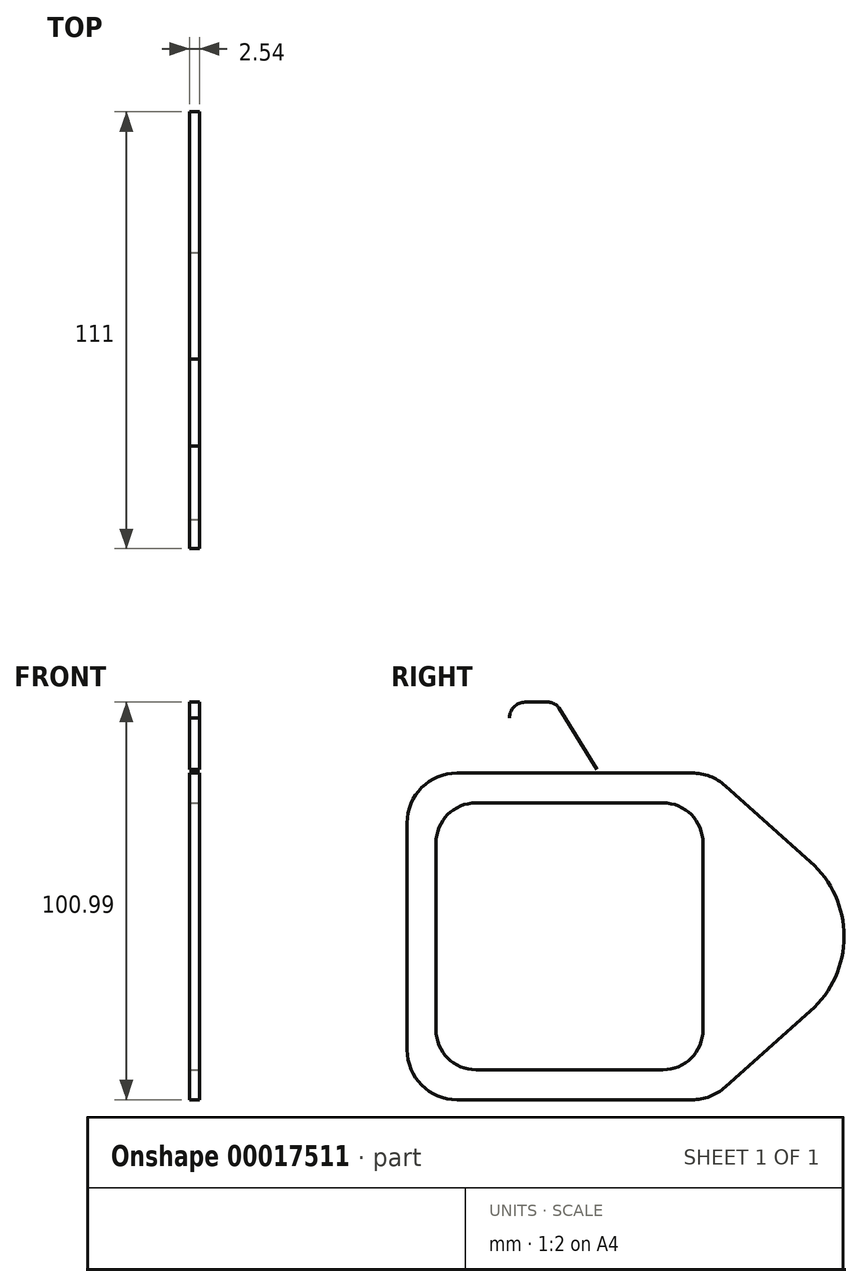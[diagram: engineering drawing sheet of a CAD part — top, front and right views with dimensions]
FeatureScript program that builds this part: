
annotation { "Feature Type Name" : "Feature", "Feature Type Description" : "" }
export const myFeature = defineFeature(function(context is Context, id is Id, definition is map)
    precondition{}
    {
        {
            var Q0;
            Q0=qCreatedBy(makeId("Right.planeOp"),FACE);
            var sketch = newSketch(context, id + "F0", { "sketchPlane" : qUnion([Q0])});
            skLineSegment(sketch, "E0", {"start": v(-102.55, -77) * mm, "end": v(-101.6, -77) * mm});
            skLineSegment(sketch, "E1", {"start": v(-45.83, -77) * mm, "end": v(-44.89, -77) * mm});
            skLineSegment(sketch, "E2", {"start": v(-44.89, -72.94) * mm, "end": v(-45.83, -72.94) * mm});
            skLineSegment(sketch, "E3", {"start": v(-101.6, -72.94) * mm, "end": v(-102.55, -72.94) * mm});
            skCircle(sketch, "E4", {"center": v(-22.9, -92.72) * mm, "radius": 11.4 * mm});
            skLineSegment(sketch, "E5", {"start": v(-51.07, -67.37) * mm, "end": v(-51.07, -64.63) * mm});
            skLineSegment(sketch, "E6", {"start": v(-52.08, -64.63) * mm, "end": v(-52.08, -67.37) * mm});
            skLineSegment(sketch, "E7", {"start": v(-24.14, -96.22) * mm, "end": v(-21.64, -96.22) * mm});
            skLineSegment(sketch, "E8", {"start": v(-21.64, -89.12) * mm, "end": v(-24.14, -89.12) * mm});
            skLineSegment(sketch, "E9", {"start": v(-24.14, -89.12) * mm, "end": v(-24.14, -99.37) * mm});
            skLineSegment(sketch, "E10", {"start": v(-24.14, -99.37) * mm, "end": v(-21.64, -99.37) * mm});
            skArc(sketch, "E11", {"start": v(-21.64, -95.44) * mm, "mid": v(-19.9, -92.72) * mm, "end": v(-21.64, -90) * mm});
            skLineSegment(sketch, "E12", {"start": v(-21.64, -99.37) * mm, "end": v(-21.64, -95.44) * mm});
            skLineSegment(sketch, "E13", {"start": v(-21.64, -90) * mm, "end": v(-21.64, -89.12) * mm});
            skLineSegment(sketch, "E14", {"start": v(-21.64, -90) * mm, "end": v(-21.64, -91.11) * mm});
            skLineSegment(sketch, "E15", {"start": v(-21.64, -94.32) * mm, "end": v(-21.64, -95.44) * mm});
            skCircle(sketch, "E16", {"center": v(-22.9, -92.72) * mm, "radius": 7.77 * mm});
            skArc(sketch, "E17", {"start": v(-102.55, -116.47) * mm, "mid": v(-101.06, -120.06) * mm, "end": v(-97.47, -121.55) * mm});
            skArc(sketch, "E18", {"start": v(-97.47, -63.89) * mm, "mid": v(-101.06, -65.38) * mm, "end": v(-102.55, -68.97) * mm});
            skLineSegment(sketch, "E19", {"start": v(-97.47, -63.89) * mm, "end": v(-49.97, -63.89) * mm});
            skLineSegment(sketch, "E20", {"start": v(-44.89, -68.97) * mm, "end": v(-44.89, -116.47) * mm});
            skLineSegment(sketch, "E21", {"start": v(-102.55, -116.47) * mm, "end": v(-102.55, -68.97) * mm});
            skLineSegment(sketch, "E22", {"start": v(-49.97, -121.55) * mm, "end": v(-97.47, -121.55) * mm});
            skCircle(sketch, "E23", {"center": v(-24.43, -68.08) * mm, "radius": 2.62 * mm});
            skCircle(sketch, "E24", {"center": v(-101.9, -129.17) * mm, "radius": 2.62 * mm});
            skLineSegment(sketch, "E25", {"start": v(-34.14, -131) * mm, "end": v(-12.47, -111.67) * mm});
            skArc(sketch, "E26", {"start": v(-42.59, -134.21) * mm, "mid": v(-38.07, -133.38) * mm, "end": v(-34.14, -131) * mm});
            skLineSegment(sketch, "E27", {"start": v(-102.28, -134.21) * mm, "end": v(-42.59, -134.21) * mm});
            skArc(sketch, "E28", {"start": v(-114.98, -121.51) * mm, "mid": v(-111.26, -130.5) * mm, "end": v(-102.28, -134.21) * mm});
            skLineSegment(sketch, "E29", {"start": v(-114.98, -63.92) * mm, "end": v(-114.98, -121.51) * mm});
            skArc(sketch, "E30", {"start": v(-102.28, -51.22) * mm, "mid": v(-111.26, -54.94) * mm, "end": v(-114.98, -63.92) * mm});
            skLineSegment(sketch, "E31", {"start": v(-42.59, -51.22) * mm, "end": v(-102.28, -51.22) * mm});
            skArc(sketch, "E32", {"start": v(-34.14, -54.44) * mm, "mid": v(-38.07, -52.05) * mm, "end": v(-42.59, -51.22) * mm});
            skLineSegment(sketch, "E33", {"start": v(-12.47, -73.76) * mm, "end": v(-34.14, -54.44) * mm});
            skArc(sketch, "E34", {"start": v(-12.47, -111.67) * mm, "mid": v(-3.98, -92.72) * mm, "end": v(-12.47, -73.76) * mm});
            skCircle(sketch, "E35", {"center": v(-101.9, -56.27) * mm, "radius": 2.62 * mm});
            skCircle(sketch, "E36", {"center": v(-24.43, -117.36) * mm, "radius": 2.62 * mm});
            skArc(sketch, "E37", {"start": v(-49.97, -121.55) * mm, "mid": v(-46.38, -120.06) * mm, "end": v(-44.89, -116.47) * mm});
            skArc(sketch, "E38", {"start": v(-44.89, -68.97) * mm, "mid": v(-46.38, -65.38) * mm, "end": v(-49.97, -63.89) * mm});
            skLineSegment(sketch, "E39", {"start": v(-88.96, -37.19) * mm, "end": v(-88.96, -51.22) * mm});
            skArc(sketch, "E40", {"start": v(-84.99, -33.22) * mm, "mid": v(-87.8, -34.38) * mm, "end": v(-88.96, -37.19) * mm});
            skLineSegment(sketch, "E41", {"start": v(-79.1, -33.22) * mm, "end": v(-84.99, -33.22) * mm});
            skArc(sketch, "E42", {"start": v(-76.4, -34.72) * mm, "mid": v(-77.56, -33.62) * mm, "end": v(-79.1, -33.22) * mm});
            skLineSegment(sketch, "E43", {"start": v(-66.78, -50.29) * mm, "end": v(-76.4, -34.72) * mm});
            skArc(sketch, "E44", {"start": v(-66.65, -51.22) * mm, "mid": v(-66.62, -50.74) * mm, "end": v(-66.78, -50.29) * mm});
            skLineSegment(sketch, "E45", {"start": v(-30.34, -95.47) * mm, "end": v(-30.16, -95.47) * mm});
            skLineSegment(sketch, "E46", {"start": v(-25.64, -99.99) * mm, "end": v(-25.64, -100.16) * mm});
            skLineSegment(sketch, "E47", {"start": v(-20.14, -85.27) * mm, "end": v(-20.66, -85.27) * mm});
            skLineSegment(sketch, "E48", {"start": v(-25.12, -85.27) * mm, "end": v(-25.64, -85.27) * mm});
            skLineSegment(sketch, "E49", {"start": v(-25.64, -85.27) * mm, "end": v(-25.64, -85.45) * mm});
            skLineSegment(sketch, "E50", {"start": v(-30.16, -89.97) * mm, "end": v(-30.34, -89.97) * mm});
            skLineSegment(sketch, "E51", {"start": v(-20.14, -85.45) * mm, "end": v(-20.14, -85.27) * mm});
            skLineSegment(sketch, "E52", {"start": v(-15.44, -89.97) * mm, "end": v(-15.62, -89.97) * mm});
            skLineSegment(sketch, "E53", {"start": v(-30.34, -89.97) * mm, "end": v(-30.34, -90.49) * mm});
            skLineSegment(sketch, "E54", {"start": v(-30.34, -94.95) * mm, "end": v(-30.34, -95.47) * mm});
            skLineSegment(sketch, "E55", {"start": v(-15.44, -95.47) * mm, "end": v(-15.44, -94.95) * mm});
            skLineSegment(sketch, "E56", {"start": v(-15.44, -90.49) * mm, "end": v(-15.44, -89.97) * mm});
            skLineSegment(sketch, "E57", {"start": v(-20.14, -100.16) * mm, "end": v(-20.14, -99.99) * mm});
            skLineSegment(sketch, "E58", {"start": v(-15.62, -95.47) * mm, "end": v(-15.44, -95.47) * mm});
            skLineSegment(sketch, "E59", {"start": v(-25.64, -100.16) * mm, "end": v(-25.12, -100.16) * mm});
            skLineSegment(sketch, "E60", {"start": v(-20.66, -100.16) * mm, "end": v(-20.14, -100.16) * mm});
            skArc(sketch, "E61", {"start": v(-21.64, -90.22) * mm, "mid": v(-22.52, -92.72) * mm, "end": v(-21.64, -95.22) * mm});
            skLineSegment(sketch, "E62", {"start": v(-21.64, -94.32) * mm, "end": v(-21.64, -91.11) * mm});
            skArc(sketch, "E63", {"start": v(-85, -102.03) * mm, "mid": v(-81.85, -103.85) * mm, "end": v(-78.26, -104.45) * mm});
            skArc(sketch, "E64", {"start": v(-85, -102.97) * mm, "mid": v(-81.85, -104.79) * mm, "end": v(-78.26, -105.4) * mm});
            skLineSegment(sketch, "E65", {"start": v(-62.43, -102.03) * mm, "end": v(-61.44, -101.18) * mm});
            skArc(sketch, "E66", {"start": v(-69.17, -104.45) * mm, "mid": v(-65.59, -103.85) * mm, "end": v(-62.43, -102.03) * mm});
            skLineSegment(sketch, "E67", {"start": v(-78.26, -104.45) * mm, "end": v(-69.17, -104.45) * mm});
            skLineSegment(sketch, "E68", {"start": v(-85.99, -101.18) * mm, "end": v(-85, -102.03) * mm});
            skArc(sketch, "E69", {"start": v(-69.17, -105.4) * mm, "mid": v(-65.59, -104.79) * mm, "end": v(-62.43, -102.97) * mm});
            skLineSegment(sketch, "E70", {"start": v(-78.26, -105.4) * mm, "end": v(-69.17, -105.4) * mm});
            skLineSegment(sketch, "E71", {"start": v(-85.99, -102.12) * mm, "end": v(-85, -102.97) * mm});
            skLineSegment(sketch, "E72", {"start": v(-85.99, -102.12) * mm, "end": v(-85.99, -101.18) * mm});
            skLineSegment(sketch, "E73", {"start": v(-62.43, -102.97) * mm, "end": v(-61.44, -102.12) * mm});
            skLineSegment(sketch, "E74", {"start": v(-61.44, -101.18) * mm, "end": v(-61.44, -102.12) * mm});
            skLineSegment(sketch, "E75", {"start": v(-86.97, -100.45) * mm, "end": v(-85.99, -101.18) * mm});
            skLineSegment(sketch, "E76", {"start": v(-86.97, -101.05) * mm, "end": v(-85.99, -102.12) * mm});
            skLineSegment(sketch, "E77", {"start": v(-86.97, -101.05) * mm, "end": v(-86.97, -100.45) * mm});
            skLineSegment(sketch, "E78", {"start": v(-60.46, -100.45) * mm, "end": v(-59.35, -99.73) * mm});
            skLineSegment(sketch, "E79", {"start": v(-59.35, -99.73) * mm, "end": v(-58.36, -99.2) * mm});
            skLineSegment(sketch, "E80", {"start": v(-61.44, -101.18) * mm, "end": v(-60.46, -100.45) * mm});
            skLineSegment(sketch, "E81", {"start": v(-89.07, -99.2) * mm, "end": v(-87.9, -99.84) * mm});
            skLineSegment(sketch, "E82", {"start": v(-87.9, -99.84) * mm, "end": v(-86.97, -100.45) * mm});
            skLineSegment(sketch, "E83", {"start": v(-60.46, -101.05) * mm, "end": v(-60.46, -100.45) * mm});
            skLineSegment(sketch, "E84", {"start": v(-61.44, -102.12) * mm, "end": v(-60.46, -101.05) * mm});
            skLineSegment(sketch, "E85", {"start": v(-89.07, -99.2) * mm, "end": v(-87.9, -100.15) * mm});
            skLineSegment(sketch, "E86", {"start": v(-87.9, -100.15) * mm, "end": v(-86.97, -101.05) * mm});
            skLineSegment(sketch, "E87", {"start": v(-60.46, -101.05) * mm, "end": v(-59.35, -99.99) * mm});
            skLineSegment(sketch, "E88", {"start": v(-59.35, -99.99) * mm, "end": v(-58.36, -99.2) * mm});
            skLineSegment(sketch, "E89", {"start": v(-99.34, -97.99) * mm, "end": v(-93.71, -97.99) * mm});
            skLineSegment(sketch, "E90", {"start": v(-53.72, -97.99) * mm, "end": v(-48.1, -97.99) * mm});
            skArc(sketch, "E91", {"start": v(-53.72, -97.99) * mm, "mid": v(-56.12, -98.3) * mm, "end": v(-58.36, -99.2) * mm});
            skArc(sketch, "E92", {"start": v(-89.07, -99.2) * mm, "mid": v(-91.31, -98.3) * mm, "end": v(-93.71, -97.99) * mm});
            skArc(sketch, "E93", {"start": v(-99.01, -67.37) * mm, "mid": v(-99.25, -68.49) * mm, "end": v(-99.34, -69.63) * mm});
            skLineSegment(sketch, "E94", {"start": v(-48.42, -67.37) * mm, "end": v(-99.01, -67.37) * mm});
            skArc(sketch, "E95", {"start": v(-48.1, -69.63) * mm, "mid": v(-48.18, -68.49) * mm, "end": v(-48.42, -67.37) * mm});
            skLineSegment(sketch, "E96", {"start": v(-45.83, -69.95) * mm, "end": v(-45.83, -97.99) * mm});
            skLineSegment(sketch, "E97", {"start": v(-45.83, -97.99) * mm, "end": v(-48.1, -97.99) * mm});
            skArc(sketch, "E98", {"start": v(-45.83, -69.95) * mm, "mid": v(-46.95, -69.72) * mm, "end": v(-48.1, -69.63) * mm});
            skLineSegment(sketch, "E99", {"start": v(-99.34, -97.99) * mm, "end": v(-101.6, -97.99) * mm});
            skLineSegment(sketch, "E100", {"start": v(-101.6, -69.95) * mm, "end": v(-101.6, -97.99) * mm});
            skArc(sketch, "E101", {"start": v(-99.34, -69.63) * mm, "mid": v(-100.48, -69.72) * mm, "end": v(-101.6, -69.95) * mm});
            skCircle(sketch, "E102", {"center": v(-22.9, -92.72) * mm, "radius": 7.94 * mm});
            skLineSegment(sketch, "E103", {"start": v(-52.08, -64.63) * mm, "end": v(-52.04, -64.56) * mm});
            skLineSegment(sketch, "E104", {"start": v(-52.04, -64.56) * mm, "end": v(-51.93, -64.5) * mm});
            skLineSegment(sketch, "E105", {"start": v(-51.93, -64.5) * mm, "end": v(-51.77, -64.47) * mm});
            skLineSegment(sketch, "E106", {"start": v(-51.77, -64.47) * mm, "end": v(-51.58, -64.45) * mm});
            skLineSegment(sketch, "E107", {"start": v(-51.58, -64.45) * mm, "end": v(-51.38, -64.47) * mm});
            skLineSegment(sketch, "E108", {"start": v(-51.38, -64.47) * mm, "end": v(-51.22, -64.5) * mm});
            skLineSegment(sketch, "E109", {"start": v(-51.22, -64.5) * mm, "end": v(-51.11, -64.56) * mm});
            skLineSegment(sketch, "E110", {"start": v(-51.11, -64.56) * mm, "end": v(-51.07, -64.63) * mm});
            skCircle(sketch, "E111", {"center": v(-22.9, -92.72) * mm, "radius": 7.52 * mm});
            skArc(sketch, "E112", {"start": v(-107.63, -116.47) * mm, "mid": v(-104.65, -123.65) * mm, "end": v(-97.47, -126.63) * mm});
            skLineSegment(sketch, "E113", {"start": v(-102.55, -116.47) * mm, "end": v(-107.63, -116.47) * mm});
            skLineSegment(sketch, "E114", {"start": v(-97.47, -121.55) * mm, "end": v(-97.47, -126.63) * mm});
            skArc(sketch, "E115", {"start": v(-97.47, -58.8) * mm, "mid": v(-104.65, -61.78) * mm, "end": v(-107.63, -68.97) * mm});
            skLineSegment(sketch, "E116", {"start": v(-97.47, -58.8) * mm, "end": v(-97.47, -63.89) * mm});
            skLineSegment(sketch, "E117", {"start": v(-102.55, -68.97) * mm, "end": v(-107.63, -68.97) * mm});
            skLineSegment(sketch, "E118", {"start": v(-49.97, -58.8) * mm, "end": v(-97.47, -58.8) * mm});
            skLineSegment(sketch, "E119", {"start": v(-49.97, -58.8) * mm, "end": v(-49.97, -63.89) * mm});
            skLineSegment(sketch, "E120", {"start": v(-39.8, -68.97) * mm, "end": v(-44.89, -68.97) * mm});
            skLineSegment(sketch, "E121", {"start": v(-39.8, -116.47) * mm, "end": v(-39.8, -68.97) * mm});
            skLineSegment(sketch, "E122", {"start": v(-39.8, -116.47) * mm, "end": v(-44.89, -116.47) * mm});
            skLineSegment(sketch, "E123", {"start": v(-107.63, -68.97) * mm, "end": v(-107.63, -116.47) * mm});
            skLineSegment(sketch, "E124", {"start": v(-97.47, -126.63) * mm, "end": v(-49.97, -126.63) * mm});
            skLineSegment(sketch, "E125", {"start": v(-49.97, -121.55) * mm, "end": v(-49.97, -126.63) * mm});
            skArc(sketch, "E126", {"start": v(-49.97, -126.63) * mm, "mid": v(-42.78, -123.65) * mm, "end": v(-39.8, -116.47) * mm});
            skArc(sketch, "E127", {"start": v(-39.8, -68.97) * mm, "mid": v(-42.78, -61.78) * mm, "end": v(-49.97, -58.8) * mm});
            skLineSegment(sketch, "E128", {"start": v(-97.47, -63.89) * mm, "end": v(-97.47, -67.38) * mm});
            skLineSegment(sketch, "E129", {"start": v(-49.97, -63.89) * mm, "end": v(-49.97, -67.38) * mm});
            skLineSegment(sketch, "E130", {"start": v(-44.89, -68.97) * mm, "end": v(-48.16, -68.97) * mm});
            skLineSegment(sketch, "E131", {"start": v(-97.47, -118.05) * mm, "end": v(-97.47, -121.55) * mm});
            skLineSegment(sketch, "E132", {"start": v(-49.97, -118.05) * mm, "end": v(-97.47, -118.05) * mm});
            skLineSegment(sketch, "E133", {"start": v(-49.97, -118.05) * mm, "end": v(-49.97, -121.55) * mm});
            skLineSegment(sketch, "E134", {"start": v(-48.38, -116.47) * mm, "end": v(-44.89, -116.47) * mm});
            skLineSegment(sketch, "E135", {"start": v(-48.38, -97.99) * mm, "end": v(-48.38, -116.47) * mm});
            skLineSegment(sketch, "E136", {"start": v(-44.97, -93.4) * mm, "end": v(-45, -94.07) * mm});
            skLineSegment(sketch, "E137", {"start": v(-45, -94.07) * mm, "end": v(-45.11, -94.68) * mm});
            skLineSegment(sketch, "E138", {"start": v(-45.11, -94.68) * mm, "end": v(-45.34, -95.13) * mm});
            skLineSegment(sketch, "E139", {"start": v(-45.34, -95.13) * mm, "end": v(-45.72, -95.42) * mm});
            skLineSegment(sketch, "E140", {"start": v(-45.72, -95.42) * mm, "end": v(-45.83, -95.45) * mm});
            skLineSegment(sketch, "E141", {"start": v(-44.97, -92.04) * mm, "end": v(-44.97, -93.4) * mm});
            skLineSegment(sketch, "E142", {"start": v(-45.83, -89.99) * mm, "end": v(-45.72, -90.02) * mm});
            skLineSegment(sketch, "E143", {"start": v(-45.72, -90.02) * mm, "end": v(-45.34, -90.3) * mm});
            skLineSegment(sketch, "E144", {"start": v(-45.34, -90.3) * mm, "end": v(-45.11, -90.76) * mm});
            skLineSegment(sketch, "E145", {"start": v(-45.11, -90.76) * mm, "end": v(-45, -91.36) * mm});
            skLineSegment(sketch, "E146", {"start": v(-45, -91.36) * mm, "end": v(-44.97, -92.04) * mm});
            skLineSegment(sketch, "E147", {"start": v(-102.55, -68.97) * mm, "end": v(-99.28, -68.97) * mm});
            skArc(sketch, "E148", {"start": v(-49.97, -118.05) * mm, "mid": v(-48.84, -117.59) * mm, "end": v(-48.38, -116.47) * mm});
            skLineSegment(sketch, "E149", {"start": v(-101.6, -95.45) * mm, "end": v(-101.71, -95.42) * mm});
            skLineSegment(sketch, "E150", {"start": v(-101.71, -95.42) * mm, "end": v(-102.09, -95.13) * mm});
            skLineSegment(sketch, "E151", {"start": v(-102.09, -95.13) * mm, "end": v(-102.32, -94.68) * mm});
            skLineSegment(sketch, "E152", {"start": v(-102.32, -94.68) * mm, "end": v(-102.43, -94.07) * mm});
            skLineSegment(sketch, "E153", {"start": v(-102.43, -94.07) * mm, "end": v(-102.46, -93.4) * mm});
            skLineSegment(sketch, "E154", {"start": v(-99.05, -116.47) * mm, "end": v(-99.05, -97.99) * mm});
            skLineSegment(sketch, "E155", {"start": v(-99.05, -116.47) * mm, "end": v(-102.55, -116.47) * mm});
            skLineSegment(sketch, "E156", {"start": v(-102.46, -92.04) * mm, "end": v(-102.43, -91.36) * mm});
            skLineSegment(sketch, "E157", {"start": v(-102.43, -91.36) * mm, "end": v(-102.32, -90.76) * mm});
            skLineSegment(sketch, "E158", {"start": v(-102.32, -90.76) * mm, "end": v(-102.09, -90.3) * mm});
            skLineSegment(sketch, "E159", {"start": v(-102.09, -90.3) * mm, "end": v(-101.71, -90.02) * mm});
            skLineSegment(sketch, "E160", {"start": v(-101.71, -90.02) * mm, "end": v(-101.6, -89.99) * mm});
            skLineSegment(sketch, "E161", {"start": v(-102.46, -93.4) * mm, "end": v(-102.46, -92.04) * mm});
            skArc(sketch, "E162", {"start": v(-99.05, -116.47) * mm, "mid": v(-98.59, -117.59) * mm, "end": v(-97.47, -118.05) * mm});
            skLineSegment(sketch, "E163", {"start": v(-102.46, -93.4) * mm, "end": v(-102.27, -93.4) * mm});
            skArc(sketch, "E164", {"start": v(-102.27, -93.4) * mm, "mid": v(-102.2, -94.37) * mm, "end": v(-101.6, -95.16) * mm});
            skArc(sketch, "E165", {"start": v(-101.6, -90.28) * mm, "mid": v(-102.2, -91.06) * mm, "end": v(-102.27, -92.04) * mm});
            skLineSegment(sketch, "E166", {"start": v(-102.27, -92.04) * mm, "end": v(-102.46, -92.04) * mm});
            skArc(sketch, "E167", {"start": v(-45.83, -95.16) * mm, "mid": v(-45.24, -94.37) * mm, "end": v(-45.17, -93.4) * mm});
            skLineSegment(sketch, "E168", {"start": v(-45.17, -93.4) * mm, "end": v(-44.97, -93.4) * mm});
            skLineSegment(sketch, "E169", {"start": v(-44.97, -92.04) * mm, "end": v(-45.17, -92.04) * mm});
            skArc(sketch, "E170", {"start": v(-45.17, -92.04) * mm, "mid": v(-45.24, -91.06) * mm, "end": v(-45.83, -90.28) * mm});
            skLineSegment(sketch, "E171", {"start": v(-102.27, -92.04) * mm, "end": v(-102.27, -93.4) * mm});
            skLineSegment(sketch, "E172", {"start": v(-45.17, -93.4) * mm, "end": v(-45.17, -92.04) * mm});
            skLineSegment(sketch, "E173", {"start": v(-101.6, -93.4) * mm, "end": v(-102.27, -93.4) * mm});
            skLineSegment(sketch, "E174", {"start": v(-102.27, -92.04) * mm, "end": v(-101.6, -92.04) * mm});
            skLineSegment(sketch, "E175", {"start": v(-45.83, -92.04) * mm, "end": v(-45.17, -92.04) * mm});
            skLineSegment(sketch, "E176", {"start": v(-45.17, -93.4) * mm, "end": v(-45.83, -93.4) * mm});
            skLineSegment(sketch, "E177", {"start": v(-85, -102.03) * mm, "end": v(-85, -102.97) * mm});
            skLineSegment(sketch, "E178", {"start": v(-78.26, -104.45) * mm, "end": v(-78.26, -105.4) * mm});
            skLineSegment(sketch, "E179", {"start": v(-85.99, -101.18) * mm, "end": v(-61.44, -101.18) * mm});
            skLineSegment(sketch, "E180", {"start": v(-69.17, -104.45) * mm, "end": v(-69.17, -105.4) * mm});
            skLineSegment(sketch, "E181", {"start": v(-62.43, -102.03) * mm, "end": v(-62.43, -102.97) * mm});
            skLineSegment(sketch, "E182", {"start": v(-89.07, -99.2) * mm, "end": v(-58.36, -99.2) * mm});
            skLineSegment(sketch, "E183", {"start": v(-99.34, -69.63) * mm, "end": v(-99.34, -97.99) * mm});
            skLineSegment(sketch, "E184", {"start": v(-48.1, -69.63) * mm, "end": v(-99.34, -69.63) * mm});
            skLineSegment(sketch, "E185", {"start": v(-48.1, -97.99) * mm, "end": v(-48.1, -69.63) * mm});
            skCircle(sketch, "E186", {"center": v(-22.9, -92.72) * mm, "radius": 11.39 * mm});
            skLineSegment(sketch, "E187", {"start": v(0, 0) * mm, "end": v(0, 2.5) * mm});
            skLineSegment(sketch, "E188", {"start": v(0, 0) * mm, "end": v(-2.5, 0) * mm});
            skLineSegment(sketch, "E189", {"start": v(0, 0) * mm, "end": v(0, -2.5) * mm});
            skLineSegment(sketch, "E190", {"start": v(0, 0) * mm, "end": v(2.5, 0) * mm});
            skLineSegment(sketch, "E191", {"start": v(0, 5) * mm, "end": v(0, 10.44) * mm});
            skLineSegment(sketch, "E192", {"start": v(-5, 0) * mm, "end": v(-10.44, 0) * mm});
            skLineSegment(sketch, "E193", {"start": v(0, -5) * mm, "end": v(0, -10.44) * mm});
            skLineSegment(sketch, "E194", {"start": v(5, 0) * mm, "end": v(10.44, 0) * mm});
            skLineSegment(sketch, "E195", {"start": v(0, 5) * mm, "end": v(0, 5.12) * mm});
            skLineSegment(sketch, "E196", {"start": v(-5, 0) * mm, "end": v(-5.12, 0) * mm});
            skLineSegment(sketch, "E197", {"start": v(0, -5) * mm, "end": v(0, -5.12) * mm});
            skLineSegment(sketch, "E198", {"start": v(5, 0) * mm, "end": v(5.12, 0) * mm});
            skLineSegment(sketch, "E199", {"start": v(28.15, -84.95) * mm, "end": v(28.07, -84.95) * mm});
            skLineSegment(sketch, "E200", {"start": v(28.07, -100.5) * mm, "end": v(28.15, -100.5) * mm});
            skArc(sketch, "E201", {"start": v(27.82, -100.24) * mm, "mid": v(27.9, -100.42) * mm, "end": v(28.07, -100.5) * mm});
            skArc(sketch, "E202", {"start": v(28.07, -84.95) * mm, "mid": v(27.9, -85.02) * mm, "end": v(27.82, -85.2) * mm});
            skArc(sketch, "E203", {"start": v(51.7, -88.45) * mm, "mid": v(51.53, -87.43) * mm, "end": v(51.06, -86.52) * mm});
            skArc(sketch, "E204", {"start": v(51.06, -98.92) * mm, "mid": v(51.53, -98) * mm, "end": v(51.7, -96.99) * mm});
            skLineSegment(sketch, "E205", {"start": v(51.7, -96.99) * mm, "end": v(51.7, -88.45) * mm});
            skLineSegment(sketch, "E206", {"start": v(53.78, -72.41) * mm, "end": v(53.11, -71.26) * mm});
            skLineSegment(sketch, "E207", {"start": v(57.88, -72.38) * mm, "end": v(57.07, -72.38) * mm});
            skLineSegment(sketch, "E208", {"start": v(55.67, -72.38) * mm, "end": v(55.37, -72.38) * mm});
            skLineSegment(sketch, "E209", {"start": v(38.55, -103.77) * mm, "end": v(38.68, -103.56) * mm});
            skLineSegment(sketch, "E210", {"start": v(38.68, -81.87) * mm, "end": v(38.55, -81.67) * mm});
            skLineSegment(sketch, "E211", {"start": v(34.5, -81.67) * mm, "end": v(34.45, -81.77) * mm});
            skLineSegment(sketch, "E212", {"start": v(34.45, -103.66) * mm, "end": v(34.5, -103.77) * mm});
            skArc(sketch, "E213", {"start": v(55.77, -70.67) * mm, "mid": v(55.48, -78.99) * mm, "end": v(55.24, -87.3) * mm});
            skLineSegment(sketch, "E214", {"start": v(55.68, -72.27) * mm, "end": v(55.68, -72.23) * mm});
            skLineSegment(sketch, "E215", {"start": v(55.68, -72.23) * mm, "end": v(55.64, -71.5) * mm});
            skLineSegment(sketch, "E216", {"start": v(55.64, -71.5) * mm, "end": v(55.6, -70.91) * mm});
            skLineSegment(sketch, "E217", {"start": v(55.6, -70.91) * mm, "end": v(55.58, -70.5) * mm});
            skLineSegment(sketch, "E218", {"start": v(55.58, -70.5) * mm, "end": v(55.54, -70.14) * mm});
            skLineSegment(sketch, "E219", {"start": v(55.54, -70.14) * mm, "end": v(55.5, -69.93) * mm});
            skLineSegment(sketch, "E220", {"start": v(55.5, -69.93) * mm, "end": v(55.46, -69.82) * mm});
            skLineSegment(sketch, "E221", {"start": v(55.46, -69.82) * mm, "end": v(55.35, -69.64) * mm});
            skLineSegment(sketch, "E222", {"start": v(55.35, -69.64) * mm, "end": v(55.24, -69.52) * mm});
            skLineSegment(sketch, "E223", {"start": v(55.24, -69.52) * mm, "end": v(55.05, -69.4) * mm});
            skLineSegment(sketch, "E224", {"start": v(55.05, -69.4) * mm, "end": v(54.9, -69.37) * mm});
            skLineSegment(sketch, "E225", {"start": v(54.9, -69.37) * mm, "end": v(54.72, -69.37) * mm});
            skLineSegment(sketch, "E226", {"start": v(54.72, -69.37) * mm, "end": v(54.47, -69.44) * mm});
            skLineSegment(sketch, "E227", {"start": v(54.47, -69.44) * mm, "end": v(54.32, -69.55) * mm});
            skLineSegment(sketch, "E228", {"start": v(54.32, -69.55) * mm, "end": v(54.23, -69.65) * mm});
            skLineSegment(sketch, "E229", {"start": v(54.23, -69.65) * mm, "end": v(54.14, -69.8) * mm});
            skLineSegment(sketch, "E230", {"start": v(54.14, -69.8) * mm, "end": v(54.07, -70.04) * mm});
            skLineSegment(sketch, "E231", {"start": v(54.07, -70.04) * mm, "end": v(54.03, -70.31) * mm});
            skLineSegment(sketch, "E232", {"start": v(54.03, -70.31) * mm, "end": v(54, -70.77) * mm});
            skLineSegment(sketch, "E233", {"start": v(54, -70.77) * mm, "end": v(53.96, -71.23) * mm});
            skLineSegment(sketch, "E234", {"start": v(53.96, -71.23) * mm, "end": v(53.93, -71.85) * mm});
            skLineSegment(sketch, "E235", {"start": v(53.93, -71.85) * mm, "end": v(53.9, -72.36) * mm});
            skArc(sketch, "E236", {"start": v(53.87, -73.47) * mm, "mid": v(53.65, -80.39) * mm, "end": v(53.47, -87.3) * mm});
            skLineSegment(sketch, "E237", {"start": v(54.87, -87.3) * mm, "end": v(54.9, -86.44) * mm});
            skLineSegment(sketch, "E238", {"start": v(54.9, -86.44) * mm, "end": v(54.94, -85.03) * mm});
            skLineSegment(sketch, "E239", {"start": v(54.94, -85.03) * mm, "end": v(54.98, -83.73) * mm});
            skLineSegment(sketch, "E240", {"start": v(54.98, -83.73) * mm, "end": v(55, -82.61) * mm});
            skLineSegment(sketch, "E241", {"start": v(55, -82.61) * mm, "end": v(55.03, -81.7) * mm});
            skLineSegment(sketch, "E242", {"start": v(55.03, -81.7) * mm, "end": v(55.05, -80.94) * mm});
            skLineSegment(sketch, "E243", {"start": v(55.05, -80.94) * mm, "end": v(55.06, -80.45) * mm});
            skLineSegment(sketch, "E244", {"start": v(55.06, -80.45) * mm, "end": v(55.07, -80.11) * mm});
            skLineSegment(sketch, "E245", {"start": v(55.07, -80.11) * mm, "end": v(55.08, -79.65) * mm});
            skLineSegment(sketch, "E246", {"start": v(55.08, -79.65) * mm, "end": v(55.1, -79.05) * mm});
            skLineSegment(sketch, "E247", {"start": v(55.1, -79.05) * mm, "end": v(55.12, -78.33) * mm});
            skLineSegment(sketch, "E248", {"start": v(55.12, -78.33) * mm, "end": v(55.14, -77.5) * mm});
            skLineSegment(sketch, "E249", {"start": v(55.14, -77.5) * mm, "end": v(55.19, -76.02) * mm});
            skLineSegment(sketch, "E250", {"start": v(55.19, -76.02) * mm, "end": v(55.23, -74.65) * mm});
            skLineSegment(sketch, "E251", {"start": v(55.23, -74.65) * mm, "end": v(55.27, -73.38) * mm});
            skLineSegment(sketch, "E252", {"start": v(55.27, -73.38) * mm, "end": v(55.3, -72.84) * mm});
            skArc(sketch, "E253", {"start": v(55.43, -70.35) * mm, "mid": v(55.36, -71.3) * mm, "end": v(55.31, -72.26) * mm});
            skArc(sketch, "E254", {"start": v(57.16, -70.76) * mm, "mid": v(56.87, -79.03) * mm, "end": v(56.64, -87.3) * mm});
            skLineSegment(sketch, "E255", {"start": v(57.16, -70.71) * mm, "end": v(57.16, -70.07) * mm});
            skArc(sketch, "E256", {"start": v(57.16, -70.07) * mm, "mid": v(56.46, -69.37) * mm, "end": v(55.76, -70.07) * mm});
            skLineSegment(sketch, "E257", {"start": v(55.76, -70.07) * mm, "end": v(55.76, -70.71) * mm});
            skLineSegment(sketch, "E258", {"start": v(57.16, -72.38) * mm, "end": v(57.16, -70.77) * mm});
            skLineSegment(sketch, "E259", {"start": v(49.06, -108.6) * mm, "end": v(51.06, -108.6) * mm});
            skLineSegment(sketch, "E260", {"start": v(51.06, -83.6) * mm, "end": v(49.06, -83.6) * mm});
            skArc(sketch, "E261", {"start": v(32.37, -104.1) * mm, "mid": v(32.9, -103.98) * mm, "end": v(33.18, -103.51) * mm});
            skArc(sketch, "E262", {"start": v(33.18, -81.92) * mm, "mid": v(32.9, -81.45) * mm, "end": v(32.37, -81.33) * mm});
            skArc(sketch, "E263", {"start": v(28.15, -100.66) * mm, "mid": v(29.8, -102.93) * mm, "end": v(32.37, -104.1) * mm});
            skArc(sketch, "E264", {"start": v(32.37, -81.33) * mm, "mid": v(29.8, -82.5) * mm, "end": v(28.15, -84.78) * mm});
            skArc(sketch, "E265", {"start": v(62.78, -88.24) * mm, "mid": v(63.23, -88.05) * mm, "end": v(63.42, -87.6) * mm});
            skArc(sketch, "E266", {"start": v(63.42, -72.98) * mm, "mid": v(63.23, -72.53) * mm, "end": v(62.78, -72.34) * mm});
            skLineSegment(sketch, "E267", {"start": v(61.51, -88.24) * mm, "end": v(62.78, -88.24) * mm});
            skLineSegment(sketch, "E268", {"start": v(62.78, -72.34) * mm, "end": v(61.51, -72.34) * mm});
            skArc(sketch, "E269", {"start": v(60.88, -87.6) * mm, "mid": v(61.06, -88.05) * mm, "end": v(61.51, -88.24) * mm});
            skArc(sketch, "E270", {"start": v(61.51, -72.34) * mm, "mid": v(61.06, -72.53) * mm, "end": v(60.88, -72.98) * mm});
            skLineSegment(sketch, "E271", {"start": v(53.11, -73.8) * mm, "end": v(55.52, -72.73) * mm});
            skLineSegment(sketch, "E272", {"start": v(55.11, -71.82) * mm, "end": v(53.11, -72.71) * mm});
            skLineSegment(sketch, "E273", {"start": v(27.82, -92.72) * mm, "end": v(27.82, -85.2) * mm});
            skLineSegment(sketch, "E274", {"start": v(27.82, -100.24) * mm, "end": v(27.82, -92.72) * mm});
            skLineSegment(sketch, "E275", {"start": v(33.18, -111.67) * mm, "end": v(33.18, -73.76) * mm});
            skLineSegment(sketch, "E276", {"start": v(34.45, -111.67) * mm, "end": v(34.45, -73.76) * mm});
            skLineSegment(sketch, "E277", {"start": v(33.18, -131) * mm, "end": v(33.18, -111.67) * mm});
            skLineSegment(sketch, "E278", {"start": v(34.45, -131) * mm, "end": v(34.45, -111.67) * mm});
            skLineSegment(sketch, "E279", {"start": v(33.18, -73.76) * mm, "end": v(33.18, -54.44) * mm});
            skLineSegment(sketch, "E280", {"start": v(34.45, -73.76) * mm, "end": v(34.45, -54.44) * mm});
            skLineSegment(sketch, "E281", {"start": v(33.18, -51.22) * mm, "end": v(34.45, -51.22) * mm});
            skLineSegment(sketch, "E282", {"start": v(33.18, -54.44) * mm, "end": v(33.18, -51.22) * mm});
            skLineSegment(sketch, "E283", {"start": v(34.45, -54.44) * mm, "end": v(34.45, -51.22) * mm});
            skLineSegment(sketch, "E284", {"start": v(33.18, -134.21) * mm, "end": v(34.45, -134.21) * mm});
            skLineSegment(sketch, "E285", {"start": v(33.18, -134.21) * mm, "end": v(33.18, -131) * mm});
            skLineSegment(sketch, "E286", {"start": v(34.45, -134.21) * mm, "end": v(34.45, -131) * mm});
            skArc(sketch, "E287", {"start": v(38.26, -122.82) * mm, "mid": v(35.56, -123.93) * mm, "end": v(34.45, -126.63) * mm});
            skArc(sketch, "E288", {"start": v(34.45, -58.8) * mm, "mid": v(35.56, -61.5) * mm, "end": v(38.26, -62.62) * mm});
            skLineSegment(sketch, "E289", {"start": v(53.11, -116.47) * mm, "end": v(53.11, -118.05) * mm});
            skArc(sketch, "E290", {"start": v(48.35, -122.82) * mm, "mid": v(51.72, -121.42) * mm, "end": v(53.11, -118.05) * mm});
            skArc(sketch, "E291", {"start": v(53.11, -67.38) * mm, "mid": v(51.72, -64.01) * mm, "end": v(48.35, -62.62) * mm});
            skLineSegment(sketch, "E292", {"start": v(53.11, -67.38) * mm, "end": v(53.11, -68.97) * mm});
            skLineSegment(sketch, "E293", {"start": v(53.11, -105.87) * mm, "end": v(53.11, -116.47) * mm});
            skLineSegment(sketch, "E294", {"start": v(53.11, -68.97) * mm, "end": v(53.11, -87.3) * mm});
            skLineSegment(sketch, "E295", {"start": v(48.35, -62.62) * mm, "end": v(38.26, -62.62) * mm});
            skLineSegment(sketch, "E296", {"start": v(48.35, -122.82) * mm, "end": v(38.26, -122.82) * mm});
            skCircle(sketch, "E297", {"center": v(41.19, -74.97) * mm, "radius": 3.05 * mm});
            skLineSegment(sketch, "E298", {"start": v(35.57, -92.72) * mm, "end": v(37.49, -92.72) * mm});
            skArc(sketch, "E299", {"start": v(35.57, -81.67) * mm, "mid": v(34.53, -87.2) * mm, "end": v(35.57, -92.72) * mm});
            skLineSegment(sketch, "E300", {"start": v(35.57, -81.67) * mm, "end": v(37.49, -81.67) * mm});
            skArc(sketch, "E301", {"start": v(37.49, -92.72) * mm, "mid": v(38.53, -87.2) * mm, "end": v(37.49, -81.67) * mm});
            skArc(sketch, "E302", {"start": v(37.49, -103.77) * mm, "mid": v(38.53, -98.24) * mm, "end": v(37.49, -92.72) * mm});
            skLineSegment(sketch, "E303", {"start": v(38.54, -81.67) * mm, "end": v(37.49, -81.67) * mm});
            skLineSegment(sketch, "E304", {"start": v(37.49, -103.77) * mm, "end": v(38.55, -103.77) * mm});
            skLineSegment(sketch, "E305", {"start": v(38.68, -103.56) * mm, "end": v(38.68, -81.87) * mm});
            skLineSegment(sketch, "E306", {"start": v(35.57, -103.77) * mm, "end": v(37.49, -103.77) * mm});
            skArc(sketch, "E307", {"start": v(35.57, -92.72) * mm, "mid": v(34.53, -98.24) * mm, "end": v(35.57, -103.77) * mm});
            skLineSegment(sketch, "E308", {"start": v(35.57, -81.67) * mm, "end": v(34.52, -81.67) * mm});
            skLineSegment(sketch, "E309", {"start": v(34.52, -103.77) * mm, "end": v(35.57, -103.77) * mm});
            skLineSegment(sketch, "E310", {"start": v(60.88, -105.87) * mm, "end": v(56.29, -105.87) * mm});
            skLineSegment(sketch, "E311", {"start": v(60.88, -87.3) * mm, "end": v(60.88, -105.87) * mm});
            skLineSegment(sketch, "E312", {"start": v(56.29, -87.3) * mm, "end": v(60.88, -87.3) * mm});
            skArc(sketch, "E313", {"start": v(46.15, -104.28) * mm, "mid": v(46.62, -105.4) * mm, "end": v(47.74, -105.87) * mm});
            skLineSegment(sketch, "E314", {"start": v(46.15, -104.28) * mm, "end": v(46.15, -100.7) * mm});
            skLineSegment(sketch, "E315", {"start": v(56.29, -105.87) * mm, "end": v(51.06, -105.87) * mm});
            skLineSegment(sketch, "E316", {"start": v(49.06, -105.87) * mm, "end": v(47.74, -105.87) * mm});
            skLineSegment(sketch, "E317", {"start": v(51.48, -87.3) * mm, "end": v(56.29, -87.3) * mm});
            skLineSegment(sketch, "E318", {"start": v(57.88, -87.3) * mm, "end": v(57.88, -73.08) * mm});
            skLineSegment(sketch, "E319", {"start": v(60.88, -87.3) * mm, "end": v(60.88, -73.08) * mm});
            skArc(sketch, "E320", {"start": v(67.4, -106.52) * mm, "mid": v(66.94, -105.4) * mm, "end": v(65.81, -104.93) * mm});
            skArc(sketch, "E321", {"start": v(70.4, -106.52) * mm, "mid": v(69.06, -103.27) * mm, "end": v(65.81, -101.93) * mm});
            skLineSegment(sketch, "E322", {"start": v(67.4, -114.62) * mm, "end": v(67.4, -106.52) * mm});
            skLineSegment(sketch, "E323", {"start": v(70.4, -114.62) * mm, "end": v(70.4, -106.52) * mm});
            skLineSegment(sketch, "E324", {"start": v(67.4, -123.36) * mm, "end": v(70.4, -123.36) * mm});
            skLineSegment(sketch, "E325", {"start": v(67.4, -123.36) * mm, "end": v(67.4, -114.62) * mm});
            skLineSegment(sketch, "E326", {"start": v(70.4, -123.36) * mm, "end": v(70.4, -114.62) * mm});
            skLineSegment(sketch, "E327", {"start": v(65.81, -101.93) * mm, "end": v(62.46, -101.93) * mm});
            skLineSegment(sketch, "E328", {"start": v(65.81, -104.93) * mm, "end": v(62.46, -104.93) * mm});
            skArc(sketch, "E329", {"start": v(60.88, -100.34) * mm, "mid": v(61.34, -101.47) * mm, "end": v(62.46, -101.93) * mm});
            skArc(sketch, "E330", {"start": v(60.88, -104.65) * mm, "mid": v(61.66, -104.86) * mm, "end": v(62.46, -104.93) * mm});
            skLineSegment(sketch, "E331", {"start": v(71.71, -67.51) * mm, "end": v(71.71, -64.51) * mm});
            skLineSegment(sketch, "E332", {"start": v(66.75, -64.51) * mm, "end": v(71.71, -64.51) * mm});
            skLineSegment(sketch, "E333", {"start": v(66.75, -67.51) * mm, "end": v(71.71, -67.51) * mm});
            skLineSegment(sketch, "E334", {"start": v(62.46, -64.51) * mm, "end": v(66.75, -64.51) * mm});
            skLineSegment(sketch, "E335", {"start": v(62.46, -67.51) * mm, "end": v(66.75, -67.51) * mm});
            skArc(sketch, "E336", {"start": v(62.46, -64.51) * mm, "mid": v(59.22, -65.86) * mm, "end": v(57.88, -69.1) * mm});
            skArc(sketch, "E337", {"start": v(62.46, -67.51) * mm, "mid": v(61.34, -67.98) * mm, "end": v(60.88, -69.1) * mm});
            skLineSegment(sketch, "E338", {"start": v(57.88, -73.08) * mm, "end": v(57.88, -69.1) * mm});
            skLineSegment(sketch, "E339", {"start": v(60.88, -73.08) * mm, "end": v(60.88, -69.1) * mm});
            skArc(sketch, "E340", {"start": v(71.71, -64.51) * mm, "mid": v(72.45, -64.33) * mm, "end": v(73.02, -63.83) * mm});
            skLineSegment(sketch, "E341", {"start": v(75.48, -65.55) * mm, "end": v(73.02, -63.83) * mm});
            skArc(sketch, "E342", {"start": v(71.71, -67.51) * mm, "mid": v(73.84, -67) * mm, "end": v(75.48, -65.55) * mm});
            skLineSegment(sketch, "E343", {"start": v(73.3, -52.1) * mm, "end": v(76.3, -52.1) * mm});
            skLineSegment(sketch, "E344", {"start": v(73.3, -52.1) * mm, "end": v(73.3, -50.29) * mm});
            skLineSegment(sketch, "E345", {"start": v(76.3, -52.1) * mm, "end": v(76.3, -50.29) * mm});
            skLineSegment(sketch, "E346", {"start": v(73.3, -50.29) * mm, "end": v(73.3, -34.72) * mm});
            skLineSegment(sketch, "E347", {"start": v(76.3, -50.29) * mm, "end": v(76.3, -34.72) * mm});
            skLineSegment(sketch, "E348", {"start": v(76.3, -62.93) * mm, "end": v(73.3, -62.93) * mm});
            skArc(sketch, "E349", {"start": v(73.02, -63.83) * mm, "mid": v(73.23, -63.4) * mm, "end": v(73.3, -62.93) * mm});
            skArc(sketch, "E350", {"start": v(75.48, -65.55) * mm, "mid": v(76.09, -64.3) * mm, "end": v(76.3, -62.93) * mm});
            skLineSegment(sketch, "E351", {"start": v(73.3, -54.88) * mm, "end": v(73.3, -52.1) * mm});
            skLineSegment(sketch, "E352", {"start": v(76.3, -54.88) * mm, "end": v(76.3, -52.1) * mm});
            skLineSegment(sketch, "E353", {"start": v(73.3, -33.22) * mm, "end": v(76.3, -33.22) * mm});
            skLineSegment(sketch, "E354", {"start": v(73.3, -34.72) * mm, "end": v(73.3, -33.22) * mm});
            skLineSegment(sketch, "E355", {"start": v(76.3, -34.72) * mm, "end": v(76.3, -33.22) * mm});
            skLineSegment(sketch, "E356", {"start": v(73.3, -62.93) * mm, "end": v(73.3, -62.03) * mm});
            skLineSegment(sketch, "E357", {"start": v(76.3, -62.93) * mm, "end": v(76.3, -62.03) * mm});
            skLineSegment(sketch, "E358", {"start": v(73.3, -62.03) * mm, "end": v(73.3, -54.88) * mm});
            skLineSegment(sketch, "E359", {"start": v(76.3, -62.03) * mm, "end": v(76.3, -54.88) * mm});
            skLineSegment(sketch, "E360", {"start": v(57.88, -69.81) * mm, "end": v(57.13, -69.81) * mm});
            skLineSegment(sketch, "E361", {"start": v(55.82, -69.81) * mm, "end": v(55.46, -69.81) * mm});
            skLineSegment(sketch, "E362", {"start": v(54.14, -69.81) * mm, "end": v(53.11, -69.81) * mm});
            skLineSegment(sketch, "E363", {"start": v(43.34, -84.74) * mm, "end": v(42.78, -84.74) * mm});
            skLineSegment(sketch, "E364", {"start": v(42.94, -100.7) * mm, "end": v(42.97, -99.88) * mm});
            skLineSegment(sketch, "E365", {"start": v(42.97, -99.88) * mm, "end": v(43, -98.78) * mm});
            skLineSegment(sketch, "E366", {"start": v(43, -98.78) * mm, "end": v(43.04, -97.48) * mm});
            skLineSegment(sketch, "E367", {"start": v(43.04, -97.48) * mm, "end": v(43.07, -96.04) * mm});
            skLineSegment(sketch, "E368", {"start": v(43.07, -96.04) * mm, "end": v(43.1, -94.43) * mm});
            skLineSegment(sketch, "E369", {"start": v(43.1, -94.43) * mm, "end": v(43.14, -92.72) * mm});
            skLineSegment(sketch, "E370", {"start": v(43.14, -92.72) * mm, "end": v(43.17, -91) * mm});
            skLineSegment(sketch, "E371", {"start": v(43.17, -91) * mm, "end": v(43.2, -89.4) * mm});
            skLineSegment(sketch, "E372", {"start": v(43.2, -89.4) * mm, "end": v(43.24, -87.95) * mm});
            skLineSegment(sketch, "E373", {"start": v(43.24, -87.95) * mm, "end": v(43.27, -86.66) * mm});
            skLineSegment(sketch, "E374", {"start": v(43.27, -86.66) * mm, "end": v(43.3, -85.56) * mm});
            skLineSegment(sketch, "E375", {"start": v(43.3, -85.56) * mm, "end": v(43.34, -84.74) * mm});
            skLineSegment(sketch, "E376", {"start": v(42.44, -100.7) * mm, "end": v(42.94, -100.7) * mm});
            skLineSegment(sketch, "E377", {"start": v(42.44, -100.7) * mm, "end": v(42.46, -100.1) * mm});
            skLineSegment(sketch, "E378", {"start": v(42.46, -100.1) * mm, "end": v(42.48, -99.42) * mm});
            skLineSegment(sketch, "E379", {"start": v(42.48, -99.42) * mm, "end": v(42.51, -98) * mm});
            skLineSegment(sketch, "E380", {"start": v(42.51, -98) * mm, "end": v(42.54, -96.4) * mm});
            skLineSegment(sketch, "E381", {"start": v(42.54, -96.4) * mm, "end": v(42.57, -94.61) * mm});
            skLineSegment(sketch, "E382", {"start": v(42.57, -94.61) * mm, "end": v(42.6, -92.72) * mm});
            skLineSegment(sketch, "E383", {"start": v(42.6, -92.72) * mm, "end": v(42.64, -90.82) * mm});
            skLineSegment(sketch, "E384", {"start": v(42.64, -90.82) * mm, "end": v(42.68, -89.04) * mm});
            skLineSegment(sketch, "E385", {"start": v(42.68, -89.04) * mm, "end": v(42.7, -87.45) * mm});
            skLineSegment(sketch, "E386", {"start": v(42.7, -87.45) * mm, "end": v(42.74, -86.01) * mm});
            skLineSegment(sketch, "E387", {"start": v(42.74, -86.01) * mm, "end": v(42.76, -85.34) * mm});
            skLineSegment(sketch, "E388", {"start": v(42.76, -85.34) * mm, "end": v(42.78, -84.74) * mm});
            skLineSegment(sketch, "E389", {"start": v(43.83, -84.74) * mm, "end": v(43.34, -84.74) * mm});
            skLineSegment(sketch, "E390", {"start": v(43.5, -100.7) * mm, "end": v(43.52, -100.1) * mm});
            skLineSegment(sketch, "E391", {"start": v(43.52, -100.1) * mm, "end": v(43.54, -99.42) * mm});
            skLineSegment(sketch, "E392", {"start": v(43.54, -99.42) * mm, "end": v(43.57, -98) * mm});
            skLineSegment(sketch, "E393", {"start": v(43.57, -98) * mm, "end": v(43.6, -96.4) * mm});
            skLineSegment(sketch, "E394", {"start": v(43.6, -96.4) * mm, "end": v(43.63, -94.61) * mm});
            skLineSegment(sketch, "E395", {"start": v(43.63, -94.61) * mm, "end": v(43.67, -92.72) * mm});
            skLineSegment(sketch, "E396", {"start": v(43.67, -92.72) * mm, "end": v(43.7, -90.82) * mm});
            skLineSegment(sketch, "E397", {"start": v(43.7, -90.82) * mm, "end": v(43.74, -89.04) * mm});
            skLineSegment(sketch, "E398", {"start": v(43.74, -89.04) * mm, "end": v(43.77, -87.45) * mm});
            skLineSegment(sketch, "E399", {"start": v(43.77, -87.45) * mm, "end": v(43.8, -86.01) * mm});
            skLineSegment(sketch, "E400", {"start": v(43.8, -86.01) * mm, "end": v(43.82, -85.34) * mm});
            skLineSegment(sketch, "E401", {"start": v(43.82, -85.34) * mm, "end": v(43.83, -84.74) * mm});
            skLineSegment(sketch, "E402", {"start": v(42.94, -100.7) * mm, "end": v(43.5, -100.7) * mm});
            skLineSegment(sketch, "E403", {"start": v(44.4, -84.74) * mm, "end": v(43.83, -84.74) * mm});
            skLineSegment(sketch, "E404", {"start": v(43.5, -100.7) * mm, "end": v(44, -100.7) * mm});
            skLineSegment(sketch, "E405", {"start": v(42.28, -84.74) * mm, "end": v(41.72, -84.74) * mm});
            skLineSegment(sketch, "E406", {"start": v(41.88, -100.7) * mm, "end": v(41.91, -99.88) * mm});
            skLineSegment(sketch, "E407", {"start": v(41.91, -99.88) * mm, "end": v(41.95, -98.78) * mm});
            skLineSegment(sketch, "E408", {"start": v(41.95, -98.78) * mm, "end": v(41.98, -97.48) * mm});
            skLineSegment(sketch, "E409", {"start": v(41.98, -97.48) * mm, "end": v(42.01, -96.04) * mm});
            skLineSegment(sketch, "E410", {"start": v(42.01, -96.04) * mm, "end": v(42.04, -94.43) * mm});
            skLineSegment(sketch, "E411", {"start": v(42.04, -94.43) * mm, "end": v(42.08, -92.72) * mm});
            skLineSegment(sketch, "E412", {"start": v(42.08, -92.72) * mm, "end": v(42.11, -91) * mm});
            skLineSegment(sketch, "E413", {"start": v(42.11, -91) * mm, "end": v(42.15, -89.4) * mm});
            skLineSegment(sketch, "E414", {"start": v(42.15, -89.4) * mm, "end": v(42.18, -87.95) * mm});
            skLineSegment(sketch, "E415", {"start": v(42.18, -87.95) * mm, "end": v(42.2, -86.66) * mm});
            skLineSegment(sketch, "E416", {"start": v(42.2, -86.66) * mm, "end": v(42.24, -85.56) * mm});
            skLineSegment(sketch, "E417", {"start": v(42.24, -85.56) * mm, "end": v(42.28, -84.74) * mm});
            skLineSegment(sketch, "E418", {"start": v(41.38, -100.7) * mm, "end": v(41.88, -100.7) * mm});
            skLineSegment(sketch, "E419", {"start": v(41.38, -100.7) * mm, "end": v(41.4, -100.1) * mm});
            skLineSegment(sketch, "E420", {"start": v(41.4, -100.1) * mm, "end": v(41.42, -99.42) * mm});
            skLineSegment(sketch, "E421", {"start": v(41.42, -99.42) * mm, "end": v(41.45, -98) * mm});
            skLineSegment(sketch, "E422", {"start": v(41.45, -98) * mm, "end": v(41.48, -96.4) * mm});
            skLineSegment(sketch, "E423", {"start": v(41.48, -96.4) * mm, "end": v(41.52, -94.61) * mm});
            skLineSegment(sketch, "E424", {"start": v(41.52, -94.61) * mm, "end": v(41.55, -92.72) * mm});
            skLineSegment(sketch, "E425", {"start": v(41.55, -92.72) * mm, "end": v(41.59, -90.82) * mm});
            skLineSegment(sketch, "E426", {"start": v(41.59, -90.82) * mm, "end": v(41.62, -89.04) * mm});
            skLineSegment(sketch, "E427", {"start": v(41.62, -89.04) * mm, "end": v(41.65, -87.45) * mm});
            skLineSegment(sketch, "E428", {"start": v(41.65, -87.45) * mm, "end": v(41.68, -86.01) * mm});
            skLineSegment(sketch, "E429", {"start": v(41.68, -86.01) * mm, "end": v(41.7, -85.34) * mm});
            skLineSegment(sketch, "E430", {"start": v(41.7, -85.34) * mm, "end": v(41.72, -84.74) * mm});
            skLineSegment(sketch, "E431", {"start": v(41.22, -84.74) * mm, "end": v(40.66, -84.74) * mm});
            skLineSegment(sketch, "E432", {"start": v(40.82, -100.7) * mm, "end": v(40.86, -99.88) * mm});
            skLineSegment(sketch, "E433", {"start": v(40.86, -99.88) * mm, "end": v(40.9, -98.78) * mm});
            skLineSegment(sketch, "E434", {"start": v(40.9, -98.78) * mm, "end": v(40.92, -97.48) * mm});
            skLineSegment(sketch, "E435", {"start": v(40.92, -97.48) * mm, "end": v(40.95, -96.04) * mm});
            skLineSegment(sketch, "E436", {"start": v(40.95, -96.04) * mm, "end": v(40.99, -94.43) * mm});
            skLineSegment(sketch, "E437", {"start": v(40.99, -94.43) * mm, "end": v(41.02, -92.72) * mm});
            skLineSegment(sketch, "E438", {"start": v(41.02, -92.72) * mm, "end": v(41.06, -91) * mm});
            skLineSegment(sketch, "E439", {"start": v(41.06, -91) * mm, "end": v(41.09, -89.4) * mm});
            skLineSegment(sketch, "E440", {"start": v(41.09, -89.4) * mm, "end": v(41.12, -87.95) * mm});
            skLineSegment(sketch, "E441", {"start": v(41.12, -87.95) * mm, "end": v(41.15, -86.66) * mm});
            skLineSegment(sketch, "E442", {"start": v(41.15, -86.66) * mm, "end": v(41.19, -85.56) * mm});
            skLineSegment(sketch, "E443", {"start": v(41.19, -85.56) * mm, "end": v(41.22, -84.74) * mm});
            skLineSegment(sketch, "E444", {"start": v(40.33, -100.7) * mm, "end": v(40.82, -100.7) * mm});
            skLineSegment(sketch, "E445", {"start": v(40.33, -100.7) * mm, "end": v(40.34, -100.1) * mm});
            skLineSegment(sketch, "E446", {"start": v(40.34, -100.1) * mm, "end": v(40.36, -99.42) * mm});
            skLineSegment(sketch, "E447", {"start": v(40.36, -99.42) * mm, "end": v(40.4, -98) * mm});
            skLineSegment(sketch, "E448", {"start": v(40.4, -98) * mm, "end": v(40.42, -96.4) * mm});
            skLineSegment(sketch, "E449", {"start": v(40.42, -96.4) * mm, "end": v(40.46, -94.61) * mm});
            skLineSegment(sketch, "E450", {"start": v(40.46, -94.61) * mm, "end": v(40.5, -92.72) * mm});
            skLineSegment(sketch, "E451", {"start": v(40.5, -92.72) * mm, "end": v(40.53, -90.82) * mm});
            skLineSegment(sketch, "E452", {"start": v(40.53, -90.82) * mm, "end": v(40.56, -89.04) * mm});
            skLineSegment(sketch, "E453", {"start": v(40.56, -89.04) * mm, "end": v(40.6, -87.45) * mm});
            skLineSegment(sketch, "E454", {"start": v(40.6, -87.45) * mm, "end": v(40.62, -86.01) * mm});
            skLineSegment(sketch, "E455", {"start": v(40.62, -86.01) * mm, "end": v(40.64, -85.34) * mm});
            skLineSegment(sketch, "E456", {"start": v(40.64, -85.34) * mm, "end": v(40.66, -84.74) * mm});
            skLineSegment(sketch, "E457", {"start": v(42.78, -84.74) * mm, "end": v(42.28, -84.74) * mm});
            skLineSegment(sketch, "E458", {"start": v(41.88, -100.7) * mm, "end": v(42.44, -100.7) * mm});
            skLineSegment(sketch, "E459", {"start": v(41.72, -84.74) * mm, "end": v(41.22, -84.74) * mm});
            skLineSegment(sketch, "E460", {"start": v(40.82, -100.7) * mm, "end": v(41.38, -100.7) * mm});
            skLineSegment(sketch, "E461", {"start": v(40.16, -84.74) * mm, "end": v(39.6, -84.74) * mm});
            skLineSegment(sketch, "E462", {"start": v(39.76, -100.7) * mm, "end": v(39.8, -99.88) * mm});
            skLineSegment(sketch, "E463", {"start": v(39.8, -99.88) * mm, "end": v(39.83, -98.78) * mm});
            skLineSegment(sketch, "E464", {"start": v(39.83, -98.78) * mm, "end": v(39.87, -97.48) * mm});
            skLineSegment(sketch, "E465", {"start": v(39.87, -97.48) * mm, "end": v(39.9, -96.04) * mm});
            skLineSegment(sketch, "E466", {"start": v(39.9, -96.04) * mm, "end": v(39.93, -94.43) * mm});
            skLineSegment(sketch, "E467", {"start": v(39.93, -94.43) * mm, "end": v(39.96, -92.72) * mm});
            skLineSegment(sketch, "E468", {"start": v(39.96, -92.72) * mm, "end": v(40, -91) * mm});
            skLineSegment(sketch, "E469", {"start": v(40, -91) * mm, "end": v(40.03, -89.4) * mm});
            skLineSegment(sketch, "E470", {"start": v(40.03, -89.4) * mm, "end": v(40.06, -87.95) * mm});
            skLineSegment(sketch, "E471", {"start": v(40.06, -87.95) * mm, "end": v(40.1, -86.66) * mm});
            skLineSegment(sketch, "E472", {"start": v(40.1, -86.66) * mm, "end": v(40.13, -85.56) * mm});
            skLineSegment(sketch, "E473", {"start": v(40.13, -85.56) * mm, "end": v(40.16, -84.74) * mm});
            skLineSegment(sketch, "E474", {"start": v(39.27, -100.7) * mm, "end": v(39.76, -100.7) * mm});
            skLineSegment(sketch, "E475", {"start": v(39.27, -100.7) * mm, "end": v(39.29, -100.1) * mm});
            skLineSegment(sketch, "E476", {"start": v(39.29, -100.1) * mm, "end": v(39.3, -99.42) * mm});
            skLineSegment(sketch, "E477", {"start": v(39.3, -99.42) * mm, "end": v(39.34, -98) * mm});
            skLineSegment(sketch, "E478", {"start": v(39.34, -98) * mm, "end": v(39.37, -96.4) * mm});
            skLineSegment(sketch, "E479", {"start": v(39.37, -96.4) * mm, "end": v(39.4, -94.61) * mm});
            skLineSegment(sketch, "E480", {"start": v(39.4, -94.61) * mm, "end": v(39.43, -92.72) * mm});
            skLineSegment(sketch, "E481", {"start": v(39.43, -92.72) * mm, "end": v(39.47, -90.82) * mm});
            skLineSegment(sketch, "E482", {"start": v(39.47, -90.82) * mm, "end": v(39.5, -89.04) * mm});
            skLineSegment(sketch, "E483", {"start": v(39.5, -89.04) * mm, "end": v(39.53, -87.45) * mm});
            skLineSegment(sketch, "E484", {"start": v(39.53, -87.45) * mm, "end": v(39.56, -86.01) * mm});
            skLineSegment(sketch, "E485", {"start": v(39.56, -86.01) * mm, "end": v(39.58, -85.34) * mm});
            skLineSegment(sketch, "E486", {"start": v(39.58, -85.34) * mm, "end": v(39.6, -84.74) * mm});
            skLineSegment(sketch, "E487", {"start": v(39.6, -84.74) * mm, "end": v(39.1, -84.74) * mm});
            skLineSegment(sketch, "E488", {"start": v(38.7, -100.7) * mm, "end": v(39.27, -100.7) * mm});
            skLineSegment(sketch, "E489", {"start": v(38.7, -100.7) * mm, "end": v(38.74, -99.88) * mm});
            skLineSegment(sketch, "E490", {"start": v(38.74, -99.88) * mm, "end": v(38.77, -98.78) * mm});
            skLineSegment(sketch, "E491", {"start": v(38.77, -98.78) * mm, "end": v(38.8, -97.48) * mm});
            skLineSegment(sketch, "E492", {"start": v(38.8, -97.48) * mm, "end": v(38.84, -96.04) * mm});
            skLineSegment(sketch, "E493", {"start": v(38.84, -96.04) * mm, "end": v(38.87, -94.43) * mm});
            skLineSegment(sketch, "E494", {"start": v(38.87, -94.43) * mm, "end": v(38.9, -92.72) * mm});
            skLineSegment(sketch, "E495", {"start": v(38.9, -92.72) * mm, "end": v(38.94, -91) * mm});
            skLineSegment(sketch, "E496", {"start": v(38.94, -91) * mm, "end": v(38.97, -89.4) * mm});
            skLineSegment(sketch, "E497", {"start": v(38.97, -89.4) * mm, "end": v(39, -87.95) * mm});
            skLineSegment(sketch, "E498", {"start": v(39, -87.95) * mm, "end": v(39.03, -86.66) * mm});
            skLineSegment(sketch, "E499", {"start": v(39.03, -86.66) * mm, "end": v(39.07, -85.56) * mm});
            skLineSegment(sketch, "E500", {"start": v(39.07, -85.56) * mm, "end": v(39.1, -84.74) * mm});
            skLineSegment(sketch, "E501", {"start": v(40.66, -84.74) * mm, "end": v(40.16, -84.74) * mm});
            skLineSegment(sketch, "E502", {"start": v(39.76, -100.7) * mm, "end": v(40.33, -100.7) * mm});
            skLineSegment(sketch, "E503", {"start": v(39.1, -84.74) * mm, "end": v(38.68, -84.74) * mm});
            skLineSegment(sketch, "E504", {"start": v(44.47, -84.74) * mm, "end": v(44.4, -84.74) * mm});
            skLineSegment(sketch, "E505", {"start": v(44.05, -100.7) * mm, "end": v(44.1, -99.86) * mm});
            skLineSegment(sketch, "E506", {"start": v(44.1, -99.86) * mm, "end": v(44.13, -98.7) * mm});
            skLineSegment(sketch, "E507", {"start": v(44.13, -98.7) * mm, "end": v(44.16, -97.42) * mm});
            skLineSegment(sketch, "E508", {"start": v(44.16, -97.42) * mm, "end": v(44.2, -96) * mm});
            skLineSegment(sketch, "E509", {"start": v(44.2, -96) * mm, "end": v(44.22, -94.4) * mm});
            skLineSegment(sketch, "E510", {"start": v(44.22, -94.4) * mm, "end": v(44.26, -92.72) * mm});
            skLineSegment(sketch, "E511", {"start": v(44.26, -92.72) * mm, "end": v(44.3, -91.03) * mm});
            skLineSegment(sketch, "E512", {"start": v(44.3, -91.03) * mm, "end": v(44.33, -89.43) * mm});
            skLineSegment(sketch, "E513", {"start": v(44.33, -89.43) * mm, "end": v(44.36, -88.01) * mm});
            skLineSegment(sketch, "E514", {"start": v(44.36, -88.01) * mm, "end": v(44.39, -86.73) * mm});
            skLineSegment(sketch, "E515", {"start": v(44.39, -86.73) * mm, "end": v(44.43, -85.57) * mm});
            skLineSegment(sketch, "E516", {"start": v(44.43, -85.57) * mm, "end": v(44.47, -84.74) * mm});
            skLineSegment(sketch, "E517", {"start": v(44, -100.7) * mm, "end": v(44.05, -100.7) * mm});
            skLineSegment(sketch, "E518", {"start": v(44.47, -84.74) * mm, "end": v(48.06, -84.74) * mm});
            skLineSegment(sketch, "E519", {"start": v(48.06, -100.7) * mm, "end": v(48.06, -100.36) * mm});
            skLineSegment(sketch, "E520", {"start": v(48.06, -96.44) * mm, "end": v(48.06, -88.9) * mm});
            skLineSegment(sketch, "E521", {"start": v(48.06, -85.26) * mm, "end": v(48.06, -84.74) * mm});
            skLineSegment(sketch, "E522", {"start": v(48.06, -100.7) * mm, "end": v(44.05, -100.7) * mm});
            skLineSegment(sketch, "E523", {"start": v(49.06, -90.56) * mm, "end": v(48.06, -90.56) * mm});
            skLineSegment(sketch, "E524", {"start": v(49.06, -94.88) * mm, "end": v(48.06, -94.88) * mm});
            skLineSegment(sketch, "E525", {"start": v(49.06, -100.65) * mm, "end": v(48.06, -100.65) * mm});
            skLineSegment(sketch, "E526", {"start": v(48.06, -100.36) * mm, "end": v(48.06, -96.44) * mm});
            skLineSegment(sketch, "E527", {"start": v(49.06, -84.84) * mm, "end": v(48.06, -84.84) * mm});
            skLineSegment(sketch, "E528", {"start": v(48.06, -88.9) * mm, "end": v(48.06, -85.26) * mm});
            skArc(sketch, "E529", {"start": v(57.16, -70.76) * mm, "mid": v(56.48, -70.04) * mm, "end": v(55.76, -70.71) * mm});
            skLineSegment(sketch, "E530", {"start": v(51.06, -103.97) * mm, "end": v(49.06, -103.97) * mm});
            skLineSegment(sketch, "E531", {"start": v(51.06, -108.6) * mm, "end": v(51.06, -103.97) * mm});
            skLineSegment(sketch, "E532", {"start": v(49.06, -108.6) * mm, "end": v(49.06, -103.97) * mm});
            skLineSegment(sketch, "E533", {"start": v(51.06, -88.22) * mm, "end": v(49.06, -88.22) * mm});
            skLineSegment(sketch, "E534", {"start": v(49.06, -103.97) * mm, "end": v(49.06, -88.22) * mm});
            skLineSegment(sketch, "E535", {"start": v(51.06, -103.97) * mm, "end": v(51.06, -88.22) * mm});
            skLineSegment(sketch, "E536", {"start": v(49.06, -88.22) * mm, "end": v(49.06, -83.6) * mm});
            skLineSegment(sketch, "E537", {"start": v(51.06, -88.22) * mm, "end": v(51.06, -83.6) * mm});
            skLineSegment(sketch, "E538", {"start": v(31.36, -104.45) * mm, "end": v(33, -105.4) * mm});
            skLineSegment(sketch, "E539", {"start": v(31.36, -104.45) * mm, "end": v(31.66, -103.94) * mm});
            skLineSegment(sketch, "E540", {"start": v(33, -105.4) * mm, "end": v(33.18, -105.07) * mm});
            skLineSegment(sketch, "E541", {"start": v(28.15, -100.66) * mm, "end": v(28.15, -84.78) * mm});
            skLineSegment(sketch, "E542", {"start": v(63.42, -80.59) * mm, "end": v(63.42, -72.98) * mm});
            skLineSegment(sketch, "E543", {"start": v(63.42, -87.6) * mm, "end": v(63.42, -80.59) * mm});
            skLineSegment(sketch, "E544", {"start": v(55.11, -71.82) * mm, "end": v(55.52, -72.73) * mm});
            skLineSegment(sketch, "E545", {"start": v(28.07, -92.72) * mm, "end": v(28.07, -100.5) * mm});
            skLineSegment(sketch, "E546", {"start": v(28.07, -84.95) * mm, "end": v(28.07, -92.72) * mm});
            skLineSegment(sketch, "E547", {"start": v(33.18, -111.67) * mm, "end": v(34.45, -111.67) * mm});
            skLineSegment(sketch, "E548", {"start": v(33.18, -73.76) * mm, "end": v(34.45, -73.76) * mm});
            skLineSegment(sketch, "E549", {"start": v(33.18, -131) * mm, "end": v(34.45, -131) * mm});
            skLineSegment(sketch, "E550", {"start": v(33.18, -54.44) * mm, "end": v(34.45, -54.44) * mm});
            skLineSegment(sketch, "E551", {"start": v(34.45, -68.97) * mm, "end": v(38.26, -68.97) * mm});
            skLineSegment(sketch, "E552", {"start": v(38.26, -68.97) * mm, "end": v(38.26, -74.14) * mm});
            skLineSegment(sketch, "E553", {"start": v(38.26, -75.8) * mm, "end": v(38.26, -81.67) * mm});
            skLineSegment(sketch, "E554", {"start": v(38.26, -103.77) * mm, "end": v(38.26, -116.47) * mm});
            skLineSegment(sketch, "E555", {"start": v(34.45, -116.47) * mm, "end": v(38.26, -116.47) * mm});
            skLineSegment(sketch, "E556", {"start": v(38.26, -116.47) * mm, "end": v(38.26, -122.82) * mm});
            skLineSegment(sketch, "E557", {"start": v(38.26, -62.62) * mm, "end": v(38.26, -68.97) * mm});
            skLineSegment(sketch, "E558", {"start": v(48.35, -122.82) * mm, "end": v(48.35, -116.47) * mm});
            skLineSegment(sketch, "E559", {"start": v(53.11, -116.47) * mm, "end": v(48.35, -116.47) * mm});
            skLineSegment(sketch, "E560", {"start": v(48.35, -68.97) * mm, "end": v(48.35, -62.62) * mm});
            skLineSegment(sketch, "E561", {"start": v(48.35, -68.97) * mm, "end": v(53.11, -68.97) * mm});
            skLineSegment(sketch, "E562", {"start": v(48.35, -116.47) * mm, "end": v(48.35, -105.87) * mm});
            skLineSegment(sketch, "E563", {"start": v(48.35, -84.84) * mm, "end": v(48.35, -68.97) * mm});
            skLineSegment(sketch, "E564", {"start": v(48.35, -68.97) * mm, "end": v(38.26, -68.97) * mm});
            skLineSegment(sketch, "E565", {"start": v(48.35, -116.47) * mm, "end": v(38.26, -116.47) * mm});
            skLineSegment(sketch, "E566", {"start": v(56.29, -87.3) * mm, "end": v(56.29, -105.87) * mm});
            skLineSegment(sketch, "E567", {"start": v(57.88, -73.08) * mm, "end": v(60.88, -73.08) * mm});
            skLineSegment(sketch, "E568", {"start": v(65.81, -101.93) * mm, "end": v(65.81, -104.93) * mm});
            skLineSegment(sketch, "E569", {"start": v(70.4, -106.52) * mm, "end": v(67.4, -106.52) * mm});
            skLineSegment(sketch, "E570", {"start": v(67.4, -114.62) * mm, "end": v(70.4, -114.62) * mm});
            skLineSegment(sketch, "E571", {"start": v(62.46, -104.93) * mm, "end": v(62.46, -101.93) * mm});
            skLineSegment(sketch, "E572", {"start": v(66.75, -64.51) * mm, "end": v(66.75, -67.51) * mm});
            skLineSegment(sketch, "E573", {"start": v(62.46, -64.51) * mm, "end": v(62.46, -67.51) * mm});
            skLineSegment(sketch, "E574", {"start": v(57.88, -69.1) * mm, "end": v(60.88, -69.1) * mm});
            skLineSegment(sketch, "E575", {"start": v(73.3, -50.29) * mm, "end": v(76.3, -50.29) * mm});
            skLineSegment(sketch, "E576", {"start": v(73.3, -34.72) * mm, "end": v(76.3, -34.72) * mm});
            skLineSegment(sketch, "E577", {"start": v(73.3, -54.88) * mm, "end": v(76.3, -54.88) * mm});
            skLineSegment(sketch, "E578", {"start": v(73.3, -62.03) * mm, "end": v(76.3, -62.03) * mm});
            skLineSegment(sketch, "E579", {"start": v(44, -100.7) * mm, "end": v(44.03, -99.88) * mm});
            skLineSegment(sketch, "E580", {"start": v(44.03, -99.88) * mm, "end": v(44.07, -98.78) * mm});
            skLineSegment(sketch, "E581", {"start": v(44.07, -98.78) * mm, "end": v(44.1, -97.48) * mm});
            skLineSegment(sketch, "E582", {"start": v(44.1, -97.48) * mm, "end": v(44.13, -96.04) * mm});
            skLineSegment(sketch, "E583", {"start": v(44.13, -96.04) * mm, "end": v(44.16, -94.43) * mm});
            skLineSegment(sketch, "E584", {"start": v(44.16, -94.43) * mm, "end": v(44.2, -92.72) * mm});
            skLineSegment(sketch, "E585", {"start": v(44.2, -92.72) * mm, "end": v(44.23, -91) * mm});
            skLineSegment(sketch, "E586", {"start": v(44.23, -91) * mm, "end": v(44.26, -89.4) * mm});
            skLineSegment(sketch, "E587", {"start": v(44.26, -89.4) * mm, "end": v(44.3, -87.95) * mm});
            skLineSegment(sketch, "E588", {"start": v(44.3, -87.95) * mm, "end": v(44.33, -86.66) * mm});
            skLineSegment(sketch, "E589", {"start": v(44.33, -86.66) * mm, "end": v(44.36, -85.56) * mm});
            skLineSegment(sketch, "E590", {"start": v(44.36, -85.56) * mm, "end": v(44.4, -84.74) * mm});
            skLineSegment(sketch, "E591", {"start": v(32.37, -104.1) * mm, "end": v(32.37, -81.33) * mm});
            skLineSegment(sketch, "E592", {"start": v(62.78, -80.62) * mm, "end": v(62.78, -72.34) * mm});
            skLineSegment(sketch, "E593", {"start": v(62.78, -88.24) * mm, "end": v(62.78, -80.62) * mm});
            skLineSegment(sketch, "E594", {"start": v(61.51, -80.62) * mm, "end": v(61.51, -72.34) * mm});
            skLineSegment(sketch, "E595", {"start": v(61.51, -88.24) * mm, "end": v(61.51, -80.62) * mm});
            skLineSegment(sketch, "E596", {"start": v(0, 5) * mm, "end": v(0, 5.55) * mm});
            skLineSegment(sketch, "E597", {"start": v(-5, 0) * mm, "end": v(-5.55, 0) * mm});
            skLineSegment(sketch, "E598", {"start": v(0, -5) * mm, "end": v(0, -5.55) * mm});
            skLineSegment(sketch, "E599", {"start": v(5, 0) * mm, "end": v(5.55, 0) * mm});
            skLineSegment(sketch, "E600", {"start": v(-30.66, -1.1) * mm, "end": v(-30.66, -1.16) * mm});
            skLineSegment(sketch, "E601", {"start": v(-15.12, -1.16) * mm, "end": v(-15.12, -1.1) * mm});
            skArc(sketch, "E602", {"start": v(-15.37, -1.42) * mm, "mid": v(-15.2, -1.34) * mm, "end": v(-15.12, -1.16) * mm});
            skArc(sketch, "E603", {"start": v(-30.66, -1.16) * mm, "mid": v(-30.59, -1.34) * mm, "end": v(-30.4, -1.42) * mm});
            skArc(sketch, "E604", {"start": v(-27.16, 22.45) * mm, "mid": v(-28.18, 22.3) * mm, "end": v(-29.1, 21.82) * mm});
            skArc(sketch, "E605", {"start": v(-16.7, 21.82) * mm, "mid": v(-17.6, 22.3) * mm, "end": v(-18.62, 22.45) * mm});
            skLineSegment(sketch, "E606", {"start": v(-18.62, 22.45) * mm, "end": v(-27.16, 22.45) * mm});
            skLineSegment(sketch, "E607", {"start": v(-64.69, 23.88) * mm, "end": v(-66.14, 24.72) * mm});
            skLineSegment(sketch, "E608", {"start": v(-81.1, 24.83) * mm, "end": v(-82.75, 23.88) * mm});
            skArc(sketch, "E609", {"start": v(-80.38, 25.15) * mm, "mid": v(-80.75, 25) * mm, "end": v(-81.1, 24.83) * mm});
            skLineSegment(sketch, "E610", {"start": v(-3.98, 3.94) * mm, "end": v(-3.98, 5.2) * mm});
            skLineSegment(sketch, "E611", {"start": v(-103.5, 20.83) * mm, "end": v(-103.53, 20.74) * mm});
            skLineSegment(sketch, "E612", {"start": v(-103.53, 20.74) * mm, "end": v(-103.54, 20.72) * mm});
            skArc(sketch, "E613", {"start": v(-43.9, 20.72) * mm, "mid": v(-43.9, 20.75) * mm, "end": v(-43.92, 20.78) * mm});
            skLineSegment(sketch, "E614", {"start": v(-43.62, 8.9) * mm, "end": v(-41.97, 8.9) * mm});
            skLineSegment(sketch, "E615", {"start": v(-41.97, 15) * mm, "end": v(-43.62, 15) * mm});
            skLineSegment(sketch, "E616", {"start": v(-106.06, 9.92) * mm, "end": v(-103.82, 9.92) * mm});
            skLineSegment(sketch, "E617", {"start": v(-103.82, 13.98) * mm, "end": v(-105.84, 13.98) * mm});
            skLineSegment(sketch, "E618", {"start": v(-81.62, 28.64) * mm, "end": v(-81.62, 27.93) * mm});
            skLineSegment(sketch, "E619", {"start": v(-65.81, 26.1) * mm, "end": v(-65.81, 26.47) * mm});
            skLineSegment(sketch, "E620", {"start": v(-65.81, 27.87) * mm, "end": v(-65.81, 28.64) * mm});
            skLineSegment(sketch, "E621", {"start": v(-10.13, 8.25) * mm, "end": v(-12.05, 9.44) * mm});
            skLineSegment(sketch, "E622", {"start": v(-33.73, 9.44) * mm, "end": v(-35.65, 8.25) * mm});
            skLineSegment(sketch, "E623", {"start": v(-35.65, 6.34) * mm, "end": v(-33.84, 5.2) * mm});
            skLineSegment(sketch, "E624", {"start": v(-11.94, 5.2) * mm, "end": v(-10.13, 6.34) * mm});
            skLineSegment(sketch, "E625", {"start": v(-66.6, 44.06) * mm, "end": v(-66.6, 47.06) * mm});
            skLineSegment(sketch, "E626", {"start": v(-31.5, 13.37) * mm, "end": v(-31.95, 13.11) * mm});
            skLineSegment(sketch, "E627", {"start": v(-31.95, 13.11) * mm, "end": v(-32.41, 12.85) * mm});
            skLineSegment(sketch, "E628", {"start": v(-13.37, 12.32) * mm, "end": v(-13.83, 12.59) * mm});
            skLineSegment(sketch, "E629", {"start": v(-13.83, 12.59) * mm, "end": v(-14.29, 12.85) * mm});
            skLineSegment(sketch, "E630", {"start": v(-31.5, 14.43) * mm, "end": v(-31.95, 14.17) * mm});
            skLineSegment(sketch, "E631", {"start": v(-31.95, 14.17) * mm, "end": v(-32.41, 13.9) * mm});
            skLineSegment(sketch, "E632", {"start": v(-32.41, 13.9) * mm, "end": v(-31.95, 13.63) * mm});
            skLineSegment(sketch, "E633", {"start": v(-31.95, 13.63) * mm, "end": v(-31.5, 13.37) * mm});
            skLineSegment(sketch, "E634", {"start": v(-13.37, 14.44) * mm, "end": v(-13.83, 14.7) * mm});
            skLineSegment(sketch, "E635", {"start": v(-13.83, 14.7) * mm, "end": v(-14.29, 14.97) * mm});
            skLineSegment(sketch, "E636", {"start": v(-13.37, 13.38) * mm, "end": v(-13.83, 13.64) * mm});
            skLineSegment(sketch, "E637", {"start": v(-13.83, 13.64) * mm, "end": v(-14.29, 13.9) * mm});
            skLineSegment(sketch, "E638", {"start": v(-32.41, 14.95) * mm, "end": v(-31.95, 14.69) * mm});
            skLineSegment(sketch, "E639", {"start": v(-31.95, 14.69) * mm, "end": v(-31.5, 14.42) * mm});
            skLineSegment(sketch, "E640", {"start": v(-31.5, 11.26) * mm, "end": v(-31.95, 11) * mm});
            skLineSegment(sketch, "E641", {"start": v(-31.95, 11) * mm, "end": v(-32.41, 10.73) * mm});
            skLineSegment(sketch, "E642", {"start": v(-32.41, 10.72) * mm, "end": v(-31.95, 10.46) * mm});
            skLineSegment(sketch, "E643", {"start": v(-31.95, 10.46) * mm, "end": v(-31.5, 10.2) * mm});
            skLineSegment(sketch, "E644", {"start": v(-13.37, 11.26) * mm, "end": v(-13.83, 11.53) * mm});
            skLineSegment(sketch, "E645", {"start": v(-13.83, 11.53) * mm, "end": v(-14.29, 11.8) * mm});
            skLineSegment(sketch, "E646", {"start": v(-32.41, 12.84) * mm, "end": v(-31.95, 12.57) * mm});
            skLineSegment(sketch, "E647", {"start": v(-31.95, 12.57) * mm, "end": v(-31.5, 12.3) * mm});
            skLineSegment(sketch, "E648", {"start": v(-13.37, 10.2) * mm, "end": v(-13.83, 10.47) * mm});
            skLineSegment(sketch, "E649", {"start": v(-13.83, 10.47) * mm, "end": v(-14.29, 10.73) * mm});
            skLineSegment(sketch, "E650", {"start": v(-31.5, 12.31) * mm, "end": v(-31.95, 12.06) * mm});
            skLineSegment(sketch, "E651", {"start": v(-31.95, 12.06) * mm, "end": v(-32.41, 11.8) * mm});
            skLineSegment(sketch, "E652", {"start": v(-32.41, 11.78) * mm, "end": v(-31.95, 11.51) * mm});
            skLineSegment(sketch, "E653", {"start": v(-31.95, 11.51) * mm, "end": v(-31.5, 11.25) * mm});
            skLineSegment(sketch, "E654", {"start": v(-31.5, 10.2) * mm, "end": v(-31.95, 9.94) * mm});
            skLineSegment(sketch, "E655", {"start": v(-31.95, 9.94) * mm, "end": v(-32.41, 9.67) * mm});
            skLineSegment(sketch, "E656", {"start": v(-13.89, 9.44) * mm, "end": v(-14.29, 9.68) * mm});
            skLineSegment(sketch, "E657", {"start": v(-32.41, 9.66) * mm, "end": v(-32.03, 9.44) * mm});
            skLineSegment(sketch, "E658", {"start": v(-14.28, 11.79) * mm, "end": v(-13.83, 12.04) * mm});
            skLineSegment(sketch, "E659", {"start": v(-13.83, 12.04) * mm, "end": v(-13.37, 12.3) * mm});
            skLineSegment(sketch, "E660", {"start": v(-14.28, 13.9) * mm, "end": v(-13.83, 14.16) * mm});
            skLineSegment(sketch, "E661", {"start": v(-13.83, 14.16) * mm, "end": v(-13.37, 14.43) * mm});
            skLineSegment(sketch, "E662", {"start": v(-31.5, 15.5) * mm, "end": v(-31.95, 15.23) * mm});
            skLineSegment(sketch, "E663", {"start": v(-31.95, 15.23) * mm, "end": v(-32.41, 14.97) * mm});
            skLineSegment(sketch, "E664", {"start": v(-14.28, 12.84) * mm, "end": v(-13.83, 13.1) * mm});
            skLineSegment(sketch, "E665", {"start": v(-13.83, 13.1) * mm, "end": v(-13.37, 13.37) * mm});
            skLineSegment(sketch, "E666", {"start": v(-14.28, 10.73) * mm, "end": v(-13.83, 10.99) * mm});
            skLineSegment(sketch, "E667", {"start": v(-13.83, 10.99) * mm, "end": v(-13.37, 11.25) * mm});
            skLineSegment(sketch, "E668", {"start": v(-14.28, 9.67) * mm, "end": v(-13.83, 9.93) * mm});
            skLineSegment(sketch, "E669", {"start": v(-13.83, 9.93) * mm, "end": v(-13.37, 10.2) * mm});
            skLineSegment(sketch, "E670", {"start": v(-14.29, 14.97) * mm, "end": v(-14.4, 15.03) * mm});
            skLineSegment(sketch, "E671", {"start": v(-31.4, 15.56) * mm, "end": v(-31.5, 15.5) * mm});
            skLineSegment(sketch, "E672", {"start": v(-31.4, 19.82) * mm, "end": v(-31.4, 15.55) * mm});
            skLineSegment(sketch, "E673", {"start": v(-14.4, 15.03) * mm, "end": v(-14.4, 18.82) * mm});
            skLineSegment(sketch, "E674", {"start": v(-67.65, 26.53) * mm, "end": v(-66.4, 26.5) * mm});
            skLineSegment(sketch, "E675", {"start": v(-66.4, 26.5) * mm, "end": v(-65.28, 26.46) * mm});
            skLineSegment(sketch, "E676", {"start": v(-65.28, 26.46) * mm, "end": v(-64.32, 26.43) * mm});
            skLineSegment(sketch, "E677", {"start": v(-64.32, 26.43) * mm, "end": v(-63.5, 26.4) * mm});
            skLineSegment(sketch, "E678", {"start": v(-63.5, 26.4) * mm, "end": v(-62.64, 26.36) * mm});
            skLineSegment(sketch, "E679", {"start": v(-62.64, 26.36) * mm, "end": v(-62, 26.33) * mm});
            skLineSegment(sketch, "E680", {"start": v(-62, 26.33) * mm, "end": v(-61.53, 26.3) * mm});
            skLineSegment(sketch, "E681", {"start": v(-61.53, 26.3) * mm, "end": v(-61.1, 26.28) * mm});
            skLineSegment(sketch, "E682", {"start": v(-61.1, 26.28) * mm, "end": v(-60.89, 26.25) * mm});
            skLineSegment(sketch, "E683", {"start": v(-60.89, 26.25) * mm, "end": v(-60.82, 26.24) * mm});
            skLineSegment(sketch, "E684", {"start": v(-60.82, 26.24) * mm, "end": v(-60.82, 26.25) * mm});
            skLineSegment(sketch, "E685", {"start": v(-82.6, 26.53) * mm, "end": v(-82.63, 26.5) * mm});
            skLineSegment(sketch, "E686", {"start": v(-82.63, 26.5) * mm, "end": v(-82.68, 26.45) * mm});
            skLineSegment(sketch, "E687", {"start": v(-82.68, 26.45) * mm, "end": v(-82.71, 26.4) * mm});
            skLineSegment(sketch, "E688", {"start": v(-82.71, 26.4) * mm, "end": v(-82.79, 26.26) * mm});
            skLineSegment(sketch, "E689", {"start": v(-82.79, 26.26) * mm, "end": v(-82.83, 26.06) * mm});
            skLineSegment(sketch, "E690", {"start": v(-82.83, 26.06) * mm, "end": v(-82.84, 26.03) * mm});
            skLineSegment(sketch, "E691", {"start": v(-82.84, 26.03) * mm, "end": v(-82.84, 26) * mm});
            skLineSegment(sketch, "E692", {"start": v(-82.84, 26) * mm, "end": v(-82.84, 25.96) * mm});
            skLineSegment(sketch, "E693", {"start": v(-82.84, 25.96) * mm, "end": v(-82.83, 25.93) * mm});
            skLineSegment(sketch, "E694", {"start": v(-82.83, 25.93) * mm, "end": v(-82.82, 25.86) * mm});
            skLineSegment(sketch, "E695", {"start": v(-82.82, 25.86) * mm, "end": v(-82.8, 25.8) * mm});
            skLineSegment(sketch, "E696", {"start": v(-82.8, 25.8) * mm, "end": v(-82.75, 25.68) * mm});
            skLineSegment(sketch, "E697", {"start": v(-82.75, 25.68) * mm, "end": v(-82.71, 25.64) * mm});
            skLineSegment(sketch, "E698", {"start": v(-82.71, 25.64) * mm, "end": v(-82.68, 25.6) * mm});
            skLineSegment(sketch, "E699", {"start": v(-82.68, 25.6) * mm, "end": v(-82.66, 25.58) * mm});
            skLineSegment(sketch, "E700", {"start": v(-82.66, 25.58) * mm, "end": v(-82.64, 25.56) * mm});
            skLineSegment(sketch, "E701", {"start": v(-82.64, 25.56) * mm, "end": v(-82.64, 25.55) * mm});
            skLineSegment(sketch, "E702", {"start": v(-82.64, 25.55) * mm, "end": v(-82.63, 25.54) * mm});
            skLineSegment(sketch, "E703", {"start": v(-82.63, 25.54) * mm, "end": v(-82.62, 25.53) * mm});
            skLineSegment(sketch, "E704", {"start": v(-82.62, 25.53) * mm, "end": v(-82.62, 25.53) * mm});
            skLineSegment(sketch, "E705", {"start": v(-82.62, 25.53) * mm, "end": v(-82.6, 25.51) * mm});
            skLineSegment(sketch, "E706", {"start": v(-82.6, 25.51) * mm, "end": v(-82.6, 25.5) * mm});
            skLineSegment(sketch, "E707", {"start": v(-82.6, 25.5) * mm, "end": v(-82.57, 25.47) * mm});
            skLineSegment(sketch, "E708", {"start": v(-82.57, 25.47) * mm, "end": v(-82.55, 25.45) * mm});
            skLineSegment(sketch, "E709", {"start": v(-82.55, 25.45) * mm, "end": v(-82.52, 25.42) * mm});
            skLineSegment(sketch, "E710", {"start": v(-82.52, 25.42) * mm, "end": v(-82.46, 25.38) * mm});
            skLineSegment(sketch, "E711", {"start": v(-82.46, 25.38) * mm, "end": v(-82.34, 25.32) * mm});
            skLineSegment(sketch, "E712", {"start": v(-82.34, 25.32) * mm, "end": v(-82.23, 25.3) * mm});
            skLineSegment(sketch, "E713", {"start": v(-82.23, 25.3) * mm, "end": v(-82.06, 25.26) * mm});
            skLineSegment(sketch, "E714", {"start": v(-82.06, 25.26) * mm, "end": v(-81.77, 25.23) * mm});
            skLineSegment(sketch, "E715", {"start": v(-81.77, 25.23) * mm, "end": v(-81.3, 25.19) * mm});
            skLineSegment(sketch, "E716", {"start": v(-81.3, 25.19) * mm, "end": v(-80.59, 25.15) * mm});
            skLineSegment(sketch, "E717", {"start": v(-80.59, 25.15) * mm, "end": v(-79.55, 25.1) * mm});
            skLineSegment(sketch, "E718", {"start": v(-79.55, 25.1) * mm, "end": v(-78.6, 25.07) * mm});
            skLineSegment(sketch, "E719", {"start": v(-78.6, 25.07) * mm, "end": v(-77.61, 25.03) * mm});
            skLineSegment(sketch, "E720", {"start": v(-77.61, 25.03) * mm, "end": v(-76.61, 25) * mm});
            skLineSegment(sketch, "E721", {"start": v(-76.61, 25) * mm, "end": v(-75.63, 24.97) * mm});
            skLineSegment(sketch, "E722", {"start": v(-75.63, 24.97) * mm, "end": v(-74.41, 24.94) * mm});
            skLineSegment(sketch, "E723", {"start": v(-74.41, 24.94) * mm, "end": v(-73.3, 24.91) * mm});
            skLineSegment(sketch, "E724", {"start": v(-73.3, 24.91) * mm, "end": v(-72.32, 24.89) * mm});
            skLineSegment(sketch, "E725", {"start": v(-72.32, 24.89) * mm, "end": v(-70.97, 24.85) * mm});
            skLineSegment(sketch, "E726", {"start": v(-70.97, 24.85) * mm, "end": v(-69.63, 24.81) * mm});
            skLineSegment(sketch, "E727", {"start": v(-69.63, 24.81) * mm, "end": v(-68.3, 24.78) * mm});
            skLineSegment(sketch, "E728", {"start": v(-68.3, 24.78) * mm, "end": v(-66.85, 24.74) * mm});
            skLineSegment(sketch, "E729", {"start": v(-66.85, 24.74) * mm, "end": v(-65.81, 24.7) * mm});
            skLineSegment(sketch, "E730", {"start": v(-65.81, 24.7) * mm, "end": v(-64.75, 24.67) * mm});
            skLineSegment(sketch, "E731", {"start": v(-64.75, 24.67) * mm, "end": v(-63.75, 24.64) * mm});
            skLineSegment(sketch, "E732", {"start": v(-63.75, 24.64) * mm, "end": v(-62.53, 24.6) * mm});
            skLineSegment(sketch, "E733", {"start": v(-62.53, 24.6) * mm, "end": v(-61.65, 24.55) * mm});
            skLineSegment(sketch, "E734", {"start": v(-61.65, 24.55) * mm, "end": v(-61.23, 24.52) * mm});
            skLineSegment(sketch, "E735", {"start": v(-61.23, 24.52) * mm, "end": v(-60.96, 24.5) * mm});
            skLineSegment(sketch, "E736", {"start": v(-60.96, 24.5) * mm, "end": v(-60.85, 24.48) * mm});
            skLineSegment(sketch, "E737", {"start": v(-60.85, 24.48) * mm, "end": v(-60.84, 24.48) * mm});
            skLineSegment(sketch, "E738", {"start": v(-65.15, 24.15) * mm, "end": v(-64.78, 24.16) * mm});
            skLineSegment(sketch, "E739", {"start": v(-64.78, 24.16) * mm, "end": v(-63.7, 24.2) * mm});
            skLineSegment(sketch, "E740", {"start": v(-63.7, 24.2) * mm, "end": v(-62.7, 24.24) * mm});
            skLineSegment(sketch, "E741", {"start": v(-62.7, 24.24) * mm, "end": v(-61.83, 24.28) * mm});
            skLineSegment(sketch, "E742", {"start": v(-61.83, 24.28) * mm, "end": v(-61.17, 24.32) * mm});
            skLineSegment(sketch, "E743", {"start": v(-61.17, 24.32) * mm, "end": v(-60.72, 24.37) * mm});
            skLineSegment(sketch, "E744", {"start": v(-60.72, 24.37) * mm, "end": v(-60.4, 24.42) * mm});
            skLineSegment(sketch, "E745", {"start": v(-60.4, 24.42) * mm, "end": v(-60.17, 24.53) * mm});
            skLineSegment(sketch, "E746", {"start": v(-60.17, 24.53) * mm, "end": v(-60.09, 24.59) * mm});
            skLineSegment(sketch, "E747", {"start": v(-60.09, 24.59) * mm, "end": v(-60.01, 24.66) * mm});
            skLineSegment(sketch, "E748", {"start": v(-60.01, 24.66) * mm, "end": v(-59.94, 24.76) * mm});
            skLineSegment(sketch, "E749", {"start": v(-59.94, 24.76) * mm, "end": v(-59.9, 24.87) * mm});
            skLineSegment(sketch, "E750", {"start": v(-59.9, 24.87) * mm, "end": v(-59.85, 25.05) * mm});
            skLineSegment(sketch, "E751", {"start": v(-59.85, 25.05) * mm, "end": v(-59.85, 25.2) * mm});
            skLineSegment(sketch, "E752", {"start": v(-59.85, 25.2) * mm, "end": v(-59.89, 25.35) * mm});
            skLineSegment(sketch, "E753", {"start": v(-59.89, 25.35) * mm, "end": v(-59.92, 25.43) * mm});
            skLineSegment(sketch, "E754", {"start": v(-59.92, 25.43) * mm, "end": v(-59.94, 25.46) * mm});
            skLineSegment(sketch, "E755", {"start": v(-59.94, 25.46) * mm, "end": v(-59.96, 25.5) * mm});
            skLineSegment(sketch, "E756", {"start": v(-59.96, 25.5) * mm, "end": v(-59.98, 25.53) * mm});
            skLineSegment(sketch, "E757", {"start": v(-59.98, 25.53) * mm, "end": v(-60, 25.56) * mm});
            skLineSegment(sketch, "E758", {"start": v(-60, 25.56) * mm, "end": v(-60.05, 25.6) * mm});
            skLineSegment(sketch, "E759", {"start": v(-60.05, 25.6) * mm, "end": v(-60.14, 25.69) * mm});
            skLineSegment(sketch, "E760", {"start": v(-60.14, 25.69) * mm, "end": v(-60.42, 25.82) * mm});
            skLineSegment(sketch, "E761", {"start": v(-60.42, 25.82) * mm, "end": v(-60.49, 25.84) * mm});
            skLineSegment(sketch, "E762", {"start": v(-60.49, 25.84) * mm, "end": v(-60.57, 25.85) * mm});
            skLineSegment(sketch, "E763", {"start": v(-60.57, 25.85) * mm, "end": v(-60.7, 25.87) * mm});
            skLineSegment(sketch, "E764", {"start": v(-60.7, 25.87) * mm, "end": v(-60.9, 25.9) * mm});
            skLineSegment(sketch, "E765", {"start": v(-60.9, 25.9) * mm, "end": v(-61.28, 25.92) * mm});
            skLineSegment(sketch, "E766", {"start": v(-61.28, 25.92) * mm, "end": v(-61.86, 25.96) * mm});
            skLineSegment(sketch, "E767", {"start": v(-61.86, 25.96) * mm, "end": v(-62.72, 26) * mm});
            skLineSegment(sketch, "E768", {"start": v(-62.72, 26) * mm, "end": v(-63.57, 26.03) * mm});
            skLineSegment(sketch, "E769", {"start": v(-63.57, 26.03) * mm, "end": v(-64.53, 26.07) * mm});
            skLineSegment(sketch, "E770", {"start": v(-64.53, 26.07) * mm, "end": v(-65.5, 26.1) * mm});
            skLineSegment(sketch, "E771", {"start": v(-65.5, 26.1) * mm, "end": v(-66.44, 26.13) * mm});
            skLineSegment(sketch, "E772", {"start": v(-66.44, 26.13) * mm, "end": v(-67.61, 26.16) * mm});
            skLineSegment(sketch, "E773", {"start": v(-67.61, 26.16) * mm, "end": v(-68.66, 26.19) * mm});
            skLineSegment(sketch, "E774", {"start": v(-68.66, 26.19) * mm, "end": v(-69.59, 26.21) * mm});
            skLineSegment(sketch, "E775", {"start": v(-69.59, 26.21) * mm, "end": v(-70.88, 26.25) * mm});
            skLineSegment(sketch, "E776", {"start": v(-70.88, 26.25) * mm, "end": v(-72.13, 26.28) * mm});
            skLineSegment(sketch, "E777", {"start": v(-72.13, 26.28) * mm, "end": v(-73.06, 26.3) * mm});
            skLineSegment(sketch, "E778", {"start": v(-73.06, 26.3) * mm, "end": v(-74.12, 26.33) * mm});
            skLineSegment(sketch, "E779", {"start": v(-74.12, 26.33) * mm, "end": v(-75.28, 26.36) * mm});
            skLineSegment(sketch, "E780", {"start": v(-75.28, 26.36) * mm, "end": v(-76.53, 26.4) * mm});
            skLineSegment(sketch, "E781", {"start": v(-76.53, 26.4) * mm, "end": v(-77.73, 26.44) * mm});
            skLineSegment(sketch, "E782", {"start": v(-77.73, 26.44) * mm, "end": v(-78.82, 26.48) * mm});
            skLineSegment(sketch, "E783", {"start": v(-78.82, 26.48) * mm, "end": v(-79.54, 26.5) * mm});
            skLineSegment(sketch, "E784", {"start": v(-79.54, 26.5) * mm, "end": v(-80.15, 26.53) * mm});
            skLineSegment(sketch, "E785", {"start": v(-62.77, 26) * mm, "end": v(-61.88, 26.04) * mm});
            skLineSegment(sketch, "E786", {"start": v(-61.88, 26.04) * mm, "end": v(-61.34, 26.07) * mm});
            skLineSegment(sketch, "E787", {"start": v(-61.34, 26.07) * mm, "end": v(-60.95, 26.1) * mm});
            skLineSegment(sketch, "E788", {"start": v(-60.95, 26.1) * mm, "end": v(-60.68, 26.13) * mm});
            skLineSegment(sketch, "E789", {"start": v(-60.68, 26.13) * mm, "end": v(-60.4, 26.18) * mm});
            skLineSegment(sketch, "E790", {"start": v(-60.4, 26.18) * mm, "end": v(-60.25, 26.24) * mm});
            skLineSegment(sketch, "E791", {"start": v(-60.25, 26.24) * mm, "end": v(-60.14, 26.3) * mm});
            skLineSegment(sketch, "E792", {"start": v(-60.14, 26.3) * mm, "end": v(-60.01, 26.43) * mm});
            skLineSegment(sketch, "E793", {"start": v(-60.01, 26.43) * mm, "end": v(-59.94, 26.53) * mm});
            skLineSegment(sketch, "E794", {"start": v(-59.94, 26.53) * mm, "end": v(-59.88, 26.67) * mm});
            skLineSegment(sketch, "E795", {"start": v(-59.88, 26.67) * mm, "end": v(-59.85, 26.86) * mm});
            skLineSegment(sketch, "E796", {"start": v(-59.85, 26.86) * mm, "end": v(-59.86, 27.04) * mm});
            skLineSegment(sketch, "E797", {"start": v(-59.86, 27.04) * mm, "end": v(-59.91, 27.18) * mm});
            skLineSegment(sketch, "E798", {"start": v(-59.91, 27.18) * mm, "end": v(-59.97, 27.29) * mm});
            skLineSegment(sketch, "E799", {"start": v(-59.97, 27.29) * mm, "end": v(-60.1, 27.43) * mm});
            skLineSegment(sketch, "E800", {"start": v(-60.1, 27.43) * mm, "end": v(-60.28, 27.54) * mm});
            skLineSegment(sketch, "E801", {"start": v(-60.28, 27.54) * mm, "end": v(-60.45, 27.6) * mm});
            skLineSegment(sketch, "E802", {"start": v(-60.45, 27.6) * mm, "end": v(-60.6, 27.62) * mm});
            skLineSegment(sketch, "E803", {"start": v(-60.6, 27.62) * mm, "end": v(-60.82, 27.65) * mm});
            skLineSegment(sketch, "E804", {"start": v(-60.82, 27.65) * mm, "end": v(-61.04, 27.67) * mm});
            skLineSegment(sketch, "E805", {"start": v(-61.04, 27.67) * mm, "end": v(-61.4, 27.7) * mm});
            skLineSegment(sketch, "E806", {"start": v(-61.4, 27.7) * mm, "end": v(-61.96, 27.73) * mm});
            skLineSegment(sketch, "E807", {"start": v(-61.96, 27.73) * mm, "end": v(-62.48, 27.76) * mm});
            skLineSegment(sketch, "E808", {"start": v(-62.48, 27.76) * mm, "end": v(-63.15, 27.78) * mm});
            skLineSegment(sketch, "E809", {"start": v(-63.15, 27.78) * mm, "end": v(-63.99, 27.82) * mm});
            skLineSegment(sketch, "E810", {"start": v(-63.99, 27.82) * mm, "end": v(-65.02, 27.85) * mm});
            skLineSegment(sketch, "E811", {"start": v(-65.02, 27.85) * mm, "end": v(-66.24, 27.89) * mm});
            skLineSegment(sketch, "E812", {"start": v(-66.24, 27.89) * mm, "end": v(-67.65, 27.93) * mm});
            skLineSegment(sketch, "E813", {"start": v(-73.23, 26.53) * mm, "end": v(-67.65, 26.53) * mm});
            skLineSegment(sketch, "E814", {"start": v(-67.65, 27.93) * mm, "end": v(-73.23, 27.93) * mm});
            skLineSegment(sketch, "E815", {"start": v(-99.93, 26.53) * mm, "end": v(-94.68, 26.53) * mm});
            skLineSegment(sketch, "E816", {"start": v(-91.68, 26.53) * mm, "end": v(-73.23, 26.53) * mm});
            skLineSegment(sketch, "E817", {"start": v(-73.23, 27.93) * mm, "end": v(-91.42, 27.93) * mm});
            skLineSegment(sketch, "E818", {"start": v(-94.6, 27.93) * mm, "end": v(-99.93, 27.93) * mm});
            skArc(sketch, "E819", {"start": v(-94.8, 25.28) * mm, "mid": v(-95.96, 24.88) * mm, "end": v(-96.61, 23.84) * mm});
            skLineSegment(sketch, "E820", {"start": v(-82.16, 25.28) * mm, "end": v(-91.68, 25.28) * mm});
            skLineSegment(sketch, "E821", {"start": v(-94.68, 25.28) * mm, "end": v(-94.8, 25.28) * mm});
            skArc(sketch, "E822", {"start": v(-11.5, 3.13) * mm, "mid": v(-11.63, 3.66) * mm, "end": v(-12.1, 3.94) * mm});
            skArc(sketch, "E823", {"start": v(-33.68, 3.94) * mm, "mid": v(-34.16, 3.66) * mm, "end": v(-34.28, 3.13) * mm});
            skArc(sketch, "E824", {"start": v(-14.95, -1.1) * mm, "mid": v(-12.67, 0.57) * mm, "end": v(-11.5, 3.13) * mm});
            skArc(sketch, "E825", {"start": v(-34.28, 3.13) * mm, "mid": v(-33.1, 0.57) * mm, "end": v(-30.83, -1.1) * mm});
            skLineSegment(sketch, "E826", {"start": v(-54.5, 23.88) * mm, "end": v(-54.5, 26.08) * mm});
            skLineSegment(sketch, "E827", {"start": v(-55.5, 26.08) * mm, "end": v(-55.5, 23.88) * mm});
            skLineSegment(sketch, "E828", {"start": v(-15.37, -1.42) * mm, "end": v(-30.4, -1.42) * mm});
            skLineSegment(sketch, "E829", {"start": v(-102.28, 3.94) * mm, "end": v(-114.98, 3.94) * mm});
            skLineSegment(sketch, "E830", {"start": v(-114.98, 3.94) * mm, "end": v(-114.98, 5.2) * mm});
            skLineSegment(sketch, "E831", {"start": v(-102.28, 5.2) * mm, "end": v(-114.98, 5.2) * mm});
            skLineSegment(sketch, "E832", {"start": v(-42.59, 3.94) * mm, "end": v(-102.28, 3.94) * mm});
            skLineSegment(sketch, "E833", {"start": v(-42.59, 5.2) * mm, "end": v(-102.28, 5.2) * mm});
            skLineSegment(sketch, "E834", {"start": v(-34.14, 3.94) * mm, "end": v(-42.59, 3.94) * mm});
            skLineSegment(sketch, "E835", {"start": v(-34.14, 5.2) * mm, "end": v(-42.59, 5.2) * mm});
            skLineSegment(sketch, "E836", {"start": v(-12.47, 3.94) * mm, "end": v(-34.14, 3.94) * mm});
            skLineSegment(sketch, "E837", {"start": v(-12.47, 5.2) * mm, "end": v(-34.14, 5.2) * mm});
            skArc(sketch, "E838", {"start": v(-43.62, 9.02) * mm, "mid": v(-42.5, 6.32) * mm, "end": v(-39.8, 5.2) * mm});
            skArc(sketch, "E839", {"start": v(-107.63, 5.2) * mm, "mid": v(-104.93, 6.32) * mm, "end": v(-103.82, 9.02) * mm});
            skLineSegment(sketch, "E840", {"start": v(-49.97, 23.88) * mm, "end": v(-48.38, 23.88) * mm});
            skArc(sketch, "E841", {"start": v(-43.62, 19.12) * mm, "mid": v(-45.01, 22.48) * mm, "end": v(-48.38, 23.88) * mm});
            skArc(sketch, "E842", {"start": v(-99.05, 23.88) * mm, "mid": v(-102.42, 22.48) * mm, "end": v(-103.82, 19.12) * mm});
            skLineSegment(sketch, "E843", {"start": v(-99.05, 23.88) * mm, "end": v(-97.47, 23.88) * mm});
            skLineSegment(sketch, "E844", {"start": v(-97.47, 23.88) * mm, "end": v(-49.97, 23.88) * mm});
            skLineSegment(sketch, "E845", {"start": v(-103.82, 19.12) * mm, "end": v(-103.82, 9.02) * mm});
            skLineSegment(sketch, "E846", {"start": v(-43.62, 19.12) * mm, "end": v(-43.62, 9.02) * mm});
            skLineSegment(sketch, "E847", {"start": v(-3.98, 3.94) * mm, "end": v(-12.47, 3.94) * mm});
            skLineSegment(sketch, "E848", {"start": v(-3.98, 5.2) * mm, "end": v(-12.47, 5.2) * mm});
            skLineSegment(sketch, "E849", {"start": v(-41.97, 13.04) * mm, "end": v(-41.97, 15) * mm});
            skLineSegment(sketch, "E850", {"start": v(-41.97, 8.9) * mm, "end": v(-41.97, 13.04) * mm});
            skEllipticalArc(sketch, "E851", {});
            skArc(sketch, "E852", {"start": v(-105.8, 10.58) * mm, "mid": v(-105.22, 10.85) * mm, "end": v(-105.05, 11.48) * mm});
            skLineSegment(sketch, "E853", {"start": v(-105.05, 13.62) * mm, "end": v(-105.05, 11.48) * mm});
            skLineSegment(sketch, "E854", {"start": v(-105.8, 13.97) * mm, "end": v(-105.58, 13.97) * mm});
            skLineSegment(sketch, "E855", {"start": v(-105.58, 13.97) * mm, "end": v(-105.38, 13.95) * mm});
            skLineSegment(sketch, "E856", {"start": v(-105.38, 13.95) * mm, "end": v(-105.22, 13.92) * mm});
            skLineSegment(sketch, "E857", {"start": v(-105.22, 13.92) * mm, "end": v(-105.11, 13.85) * mm});
            skLineSegment(sketch, "E858", {"start": v(-105.11, 13.85) * mm, "end": v(-105.05, 13.68) * mm});
            skLineSegment(sketch, "E859", {"start": v(-105.05, 13.68) * mm, "end": v(-105.05, 13.62) * mm});
            skArc(sketch, "E860", {"start": v(-109.13, 15) * mm, "mid": v(-109.36, 14.96) * mm, "end": v(-109.47, 14.77) * mm});
            skLineSegment(sketch, "E861", {"start": v(-105.8, 13.97) * mm, "end": v(-109.13, 15) * mm});
            skLineSegment(sketch, "E862", {"start": v(-109.13, 9.56) * mm, "end": v(-105.8, 10.58) * mm});
            skArc(sketch, "E863", {"start": v(-109.47, 9.79) * mm, "mid": v(-109.36, 9.6) * mm, "end": v(-109.13, 9.56) * mm});
            skLineSegment(sketch, "E864", {"start": v(-109.47, 9.79) * mm, "end": v(-109.47, 14.77) * mm});
            skArc(sketch, "E865", {"start": v(-109.47, 9.14) * mm, "mid": v(-109.36, 8.94) * mm, "end": v(-109.13, 8.91) * mm});
            skLineSegment(sketch, "E866", {"start": v(-109.47, 9.14) * mm, "end": v(-109.47, 9.79) * mm});
            skLineSegment(sketch, "E867", {"start": v(-105.84, 9.92) * mm, "end": v(-109.13, 8.91) * mm});
            skArc(sketch, "E868", {"start": v(-10.13, 8.25) * mm, "mid": v(-13.32, 9.28) * mm, "end": v(-16.51, 8.25) * mm});
            skArc(sketch, "E869", {"start": v(-16.51, 8.25) * mm, "mid": v(-22.9, 9.3) * mm, "end": v(-29.27, 8.25) * mm});
            skArc(sketch, "E870", {"start": v(-29.27, 8.25) * mm, "mid": v(-32.46, 9.28) * mm, "end": v(-35.65, 8.25) * mm});
            skLineSegment(sketch, "E871", {"start": v(-22.9, 9.44) * mm, "end": v(-33.73, 9.44) * mm});
            skLineSegment(sketch, "E872", {"start": v(-12.05, 9.44) * mm, "end": v(-22.9, 9.44) * mm});
            skLineSegment(sketch, "E873", {"start": v(-16.51, 6.34) * mm, "end": v(-16.51, 8.25) * mm});
            skArc(sketch, "E874", {"start": v(-29.27, 6.34) * mm, "mid": v(-22.9, 5.3) * mm, "end": v(-16.51, 6.34) * mm});
            skLineSegment(sketch, "E875", {"start": v(-29.27, 6.34) * mm, "end": v(-29.27, 8.25) * mm});
            skLineSegment(sketch, "E876", {"start": v(-10.13, 6.34) * mm, "end": v(-10.13, 8.25) * mm});
            skArc(sketch, "E877", {"start": v(-16.51, 6.34) * mm, "mid": v(-13.32, 5.3) * mm, "end": v(-10.13, 6.34) * mm});
            skArc(sketch, "E878", {"start": v(-35.65, 6.34) * mm, "mid": v(-32.46, 5.3) * mm, "end": v(-29.27, 6.34) * mm});
            skLineSegment(sketch, "E879", {"start": v(-35.65, 6.34) * mm, "end": v(-35.65, 8.25) * mm});
            skLineSegment(sketch, "E880", {"start": v(-84.99, 44.06) * mm, "end": v(-88.96, 44.06) * mm});
            skLineSegment(sketch, "E881", {"start": v(-88.96, 44.06) * mm, "end": v(-88.96, 47.06) * mm});
            skLineSegment(sketch, "E882", {"start": v(-84.99, 47.06) * mm, "end": v(-88.96, 47.06) * mm});
            skLineSegment(sketch, "E883", {"start": v(-76.4, 44.06) * mm, "end": v(-79.1, 44.06) * mm});
            skLineSegment(sketch, "E884", {"start": v(-76.4, 47.06) * mm, "end": v(-79.1, 47.06) * mm});
            skLineSegment(sketch, "E885", {"start": v(-79.1, 47.06) * mm, "end": v(-84.99, 47.06) * mm});
            skLineSegment(sketch, "E886", {"start": v(-79.1, 44.06) * mm, "end": v(-84.99, 44.06) * mm});
            skLineSegment(sketch, "E887", {"start": v(-66.78, 47.06) * mm, "end": v(-76.4, 47.06) * mm});
            skLineSegment(sketch, "E888", {"start": v(-66.78, 44.06) * mm, "end": v(-76.4, 44.06) * mm});
            skLineSegment(sketch, "E889", {"start": v(-66.6, 47.06) * mm, "end": v(-66.78, 47.06) * mm});
            skLineSegment(sketch, "E890", {"start": v(-66.6, 44.06) * mm, "end": v(-66.78, 44.06) * mm});
            skArc(sketch, "E891", {"start": v(-61.7, 42.48) * mm, "mid": v(-63.68, 44.93) * mm, "end": v(-66.6, 46.11) * mm});
            skArc(sketch, "E892", {"start": v(-77.5, 44.06) * mm, "mid": v(-76.2, 43.91) * mm, "end": v(-74.88, 43.78) * mm});
            skLineSegment(sketch, "E893", {"start": v(-74.88, 44.06) * mm, "end": v(-74.88, 43.78) * mm});
            skLineSegment(sketch, "E894", {"start": v(-88.96, 44.06) * mm, "end": v(-88.96, 42.48) * mm});
            skLineSegment(sketch, "E895", {"start": v(-67.9, 43.78) * mm, "end": v(-74.88, 43.78) * mm});
            skArc(sketch, "E896", {"start": v(-61.7, 42.48) * mm, "mid": v(-64.7, 43.55) * mm, "end": v(-67.9, 43.78) * mm});
            skLineSegment(sketch, "E897", {"start": v(-67.9, 44.06) * mm, "end": v(-67.9, 43.78) * mm});
            skLineSegment(sketch, "E898", {"start": v(-59.96, 33.23) * mm, "end": v(-59.96, 37.51) * mm});
            skLineSegment(sketch, "E899", {"start": v(-88.96, 42.48) * mm, "end": v(-88.96, 33.23) * mm});
            skArc(sketch, "E900", {"start": v(-59.96, 37.51) * mm, "mid": v(-60.4, 40.14) * mm, "end": v(-61.7, 42.48) * mm});
            skLineSegment(sketch, "E901", {"start": v(-59.96, 28.64) * mm, "end": v(-59.96, 33.23) * mm});
            skLineSegment(sketch, "E902", {"start": v(-89.06, 28.64) * mm, "end": v(-59.96, 28.64) * mm});
            skLineSegment(sketch, "E903", {"start": v(-88.96, 28.7) * mm, "end": v(-89.06, 28.64) * mm});
            skLineSegment(sketch, "E904", {"start": v(-88.96, 33.23) * mm, "end": v(-88.96, 28.7) * mm});
            skLineSegment(sketch, "E905", {"start": v(-89.06, 31.64) * mm, "end": v(-89.06, 28.64) * mm});
            skLineSegment(sketch, "E906", {"start": v(-89.06, 28.64) * mm, "end": v(-90.1, 28.64) * mm});
            skLineSegment(sketch, "E907", {"start": v(-90.1, 28.64) * mm, "end": v(-90.1, 31.64) * mm});
            skLineSegment(sketch, "E908", {"start": v(-89.06, 31.64) * mm, "end": v(-90.1, 31.64) * mm});
            skLineSegment(sketch, "E909", {"start": v(-90.1, 28.64) * mm, "end": v(-90.12, 28.64) * mm});
            skLineSegment(sketch, "E910", {"start": v(-90.1, 31.64) * mm, "end": v(-90.17, 31.64) * mm});
            skArc(sketch, "E911", {"start": v(-90.12, 28.64) * mm, "mid": v(-91.23, 28.17) * mm, "end": v(-91.68, 27.05) * mm});
            skArc(sketch, "E912", {"start": v(-90.17, 31.64) * mm, "mid": v(-93.37, 30.27) * mm, "end": v(-94.68, 27.05) * mm});
            skLineSegment(sketch, "E913", {"start": v(-94.68, 27.05) * mm, "end": v(-94.68, 23.88) * mm});
            skLineSegment(sketch, "E914", {"start": v(-91.68, 27.05) * mm, "end": v(-91.68, 23.88) * mm});
            skLineSegment(sketch, "E915", {"start": v(-45.73, 28.64) * mm, "end": v(-59.96, 28.64) * mm});
            skLineSegment(sketch, "E916", {"start": v(-45.73, 31.64) * mm, "end": v(-59.96, 31.64) * mm});
            skLineSegment(sketch, "E917", {"start": v(-43.44, 28.64) * mm, "end": v(-45.73, 28.64) * mm});
            skLineSegment(sketch, "E918", {"start": v(-43.44, 31.64) * mm, "end": v(-45.73, 31.64) * mm});
            skArc(sketch, "E919", {"start": v(-41.85, 27.05) * mm, "mid": v(-42.32, 28.18) * mm, "end": v(-43.44, 28.64) * mm});
            skArc(sketch, "E920", {"start": v(-38.85, 27.05) * mm, "mid": v(-40.2, 30.3) * mm, "end": v(-43.44, 31.64) * mm});
            skLineSegment(sketch, "E921", {"start": v(-41.85, 18.5) * mm, "end": v(-41.85, 27.05) * mm});
            skLineSegment(sketch, "E922", {"start": v(-38.85, 18.5) * mm, "end": v(-38.85, 27.05) * mm});
            skLineSegment(sketch, "E923", {"start": v(-41.85, 16.91) * mm, "end": v(-38.85, 16.91) * mm});
            skLineSegment(sketch, "E924", {"start": v(-41.85, 16.91) * mm, "end": v(-41.85, 18.5) * mm});
            skLineSegment(sketch, "E925", {"start": v(-38.85, 16.91) * mm, "end": v(-38.85, 18.5) * mm});
            skLineSegment(sketch, "E926", {"start": v(-59.77, 33.23) * mm, "end": v(-59.77, 31.64) * mm});
            skLineSegment(sketch, "E927", {"start": v(-59.77, 41.17) * mm, "end": v(-60.85, 41.17) * mm});
            skLineSegment(sketch, "E928", {"start": v(-59.77, 41.17) * mm, "end": v(-59.77, 36.58) * mm});
            skLineSegment(sketch, "E929", {"start": v(-59.77, 36.58) * mm, "end": v(-59.77, 33.23) * mm});
            skArc(sketch, "E930", {"start": v(-26.13, 13.17) * mm, "mid": v(-27.12, 12.95) * mm, "end": v(-28.1, 12.68) * mm});
            skArc(sketch, "E931", {"start": v(-32.38, 12.84) * mm, "mid": v(-30.24, 12.72) * mm, "end": v(-28.1, 12.68) * mm});
            skArc(sketch, "E932", {"start": v(-31.47, 13.37) * mm, "mid": v(-28.8, 13.22) * mm, "end": v(-26.13, 13.17) * mm});
            skArc(sketch, "E933", {"start": v(-17.68, 12.48) * mm, "mid": v(-18.66, 12.78) * mm, "end": v(-19.65, 13.04) * mm});
            skArc(sketch, "E934", {"start": v(-14.31, 12.85) * mm, "mid": v(-16.98, 13) * mm, "end": v(-19.65, 13.04) * mm});
            skArc(sketch, "E935", {"start": v(-13.4, 12.32) * mm, "mid": v(-15.54, 12.44) * mm, "end": v(-17.68, 12.48) * mm});
            skArc(sketch, "E936", {"start": v(-26.13, 14.23) * mm, "mid": v(-27.12, 14) * mm, "end": v(-28.1, 13.74) * mm});
            skArc(sketch, "E937", {"start": v(-32.38, 13.9) * mm, "mid": v(-30.24, 13.78) * mm, "end": v(-28.1, 13.74) * mm});
            skArc(sketch, "E938", {"start": v(-31.47, 14.42) * mm, "mid": v(-28.8, 14.28) * mm, "end": v(-26.13, 14.23) * mm});
            skArc(sketch, "E939", {"start": v(-28.1, 13.74) * mm, "mid": v(-27.12, 13.43) * mm, "end": v(-26.13, 13.17) * mm});
            skArc(sketch, "E940", {"start": v(-17.68, 14.6) * mm, "mid": v(-18.66, 14.9) * mm, "end": v(-19.65, 15.16) * mm});
            skArc(sketch, "E941", {"start": v(-13.4, 14.44) * mm, "mid": v(-15.54, 14.55) * mm, "end": v(-17.68, 14.6) * mm});
            skArc(sketch, "E942", {"start": v(-17.68, 13.54) * mm, "mid": v(-18.66, 13.84) * mm, "end": v(-19.65, 14.1) * mm});
            skArc(sketch, "E943", {"start": v(-14.31, 13.9) * mm, "mid": v(-16.98, 14.05) * mm, "end": v(-19.65, 14.1) * mm});
            skArc(sketch, "E944", {"start": v(-13.4, 13.38) * mm, "mid": v(-15.54, 13.5) * mm, "end": v(-17.68, 13.54) * mm});
            skArc(sketch, "E945", {"start": v(-28.1, 14.8) * mm, "mid": v(-27.12, 14.5) * mm, "end": v(-26.13, 14.23) * mm});
            skArc(sketch, "E946", {"start": v(-32.38, 14.95) * mm, "mid": v(-30.24, 14.84) * mm, "end": v(-28.1, 14.8) * mm});
            skArc(sketch, "E947", {"start": v(-26.13, 11.06) * mm, "mid": v(-27.12, 10.83) * mm, "end": v(-28.1, 10.56) * mm});
            skArc(sketch, "E948", {"start": v(-32.38, 10.72) * mm, "mid": v(-30.24, 10.6) * mm, "end": v(-28.1, 10.56) * mm});
            skArc(sketch, "E949", {"start": v(-31.47, 11.25) * mm, "mid": v(-28.8, 11.1) * mm, "end": v(-26.13, 11.06) * mm});
            skArc(sketch, "E950", {"start": v(-28.1, 10.56) * mm, "mid": v(-27.12, 10.26) * mm, "end": v(-26.13, 10) * mm});
            skArc(sketch, "E951", {"start": v(-31.47, 10.2) * mm, "mid": v(-28.8, 10.05) * mm, "end": v(-26.13, 10) * mm});
            skArc(sketch, "E952", {"start": v(-17.68, 11.42) * mm, "mid": v(-18.66, 11.73) * mm, "end": v(-19.65, 11.99) * mm});
            skArc(sketch, "E953", {"start": v(-14.31, 11.8) * mm, "mid": v(-16.98, 11.94) * mm, "end": v(-19.65, 11.99) * mm});
            skArc(sketch, "E954", {"start": v(-13.4, 11.26) * mm, "mid": v(-15.54, 11.38) * mm, "end": v(-17.68, 11.42) * mm});
            skArc(sketch, "E955", {"start": v(-28.1, 12.68) * mm, "mid": v(-27.12, 12.37) * mm, "end": v(-26.13, 12.11) * mm});
            skArc(sketch, "E956", {"start": v(-31.47, 12.3) * mm, "mid": v(-28.8, 12.16) * mm, "end": v(-26.13, 12.11) * mm});
            skArc(sketch, "E957", {"start": v(-17.68, 10.36) * mm, "mid": v(-18.66, 10.67) * mm, "end": v(-19.65, 10.93) * mm});
            skArc(sketch, "E958", {"start": v(-14.31, 10.73) * mm, "mid": v(-16.98, 10.88) * mm, "end": v(-19.65, 10.93) * mm});
            skArc(sketch, "E959", {"start": v(-13.4, 10.2) * mm, "mid": v(-15.54, 10.32) * mm, "end": v(-17.68, 10.36) * mm});
            skArc(sketch, "E960", {"start": v(-26.13, 12.11) * mm, "mid": v(-27.12, 11.89) * mm, "end": v(-28.1, 11.62) * mm});
            skArc(sketch, "E961", {"start": v(-32.38, 11.78) * mm, "mid": v(-30.24, 11.66) * mm, "end": v(-28.1, 11.62) * mm});
            skArc(sketch, "E962", {"start": v(-28.1, 11.62) * mm, "mid": v(-27.12, 11.32) * mm, "end": v(-26.13, 11.06) * mm});
            skArc(sketch, "E963", {"start": v(-26.13, 10) * mm, "mid": v(-27.12, 9.77) * mm, "end": v(-28.1, 9.5) * mm});
            skArc(sketch, "E964", {"start": v(-32.38, 9.66) * mm, "mid": v(-30.24, 9.55) * mm, "end": v(-28.1, 9.5) * mm});
            skArc(sketch, "E965", {"start": v(-18.12, 9.44) * mm, "mid": v(-18.88, 9.67) * mm, "end": v(-19.65, 9.87) * mm});
            skArc(sketch, "E966", {"start": v(-14.31, 9.68) * mm, "mid": v(-16.98, 9.82) * mm, "end": v(-19.65, 9.87) * mm});
            skLineSegment(sketch, "E967", {"start": v(-27.92, 9.44) * mm, "end": v(-28.1, 9.5) * mm});
            skArc(sketch, "E968", {"start": v(-19.65, 11.99) * mm, "mid": v(-18.66, 12.21) * mm, "end": v(-17.68, 12.48) * mm});
            skArc(sketch, "E969", {"start": v(-19.65, 14.1) * mm, "mid": v(-18.66, 14.33) * mm, "end": v(-17.68, 14.6) * mm});
            skArc(sketch, "E970", {"start": v(-26.13, 15.29) * mm, "mid": v(-27.12, 15.06) * mm, "end": v(-28.1, 14.8) * mm});
            skArc(sketch, "E971", {"start": v(-19.65, 13.04) * mm, "mid": v(-18.66, 13.27) * mm, "end": v(-17.68, 13.54) * mm});
            skArc(sketch, "E972", {"start": v(-19.65, 10.93) * mm, "mid": v(-18.66, 11.15) * mm, "end": v(-17.68, 11.42) * mm});
            skArc(sketch, "E973", {"start": v(-19.65, 9.87) * mm, "mid": v(-18.66, 10.1) * mm, "end": v(-17.68, 10.36) * mm});
            skArc(sketch, "E974", {"start": v(-19.65, 15.16) * mm, "mid": v(-19.8, 15.2) * mm, "end": v(-19.95, 15.23) * mm});
            skArc(sketch, "E975", {"start": v(-14.42, 15.03) * mm, "mid": v(-17.18, 15.18) * mm, "end": v(-19.95, 15.23) * mm});
            skArc(sketch, "E976", {"start": v(-25.83, 15.35) * mm, "mid": v(-25.98, 15.32) * mm, "end": v(-26.13, 15.29) * mm});
            skArc(sketch, "E977", {"start": v(-31.4, 15.55) * mm, "mid": v(-28.61, 15.4) * mm, "end": v(-25.83, 15.35) * mm});
            skLineSegment(sketch, "E978", {"start": v(-31.4, 19.82) * mm, "end": v(-31.19, 19.82) * mm});
            skLineSegment(sketch, "E979", {"start": v(-31.19, 19.82) * mm, "end": v(-31.19, 18.82) * mm});
            skLineSegment(sketch, "E980", {"start": v(-25.83, 18.82) * mm, "end": v(-31.19, 18.82) * mm});
            skLineSegment(sketch, "E981", {"start": v(-25.83, 18.82) * mm, "end": v(-25.83, 15.35) * mm});
            skLineSegment(sketch, "E982", {"start": v(-19.95, 15.23) * mm, "end": v(-19.95, 18.82) * mm});
            skLineSegment(sketch, "E983", {"start": v(-19.95, 18.82) * mm, "end": v(-25.83, 18.82) * mm});
            skLineSegment(sketch, "E984", {"start": v(-14.4, 18.82) * mm, "end": v(-15.3, 18.82) * mm});
            skLineSegment(sketch, "E985", {"start": v(-18.81, 18.82) * mm, "end": v(-19.95, 18.82) * mm});
            skLineSegment(sketch, "E986", {"start": v(-31.19, 19.82) * mm, "end": v(-30.83, 19.82) * mm});
            skLineSegment(sketch, "E987", {"start": v(-29.7, 18.82) * mm, "end": v(-29.7, 19.82) * mm});
            skLineSegment(sketch, "E988", {"start": v(-21.04, 19.82) * mm, "end": v(-21.04, 18.82) * mm});
            skLineSegment(sketch, "E989", {"start": v(-14.96, 19.82) * mm, "end": v(-14.96, 18.82) * mm});
            skLineSegment(sketch, "E990", {"start": v(-15.3, 18.82) * mm, "end": v(-18.81, 18.82) * mm});
            skLineSegment(sketch, "E991", {"start": v(-29.17, 19.82) * mm, "end": v(-29.17, 18.82) * mm});
            skLineSegment(sketch, "E992", {"start": v(-25.37, 19.82) * mm, "end": v(-25.37, 18.82) * mm});
            skLineSegment(sketch, "E993", {"start": v(-67.65, 26.53) * mm, "end": v(-67.56, 26.58) * mm});
            skLineSegment(sketch, "E994", {"start": v(-67.56, 26.58) * mm, "end": v(-67.48, 26.73) * mm});
            skLineSegment(sketch, "E995", {"start": v(-67.48, 26.73) * mm, "end": v(-67.43, 26.96) * mm});
            skLineSegment(sketch, "E996", {"start": v(-67.43, 26.96) * mm, "end": v(-67.41, 27.23) * mm});
            skLineSegment(sketch, "E997", {"start": v(-67.41, 27.23) * mm, "end": v(-67.43, 27.5) * mm});
            skLineSegment(sketch, "E998", {"start": v(-67.43, 27.5) * mm, "end": v(-67.48, 27.72) * mm});
            skLineSegment(sketch, "E999", {"start": v(-67.48, 27.72) * mm, "end": v(-67.56, 27.87) * mm});
            skLineSegment(sketch, "E1000", {"start": v(-67.56, 27.87) * mm, "end": v(-67.65, 27.93) * mm});
            skLineSegment(sketch, "E1001", {"start": v(-99.93, 26.53) * mm, "end": v(-100.02, 26.58) * mm});
            skLineSegment(sketch, "E1002", {"start": v(-100.02, 26.58) * mm, "end": v(-100.1, 26.73) * mm});
            skLineSegment(sketch, "E1003", {"start": v(-100.1, 26.73) * mm, "end": v(-100.16, 26.96) * mm});
            skLineSegment(sketch, "E1004", {"start": v(-100.16, 26.96) * mm, "end": v(-100.18, 27.23) * mm});
            skLineSegment(sketch, "E1005", {"start": v(-100.18, 27.23) * mm, "end": v(-100.16, 27.5) * mm});
            skLineSegment(sketch, "E1006", {"start": v(-100.16, 27.5) * mm, "end": v(-100.1, 27.72) * mm});
            skLineSegment(sketch, "E1007", {"start": v(-100.1, 27.72) * mm, "end": v(-100.02, 27.87) * mm});
            skLineSegment(sketch, "E1008", {"start": v(-100.02, 27.87) * mm, "end": v(-99.93, 27.93) * mm});
            skLineSegment(sketch, "E1009", {"start": v(-99.93, 27.93) * mm, "end": v(-99.93, 27.93) * mm});
            skLineSegment(sketch, "E1010", {"start": v(-30.83, 21.82) * mm, "end": v(-30.83, 19.82) * mm});
            skLineSegment(sketch, "E1011", {"start": v(-14.95, 21.82) * mm, "end": v(-30.83, 21.82) * mm});
            skLineSegment(sketch, "E1012", {"start": v(-14.95, 21.82) * mm, "end": v(-14.95, 19.82) * mm});
            skLineSegment(sketch, "E1013", {"start": v(-14.95, 19.82) * mm, "end": v(-30.83, 19.82) * mm});
            skArc(sketch, "E1014", {"start": v(-69.17, 2.13) * mm, "mid": v(-65.72, 2.45) * mm, "end": v(-62.43, 3.52) * mm});
            skLineSegment(sketch, "E1015", {"start": v(-78.26, 2.13) * mm, "end": v(-69.17, 2.13) * mm});
            skArc(sketch, "E1016", {"start": v(-85, 3.52) * mm, "mid": v(-81.7, 2.45) * mm, "end": v(-78.26, 2.13) * mm});
            skLineSegment(sketch, "E1017", {"start": v(-62.43, 3.52) * mm, "end": v(-61.6, 3.94) * mm});
            skLineSegment(sketch, "E1018", {"start": v(-85.83, 3.94) * mm, "end": v(-85, 3.52) * mm});
            skLineSegment(sketch, "E1019", {"start": v(-22.9, -1.1) * mm, "end": v(-30.83, -1.1) * mm});
            skLineSegment(sketch, "E1020", {"start": v(-14.95, -1.1) * mm, "end": v(-22.9, -1.1) * mm});
            skLineSegment(sketch, "E1021", {"start": v(-55, 26.29) * mm, "end": v(-55.2, 26.27) * mm});
            skLineSegment(sketch, "E1022", {"start": v(-55.2, 26.27) * mm, "end": v(-55.36, 26.23) * mm});
            skLineSegment(sketch, "E1023", {"start": v(-55.36, 26.23) * mm, "end": v(-55.47, 26.16) * mm});
            skLineSegment(sketch, "E1024", {"start": v(-55.47, 26.16) * mm, "end": v(-55.5, 26.08) * mm});
            skLineSegment(sketch, "E1025", {"start": v(-55.5, 26.08) * mm, "end": v(-55.47, 26) * mm});
            skLineSegment(sketch, "E1026", {"start": v(-55.47, 26) * mm, "end": v(-55.36, 25.94) * mm});
            skLineSegment(sketch, "E1027", {"start": v(-55.36, 25.94) * mm, "end": v(-55.2, 25.9) * mm});
            skLineSegment(sketch, "E1028", {"start": v(-55.2, 25.9) * mm, "end": v(-55, 25.88) * mm});
            skLineSegment(sketch, "E1029", {"start": v(-55, 25.88) * mm, "end": v(-54.81, 25.9) * mm});
            skLineSegment(sketch, "E1030", {"start": v(-54.81, 25.9) * mm, "end": v(-54.65, 25.94) * mm});
            skLineSegment(sketch, "E1031", {"start": v(-54.65, 25.94) * mm, "end": v(-54.54, 26) * mm});
            skLineSegment(sketch, "E1032", {"start": v(-54.54, 26) * mm, "end": v(-54.5, 26.08) * mm});
            skLineSegment(sketch, "E1033", {"start": v(-54.5, 26.08) * mm, "end": v(-54.54, 26.16) * mm});
            skLineSegment(sketch, "E1034", {"start": v(-54.54, 26.16) * mm, "end": v(-54.65, 26.23) * mm});
            skLineSegment(sketch, "E1035", {"start": v(-54.65, 26.23) * mm, "end": v(-54.81, 26.27) * mm});
            skLineSegment(sketch, "E1036", {"start": v(-54.81, 26.27) * mm, "end": v(-55, 26.29) * mm});
            skLineSegment(sketch, "E1037", {"start": v(-30.66, -1.16) * mm, "end": v(-15.12, -1.16) * mm});
            skLineSegment(sketch, "E1038", {"start": v(-102.28, 3.94) * mm, "end": v(-102.28, 5.2) * mm});
            skLineSegment(sketch, "E1039", {"start": v(-42.59, 3.94) * mm, "end": v(-42.59, 5.2) * mm});
            skLineSegment(sketch, "E1040", {"start": v(-34.14, 3.94) * mm, "end": v(-34.14, 5.2) * mm});
            skLineSegment(sketch, "E1041", {"start": v(-12.47, 3.94) * mm, "end": v(-12.47, 5.2) * mm});
            skLineSegment(sketch, "E1042", {"start": v(-49.97, 5.2) * mm, "end": v(-49.97, 9.02) * mm});
            skLineSegment(sketch, "E1043", {"start": v(-49.97, 9.02) * mm, "end": v(-43.62, 9.02) * mm});
            skLineSegment(sketch, "E1044", {"start": v(-97.47, 5.2) * mm, "end": v(-97.47, 9.02) * mm});
            skLineSegment(sketch, "E1045", {"start": v(-97.47, 9.02) * mm, "end": v(-49.97, 9.02) * mm});
            skLineSegment(sketch, "E1046", {"start": v(-103.82, 9.02) * mm, "end": v(-97.47, 9.02) * mm});
            skLineSegment(sketch, "E1047", {"start": v(-43.62, 19.12) * mm, "end": v(-49.97, 19.12) * mm});
            skLineSegment(sketch, "E1048", {"start": v(-49.97, 19.12) * mm, "end": v(-49.97, 23.88) * mm});
            skLineSegment(sketch, "E1049", {"start": v(-97.47, 19.12) * mm, "end": v(-103.82, 19.12) * mm});
            skLineSegment(sketch, "E1050", {"start": v(-97.47, 19.12) * mm, "end": v(-97.47, 23.88) * mm});
            skLineSegment(sketch, "E1051", {"start": v(-49.97, 19.12) * mm, "end": v(-97.47, 19.12) * mm});
            skLineSegment(sketch, "E1052", {"start": v(-97.47, 19.12) * mm, "end": v(-97.47, 9.02) * mm});
            skLineSegment(sketch, "E1053", {"start": v(-49.97, 19.12) * mm, "end": v(-49.97, 9.02) * mm});
            skLineSegment(sketch, "E1054", {"start": v(-70.13, 24.83) * mm, "end": v(-81.1, 24.83) * mm});
            skLineSegment(sketch, "E1055", {"start": v(-105.8, 10.58) * mm, "end": v(-105.8, 13.97) * mm});
            skLineSegment(sketch, "E1056", {"start": v(-109.13, 9.56) * mm, "end": v(-109.13, 8.91) * mm});
            skLineSegment(sketch, "E1057", {"start": v(-84.99, 44.06) * mm, "end": v(-84.99, 47.06) * mm});
            skLineSegment(sketch, "E1058", {"start": v(-76.4, 44.06) * mm, "end": v(-76.4, 47.06) * mm});
            skLineSegment(sketch, "E1059", {"start": v(-79.1, 44.06) * mm, "end": v(-79.1, 47.06) * mm});
            skLineSegment(sketch, "E1060", {"start": v(-66.78, 44.06) * mm, "end": v(-66.78, 47.06) * mm});
            skLineSegment(sketch, "E1061", {"start": v(-61.7, 42.48) * mm, "end": v(-88.96, 42.48) * mm});
            skLineSegment(sketch, "E1062", {"start": v(-88.96, 33.23) * mm, "end": v(-59.96, 33.23) * mm});
            skLineSegment(sketch, "E1063", {"start": v(-90.17, 31.64) * mm, "end": v(-90.12, 28.64) * mm});
            skLineSegment(sketch, "E1064", {"start": v(-91.68, 27.05) * mm, "end": v(-94.68, 27.05) * mm});
            skLineSegment(sketch, "E1065", {"start": v(-45.73, 28.64) * mm, "end": v(-45.73, 31.64) * mm});
            skLineSegment(sketch, "E1066", {"start": v(-43.44, 31.64) * mm, "end": v(-43.44, 28.64) * mm});
            skLineSegment(sketch, "E1067", {"start": v(-38.85, 27.05) * mm, "end": v(-41.85, 27.05) * mm});
            skLineSegment(sketch, "E1068", {"start": v(-41.85, 18.5) * mm, "end": v(-38.85, 18.5) * mm});
            skLineSegment(sketch, "E1069", {"start": v(-59.96, 33.23) * mm, "end": v(-59.77, 33.23) * mm});
            skLineSegment(sketch, "E1070", {"start": v(-59.77, 36.58) * mm, "end": v(-59.96, 36.58) * mm});
            skArc(sketch, "E1071", {"start": v(-14.31, 14.97) * mm, "mid": v(-16.98, 15.11) * mm, "end": v(-19.65, 15.16) * mm});
            skLineSegment(sketch, "E1072", {"start": v(-26.13, 15.29) * mm, "end": v(-27.67, 15.32) * mm});
            skLineSegment(sketch, "E1073", {"start": v(-27.67, 15.32) * mm, "end": v(-29, 15.36) * mm});
            skLineSegment(sketch, "E1074", {"start": v(-29, 15.36) * mm, "end": v(-30.06, 15.4) * mm});
            skLineSegment(sketch, "E1075", {"start": v(-30.06, 15.4) * mm, "end": v(-30.83, 15.42) * mm});
            skLineSegment(sketch, "E1076", {"start": v(-30.83, 15.42) * mm, "end": v(-31.33, 15.45) * mm});
            skLineSegment(sketch, "E1077", {"start": v(-31.33, 15.45) * mm, "end": v(-31.5, 15.49) * mm});
            skLineSegment(sketch, "E1078", {"start": v(-31.5, 15.49) * mm, "end": v(-31.47, 15.5) * mm});
            skLineSegment(sketch, "E1079", {"start": v(-73.23, 26.53) * mm, "end": v(-73.32, 26.58) * mm});
            skLineSegment(sketch, "E1080", {"start": v(-73.32, 26.58) * mm, "end": v(-73.4, 26.73) * mm});
            skLineSegment(sketch, "E1081", {"start": v(-73.4, 26.73) * mm, "end": v(-73.46, 26.96) * mm});
            skLineSegment(sketch, "E1082", {"start": v(-73.46, 26.96) * mm, "end": v(-73.48, 27.23) * mm});
            skLineSegment(sketch, "E1083", {"start": v(-73.48, 27.23) * mm, "end": v(-73.46, 27.5) * mm});
            skLineSegment(sketch, "E1084", {"start": v(-73.46, 27.5) * mm, "end": v(-73.4, 27.72) * mm});
            skLineSegment(sketch, "E1085", {"start": v(-73.4, 27.72) * mm, "end": v(-73.32, 27.87) * mm});
            skLineSegment(sketch, "E1086", {"start": v(-73.32, 27.87) * mm, "end": v(-73.23, 27.93) * mm});
            skLineSegment(sketch, "E1087", {"start": v(-73.23, 27.93) * mm, "end": v(-73.23, 27.93) * mm});
            skLineSegment(sketch, "E1088", {"start": v(-94.8, 23.88) * mm, "end": v(-94.7, 23.93) * mm});
            skLineSegment(sketch, "E1089", {"start": v(-94.7, 23.93) * mm, "end": v(-94.68, 23.96) * mm});
            skLineSegment(sketch, "E1090", {"start": v(-94.68, 25.2) * mm, "end": v(-94.7, 25.22) * mm});
            skLineSegment(sketch, "E1091", {"start": v(-94.7, 25.22) * mm, "end": v(-94.8, 25.28) * mm});
            skLineSegment(sketch, "E1092", {"start": v(-94.8, 25.28) * mm, "end": v(-94.8, 25.28) * mm});
            skLineSegment(sketch, "E1093", {"start": v(-22.9, 3.13) * mm, "end": v(-34.28, 3.13) * mm});
            skLineSegment(sketch, "E1094", {"start": v(-11.5, 3.13) * mm, "end": v(-22.9, 3.13) * mm});
            skLineSegment(sketch, "E1095", {"start": v(88.1, 45.82) * mm, "end": v(87.96, 45.56) * mm});
            skLineSegment(sketch, "E1096", {"start": v(87.96, 45.56) * mm, "end": v(87.76, 45) * mm});
            skLineSegment(sketch, "E1097", {"start": v(87.76, 45) * mm, "end": v(87.62, 44.37) * mm});
            skLineSegment(sketch, "E1098", {"start": v(87.62, 44.37) * mm, "end": v(87.55, 43.69) * mm});
            skLineSegment(sketch, "E1099", {"start": v(87.55, 43.69) * mm, "end": v(87.55, 42.97) * mm});
            skLineSegment(sketch, "E1100", {"start": v(87.55, 42.97) * mm, "end": v(87.63, 42.21) * mm});
            skLineSegment(sketch, "E1101", {"start": v(87.63, 42.21) * mm, "end": v(87.77, 41.44) * mm});
            skLineSegment(sketch, "E1102", {"start": v(87.77, 41.44) * mm, "end": v(87.98, 40.65) * mm});
            skLineSegment(sketch, "E1103", {"start": v(87.98, 40.65) * mm, "end": v(88.25, 39.85) * mm});
            skLineSegment(sketch, "E1104", {"start": v(88.25, 39.85) * mm, "end": v(88.58, 39.06) * mm});
            skLineSegment(sketch, "E1105", {"start": v(88.58, 39.06) * mm, "end": v(88.97, 38.29) * mm});
            skLineSegment(sketch, "E1106", {"start": v(88.97, 38.29) * mm, "end": v(89.4, 37.54) * mm});
            skLineSegment(sketch, "E1107", {"start": v(89.4, 37.54) * mm, "end": v(89.9, 36.82) * mm});
            skLineSegment(sketch, "E1108", {"start": v(89.9, 36.82) * mm, "end": v(90.42, 36.15) * mm});
            skLineSegment(sketch, "E1109", {"start": v(90.42, 36.15) * mm, "end": v(90.98, 35.53) * mm});
            skLineSegment(sketch, "E1110", {"start": v(90.98, 35.53) * mm, "end": v(91.57, 34.97) * mm});
            skLineSegment(sketch, "E1111", {"start": v(91.57, 34.97) * mm, "end": v(92.17, 34.47) * mm});
            skLineSegment(sketch, "E1112", {"start": v(92.17, 34.47) * mm, "end": v(92.8, 34.05) * mm});
            skLineSegment(sketch, "E1113", {"start": v(92.8, 34.05) * mm, "end": v(93.41, 33.7) * mm});
            skLineSegment(sketch, "E1114", {"start": v(93.41, 33.7) * mm, "end": v(94.04, 33.44) * mm});
            skLineSegment(sketch, "E1115", {"start": v(94.04, 33.44) * mm, "end": v(94.65, 33.27) * mm});
            skLineSegment(sketch, "E1116", {"start": v(94.65, 33.27) * mm, "end": v(95.25, 33.18) * mm});
            skLineSegment(sketch, "E1117", {"start": v(95.25, 33.18) * mm, "end": v(95.4, 33.18) * mm});
            skLineSegment(sketch, "E1118", {"start": v(90.09, 47.52) * mm, "end": v(89.23, 47.02) * mm});
            skLineSegment(sketch, "E1119", {"start": v(97, 33.56) * mm, "end": v(97.86, 34.05) * mm});
            skLineSegment(sketch, "E1120", {"start": v(104.83, 23.02) * mm, "end": v(105.73, 23.54) * mm});
            skArc(sketch, "E1121", {"start": v(83.27, 70.74) * mm, "mid": v(81.89, 75.3) * mm, "end": v(78.63, 78.79) * mm});
            skLineSegment(sketch, "E1122", {"start": v(83.27, 70.74) * mm, "end": v(83.27, 31.96) * mm});
            skLineSegment(sketch, "E1123", {"start": v(45.04, 98.18) * mm, "end": v(78.63, 78.79) * mm});
            skArc(sketch, "E1124", {"start": v(94.2, 78.36) * mm, "mid": v(93.23, 81.86) * mm, "end": v(90.69, 84.43) * mm});
            skLineSegment(sketch, "E1125", {"start": v(94.2, 71.46) * mm, "end": v(94.2, 78.36) * mm});
            skLineSegment(sketch, "E1126", {"start": v(90.69, 84.43) * mm, "end": v(57.1, 103.82) * mm});
            skLineSegment(sketch, "E1127", {"start": v(35.14, 109.81) * mm, "end": v(34.24, 109.3) * mm});
            skArc(sketch, "E1128", {"start": v(83.18, 31.2) * mm, "mid": v(83.25, 31.58) * mm, "end": v(83.27, 31.96) * mm});
            skLineSegment(sketch, "E1129", {"start": v(44.34, 98.48) * mm, "end": v(44.34, 98.48) * mm});
            skLineSegment(sketch, "E1130", {"start": v(44.34, 98.48) * mm, "end": v(44.43, 98.45) * mm});
            skLineSegment(sketch, "E1131", {"start": v(44.43, 98.45) * mm, "end": v(44.6, 98.4) * mm});
            skLineSegment(sketch, "E1132", {"start": v(44.6, 98.4) * mm, "end": v(44.84, 98.29) * mm});
            skLineSegment(sketch, "E1133", {"start": v(44.84, 98.29) * mm, "end": v(45.04, 98.18) * mm});
            skLineSegment(sketch, "E1134", {"start": v(51.55, 103.9) * mm, "end": v(51.09, 103.64) * mm});
            skArc(sketch, "E1135", {"start": v(57.1, 103.82) * mm, "mid": v(54.34, 104.62) * mm, "end": v(51.55, 103.9) * mm});
            skLineSegment(sketch, "E1136", {"start": v(82.5, 73.96) * mm, "end": v(82.32, 74.07) * mm});
            skLineSegment(sketch, "E1137", {"start": v(103.12, 57.11) * mm, "end": v(103.12, 64.62) * mm});
            skLineSegment(sketch, "E1138", {"start": v(93.94, 110.19) * mm, "end": v(96.06, 111.41) * mm});
            skLineSegment(sketch, "E1139", {"start": v(81.32, 134.1) * mm, "end": v(79.2, 132.88) * mm});
            skLineSegment(sketch, "E1140", {"start": v(110.46, 40.49) * mm, "end": v(111.5, 41.09) * mm});
            skLineSegment(sketch, "E1141", {"start": v(111.6, 40.91) * mm, "end": v(112.3, 41.32) * mm});
            skLineSegment(sketch, "E1142", {"start": v(104.8, 57.57) * mm, "end": v(103.39, 56.76) * mm});
            skLineSegment(sketch, "E1143", {"start": v(112.51, 35.44) * mm, "end": v(113.93, 36.26) * mm});
            skLineSegment(sketch, "E1144", {"start": v(65.24, 50.14) * mm, "end": v(66.39, 50.03) * mm});
            skLineSegment(sketch, "E1145", {"start": v(42.43, 93.47) * mm, "end": v(42.43, 70.45) * mm});
            skLineSegment(sketch, "E1146", {"start": v(89.79, 51.4) * mm, "end": v(89.38, 51.02) * mm});
            skLineSegment(sketch, "E1147", {"start": v(89.38, 51.02) * mm, "end": v(88.84, 50.38) * mm});
            skLineSegment(sketch, "E1148", {"start": v(88.84, 50.38) * mm, "end": v(88.36, 49.68) * mm});
            skLineSegment(sketch, "E1149", {"start": v(88.36, 49.68) * mm, "end": v(87.96, 48.94) * mm});
            skLineSegment(sketch, "E1150", {"start": v(87.96, 48.94) * mm, "end": v(87.63, 48.15) * mm});
            skLineSegment(sketch, "E1151", {"start": v(87.63, 48.15) * mm, "end": v(87.38, 47.31) * mm});
            skLineSegment(sketch, "E1152", {"start": v(87.38, 47.31) * mm, "end": v(87.2, 46.43) * mm});
            skLineSegment(sketch, "E1153", {"start": v(87.2, 46.43) * mm, "end": v(87.1, 45.51) * mm});
            skLineSegment(sketch, "E1154", {"start": v(87.1, 45.51) * mm, "end": v(87.09, 44.56) * mm});
            skLineSegment(sketch, "E1155", {"start": v(87.09, 44.56) * mm, "end": v(87.16, 43.57) * mm});
            skLineSegment(sketch, "E1156", {"start": v(87.16, 43.57) * mm, "end": v(87.3, 42.56) * mm});
            skLineSegment(sketch, "E1157", {"start": v(87.3, 42.56) * mm, "end": v(87.54, 41.55) * mm});
            skLineSegment(sketch, "E1158", {"start": v(87.54, 41.55) * mm, "end": v(87.86, 40.55) * mm});
            skLineSegment(sketch, "E1159", {"start": v(87.86, 40.55) * mm, "end": v(88.24, 39.57) * mm});
            skLineSegment(sketch, "E1160", {"start": v(88.24, 39.57) * mm, "end": v(88.7, 38.6) * mm});
            skLineSegment(sketch, "E1161", {"start": v(88.7, 38.6) * mm, "end": v(89.21, 37.68) * mm});
            skLineSegment(sketch, "E1162", {"start": v(89.21, 37.68) * mm, "end": v(89.8, 36.8) * mm});
            skLineSegment(sketch, "E1163", {"start": v(89.8, 36.8) * mm, "end": v(90.43, 35.94) * mm});
            skLineSegment(sketch, "E1164", {"start": v(90.43, 35.94) * mm, "end": v(91.13, 35.14) * mm});
            skLineSegment(sketch, "E1165", {"start": v(91.13, 35.14) * mm, "end": v(91.89, 34.39) * mm});
            skLineSegment(sketch, "E1166", {"start": v(91.89, 34.39) * mm, "end": v(92.7, 33.7) * mm});
            skLineSegment(sketch, "E1167", {"start": v(92.7, 33.7) * mm, "end": v(93.57, 33.08) * mm});
            skLineSegment(sketch, "E1168", {"start": v(93.57, 33.08) * mm, "end": v(94.5, 32.55) * mm});
            skLineSegment(sketch, "E1169", {"start": v(94.5, 32.55) * mm, "end": v(95.34, 32.16) * mm});
            skLineSegment(sketch, "E1170", {"start": v(95.34, 32.16) * mm, "end": v(96.2, 31.85) * mm});
            skLineSegment(sketch, "E1171", {"start": v(96.2, 31.85) * mm, "end": v(97.05, 31.64) * mm});
            skLineSegment(sketch, "E1172", {"start": v(97.05, 31.64) * mm, "end": v(97.9, 31.51) * mm});
            skLineSegment(sketch, "E1173", {"start": v(97.9, 31.51) * mm, "end": v(98.74, 31.48) * mm});
            skLineSegment(sketch, "E1174", {"start": v(98.74, 31.48) * mm, "end": v(99.57, 31.52) * mm});
            skLineSegment(sketch, "E1175", {"start": v(99.57, 31.52) * mm, "end": v(100.47, 31.67) * mm});
            skLineSegment(sketch, "E1176", {"start": v(100.47, 31.67) * mm, "end": v(101.08, 31.85) * mm});
            skLineSegment(sketch, "E1177", {"start": v(101.1, 31.86) * mm, "end": v(101.46, 31.98) * mm});
            skLineSegment(sketch, "E1178", {"start": v(101.46, 31.98) * mm, "end": v(102.04, 32.28) * mm});
            skLineSegment(sketch, "E1179", {"start": v(102.04, 32.28) * mm, "end": v(102.56, 32.66) * mm});
            skLineSegment(sketch, "E1180", {"start": v(102.56, 32.66) * mm, "end": v(103.03, 33.12) * mm});
            skLineSegment(sketch, "E1181", {"start": v(103.03, 33.12) * mm, "end": v(103.43, 33.65) * mm});
            skLineSegment(sketch, "E1182", {"start": v(103.43, 33.65) * mm, "end": v(103.78, 34.25) * mm});
            skLineSegment(sketch, "E1183", {"start": v(103.78, 34.25) * mm, "end": v(104.06, 34.92) * mm});
            skLineSegment(sketch, "E1184", {"start": v(104.06, 34.92) * mm, "end": v(104.27, 35.65) * mm});
            skLineSegment(sketch, "E1185", {"start": v(104.27, 35.65) * mm, "end": v(104.42, 36.44) * mm});
            skLineSegment(sketch, "E1186", {"start": v(104.42, 36.44) * mm, "end": v(104.49, 37.28) * mm});
            skLineSegment(sketch, "E1187", {"start": v(104.49, 37.28) * mm, "end": v(104.5, 38.16) * mm});
            skLineSegment(sketch, "E1188", {"start": v(104.5, 38.16) * mm, "end": v(104.42, 39.08) * mm});
            skLineSegment(sketch, "E1189", {"start": v(104.42, 39.08) * mm, "end": v(104.28, 40.01) * mm});
            skLineSegment(sketch, "E1190", {"start": v(104.28, 40.01) * mm, "end": v(104.07, 40.97) * mm});
            skLineSegment(sketch, "E1191", {"start": v(104.07, 40.97) * mm, "end": v(103.8, 41.93) * mm});
            skLineSegment(sketch, "E1192", {"start": v(103.8, 41.93) * mm, "end": v(103.45, 42.9) * mm});
            skLineSegment(sketch, "E1193", {"start": v(103.45, 42.9) * mm, "end": v(103.05, 43.85) * mm});
            skLineSegment(sketch, "E1194", {"start": v(103.05, 43.85) * mm, "end": v(102.6, 44.8) * mm});
            skLineSegment(sketch, "E1195", {"start": v(102.6, 44.8) * mm, "end": v(102.08, 45.71) * mm});
            skLineSegment(sketch, "E1196", {"start": v(102.08, 45.71) * mm, "end": v(101.52, 46.6) * mm});
            skLineSegment(sketch, "E1197", {"start": v(101.52, 46.6) * mm, "end": v(100.92, 47.45) * mm});
            skLineSegment(sketch, "E1198", {"start": v(100.92, 47.45) * mm, "end": v(100.28, 48.26) * mm});
            skLineSegment(sketch, "E1199", {"start": v(100.28, 48.26) * mm, "end": v(99.6, 49.01) * mm});
            skLineSegment(sketch, "E1200", {"start": v(99.6, 49.01) * mm, "end": v(98.9, 49.7) * mm});
            skLineSegment(sketch, "E1201", {"start": v(98.9, 49.7) * mm, "end": v(98.16, 50.34) * mm});
            skLineSegment(sketch, "E1202", {"start": v(98.16, 50.34) * mm, "end": v(97.41, 50.9) * mm});
            skLineSegment(sketch, "E1203", {"start": v(97.41, 50.9) * mm, "end": v(96.7, 51.37) * mm});
            skLineSegment(sketch, "E1204", {"start": v(96.7, 51.37) * mm, "end": v(96.58, 51.43) * mm});
            skLineSegment(sketch, "E1205", {"start": v(96.58, 51.43) * mm, "end": v(96.18, 51.66) * mm});
            skLineSegment(sketch, "E1206", {"start": v(96.18, 51.66) * mm, "end": v(95.4, 52.01) * mm});
            skLineSegment(sketch, "E1207", {"start": v(95.4, 52.01) * mm, "end": v(94.64, 52.28) * mm});
            skLineSegment(sketch, "E1208", {"start": v(94.64, 52.28) * mm, "end": v(93.88, 52.46) * mm});
            skLineSegment(sketch, "E1209", {"start": v(93.88, 52.46) * mm, "end": v(93.14, 52.55) * mm});
            skLineSegment(sketch, "E1210", {"start": v(93.14, 52.55) * mm, "end": v(92.43, 52.54) * mm});
            skLineSegment(sketch, "E1211", {"start": v(92.43, 52.54) * mm, "end": v(91.76, 52.44) * mm});
            skLineSegment(sketch, "E1212", {"start": v(91.76, 52.44) * mm, "end": v(91.12, 52.25) * mm});
            skLineSegment(sketch, "E1213", {"start": v(91.12, 52.25) * mm, "end": v(90.54, 51.97) * mm});
            skLineSegment(sketch, "E1214", {"start": v(90.54, 51.97) * mm, "end": v(90, 51.6) * mm});
            skLineSegment(sketch, "E1215", {"start": v(90, 51.6) * mm, "end": v(89.7, 51.32) * mm});
            skLineSegment(sketch, "E1216", {"start": v(80.7, 72.5) * mm, "end": v(80.92, 73.26) * mm});
            skLineSegment(sketch, "E1217", {"start": v(92.23, 38.57) * mm, "end": v(92.23, 37.94) * mm});
            skLineSegment(sketch, "E1218", {"start": v(92.23, 37.94) * mm, "end": v(93.82, 37.03) * mm});
            skLineSegment(sketch, "E1219", {"start": v(92.23, 43.53) * mm, "end": v(92.23, 43.03) * mm});
            skArc(sketch, "E1220", {"start": v(95.49, 33.2) * mm, "mid": v(96.99, 33.56) * mm, "end": v(98.06, 34.67) * mm});
            skArc(sketch, "E1221", {"start": v(90.73, 47.39) * mm, "mid": v(89.23, 47.01) * mm, "end": v(88.16, 45.89) * mm});
            skLineSegment(sketch, "E1222", {"start": v(93.82, 42.62) * mm, "end": v(92.05, 43.64) * mm});
            skLineSegment(sketch, "E1223", {"start": v(92.05, 43.64) * mm, "end": v(92.05, 35.27) * mm});
            skLineSegment(sketch, "E1224", {"start": v(92.05, 35.27) * mm, "end": v(93.82, 34.25) * mm});
            skLineSegment(sketch, "E1225", {"start": v(93.82, 34.25) * mm, "end": v(93.82, 37.45) * mm});
            skLineSegment(sketch, "E1226", {"start": v(93.82, 37.45) * mm, "end": v(94.17, 37.48) * mm});
            skLineSegment(sketch, "E1227", {"start": v(94.17, 37.48) * mm, "end": v(94.47, 37.61) * mm});
            skLineSegment(sketch, "E1228", {"start": v(94.47, 37.61) * mm, "end": v(94.72, 37.83) * mm});
            skLineSegment(sketch, "E1229", {"start": v(94.72, 37.83) * mm, "end": v(94.9, 38.14) * mm});
            skLineSegment(sketch, "E1230", {"start": v(94.9, 38.14) * mm, "end": v(95.02, 38.52) * mm});
            skLineSegment(sketch, "E1231", {"start": v(95.02, 38.52) * mm, "end": v(95.06, 38.96) * mm});
            skLineSegment(sketch, "E1232", {"start": v(95.06, 38.96) * mm, "end": v(95.02, 39.45) * mm});
            skLineSegment(sketch, "E1233", {"start": v(95.02, 39.45) * mm, "end": v(94.9, 39.96) * mm});
            skLineSegment(sketch, "E1234", {"start": v(94.9, 39.96) * mm, "end": v(94.72, 40.48) * mm});
            skLineSegment(sketch, "E1235", {"start": v(94.72, 40.48) * mm, "end": v(94.47, 40.99) * mm});
            skLineSegment(sketch, "E1236", {"start": v(94.47, 40.99) * mm, "end": v(94.17, 41.47) * mm});
            skLineSegment(sketch, "E1237", {"start": v(94.17, 41.47) * mm, "end": v(93.82, 41.9) * mm});
            skLineSegment(sketch, "E1238", {"start": v(93.82, 41.9) * mm, "end": v(93.82, 42.62) * mm});
            skArc(sketch, "E1239", {"start": v(93.82, 37.45) * mm, "mid": v(94.5, 39.07) * mm, "end": v(94.56, 40.83) * mm});
            skLineSegment(sketch, "E1240", {"start": v(92.23, 35.37) * mm, "end": v(92.05, 35.27) * mm});
            skLineSegment(sketch, "E1241", {"start": v(92.23, 35.37) * mm, "end": v(92.23, 43.53) * mm});
            skLineSegment(sketch, "E1242", {"start": v(93.82, 34.45) * mm, "end": v(92.23, 35.37) * mm});
            skLineSegment(sketch, "E1243", {"start": v(97.5, 62.05) * mm, "end": v(97.45, 62.52) * mm});
            skLineSegment(sketch, "E1244", {"start": v(97.45, 62.52) * mm, "end": v(97.33, 63.01) * mm});
            skLineSegment(sketch, "E1245", {"start": v(97.33, 63.01) * mm, "end": v(97.14, 63.51) * mm});
            skLineSegment(sketch, "E1246", {"start": v(97.14, 63.51) * mm, "end": v(96.88, 64) * mm});
            skLineSegment(sketch, "E1247", {"start": v(96.88, 64) * mm, "end": v(96.56, 64.44) * mm});
            skLineSegment(sketch, "E1248", {"start": v(96.56, 64.44) * mm, "end": v(96.2, 64.83) * mm});
            skLineSegment(sketch, "E1249", {"start": v(96.2, 64.83) * mm, "end": v(95.83, 65.14) * mm});
            skLineSegment(sketch, "E1250", {"start": v(95.83, 65.14) * mm, "end": v(95.44, 65.36) * mm});
            skLineSegment(sketch, "E1251", {"start": v(95.44, 65.36) * mm, "end": v(95.06, 65.49) * mm});
            skLineSegment(sketch, "E1252", {"start": v(95.06, 65.49) * mm, "end": v(94.7, 65.51) * mm});
            skLineSegment(sketch, "E1253", {"start": v(94.7, 65.51) * mm, "end": v(94.4, 65.43) * mm});
            skLineSegment(sketch, "E1254", {"start": v(94.4, 65.43) * mm, "end": v(94.13, 65.24) * mm});
            skLineSegment(sketch, "E1255", {"start": v(94.13, 65.24) * mm, "end": v(93.94, 64.97) * mm});
            skLineSegment(sketch, "E1256", {"start": v(93.94, 64.97) * mm, "end": v(93.82, 64.61) * mm});
            skLineSegment(sketch, "E1257", {"start": v(93.82, 64.61) * mm, "end": v(93.78, 64.19) * mm});
            skLineSegment(sketch, "E1258", {"start": v(93.78, 64.19) * mm, "end": v(93.82, 63.72) * mm});
            skLineSegment(sketch, "E1259", {"start": v(93.82, 63.72) * mm, "end": v(93.94, 63.23) * mm});
            skLineSegment(sketch, "E1260", {"start": v(93.94, 63.23) * mm, "end": v(94.13, 62.73) * mm});
            skLineSegment(sketch, "E1261", {"start": v(94.13, 62.73) * mm, "end": v(94.4, 62.24) * mm});
            skLineSegment(sketch, "E1262", {"start": v(94.4, 62.24) * mm, "end": v(94.7, 61.8) * mm});
            skLineSegment(sketch, "E1263", {"start": v(94.7, 61.8) * mm, "end": v(95.06, 61.41) * mm});
            skLineSegment(sketch, "E1264", {"start": v(95.06, 61.41) * mm, "end": v(95.44, 61.1) * mm});
            skLineSegment(sketch, "E1265", {"start": v(95.44, 61.1) * mm, "end": v(95.83, 60.87) * mm});
            skLineSegment(sketch, "E1266", {"start": v(95.83, 60.87) * mm, "end": v(96.2, 60.75) * mm});
            skLineSegment(sketch, "E1267", {"start": v(96.2, 60.75) * mm, "end": v(96.56, 60.73) * mm});
            skLineSegment(sketch, "E1268", {"start": v(96.56, 60.73) * mm, "end": v(96.88, 60.8) * mm});
            skLineSegment(sketch, "E1269", {"start": v(96.88, 60.8) * mm, "end": v(97.14, 61) * mm});
            skLineSegment(sketch, "E1270", {"start": v(97.14, 61) * mm, "end": v(97.33, 61.27) * mm});
            skLineSegment(sketch, "E1271", {"start": v(97.33, 61.27) * mm, "end": v(97.45, 61.62) * mm});
            skLineSegment(sketch, "E1272", {"start": v(97.45, 61.62) * mm, "end": v(97.5, 62.05) * mm});
            skLineSegment(sketch, "E1273", {"start": v(42.71, 43.8) * mm, "end": v(42.67, 44.26) * mm});
            skLineSegment(sketch, "E1274", {"start": v(42.67, 44.26) * mm, "end": v(42.55, 44.75) * mm});
            skLineSegment(sketch, "E1275", {"start": v(42.55, 44.75) * mm, "end": v(42.36, 45.25) * mm});
            skLineSegment(sketch, "E1276", {"start": v(42.36, 45.25) * mm, "end": v(42.1, 45.74) * mm});
            skLineSegment(sketch, "E1277", {"start": v(42.1, 45.74) * mm, "end": v(41.78, 46.18) * mm});
            skLineSegment(sketch, "E1278", {"start": v(41.78, 46.18) * mm, "end": v(41.43, 46.57) * mm});
            skLineSegment(sketch, "E1279", {"start": v(41.43, 46.57) * mm, "end": v(41.05, 46.88) * mm});
            skLineSegment(sketch, "E1280", {"start": v(41.05, 46.88) * mm, "end": v(40.66, 47.1) * mm});
            skLineSegment(sketch, "E1281", {"start": v(40.66, 47.1) * mm, "end": v(40.28, 47.23) * mm});
            skLineSegment(sketch, "E1282", {"start": v(40.28, 47.23) * mm, "end": v(39.93, 47.25) * mm});
            skLineSegment(sketch, "E1283", {"start": v(39.93, 47.25) * mm, "end": v(39.61, 47.17) * mm});
            skLineSegment(sketch, "E1284", {"start": v(39.61, 47.17) * mm, "end": v(39.35, 46.99) * mm});
            skLineSegment(sketch, "E1285", {"start": v(39.35, 46.99) * mm, "end": v(39.16, 46.71) * mm});
            skLineSegment(sketch, "E1286", {"start": v(39.16, 46.71) * mm, "end": v(39.04, 46.36) * mm});
            skLineSegment(sketch, "E1287", {"start": v(39.04, 46.36) * mm, "end": v(39, 45.93) * mm});
            skLineSegment(sketch, "E1288", {"start": v(39, 45.93) * mm, "end": v(39.04, 45.46) * mm});
            skLineSegment(sketch, "E1289", {"start": v(39.04, 45.46) * mm, "end": v(39.16, 44.97) * mm});
            skLineSegment(sketch, "E1290", {"start": v(39.16, 44.97) * mm, "end": v(39.35, 44.47) * mm});
            skLineSegment(sketch, "E1291", {"start": v(39.35, 44.47) * mm, "end": v(39.61, 43.99) * mm});
            skLineSegment(sketch, "E1292", {"start": v(39.61, 43.99) * mm, "end": v(39.93, 43.54) * mm});
            skLineSegment(sketch, "E1293", {"start": v(39.93, 43.54) * mm, "end": v(40.28, 43.15) * mm});
            skLineSegment(sketch, "E1294", {"start": v(40.28, 43.15) * mm, "end": v(40.66, 42.84) * mm});
            skLineSegment(sketch, "E1295", {"start": v(40.66, 42.84) * mm, "end": v(41.05, 42.62) * mm});
            skLineSegment(sketch, "E1296", {"start": v(41.05, 42.62) * mm, "end": v(41.43, 42.5) * mm});
            skLineSegment(sketch, "E1297", {"start": v(41.43, 42.5) * mm, "end": v(41.78, 42.47) * mm});
            skLineSegment(sketch, "E1298", {"start": v(41.78, 42.47) * mm, "end": v(42.1, 42.55) * mm});
            skLineSegment(sketch, "E1299", {"start": v(42.1, 42.55) * mm, "end": v(42.36, 42.73) * mm});
            skLineSegment(sketch, "E1300", {"start": v(42.36, 42.73) * mm, "end": v(42.55, 43.01) * mm});
            skLineSegment(sketch, "E1301", {"start": v(42.55, 43.01) * mm, "end": v(42.67, 43.37) * mm});
            skLineSegment(sketch, "E1302", {"start": v(42.67, 43.37) * mm, "end": v(42.71, 43.8) * mm});
            skLineSegment(sketch, "E1303", {"start": v(88.77, 15.7) * mm, "end": v(104.09, 22.64) * mm});
            skArc(sketch, "E1304", {"start": v(82.8, 16.53) * mm, "mid": v(85.68, 15.4) * mm, "end": v(88.77, 15.7) * mm});
            skLineSegment(sketch, "E1305", {"start": v(40.59, 40.9) * mm, "end": v(82.8, 16.53) * mm});
            skArc(sketch, "E1306", {"start": v(31.6, 56.45) * mm, "mid": v(34.2, 47.58) * mm, "end": v(40.59, 40.9) * mm});
            skLineSegment(sketch, "E1307", {"start": v(31.6, 103.48) * mm, "end": v(31.6, 56.45) * mm});
            skLineSegment(sketch, "E1308", {"start": v(40.59, 108.66) * mm, "end": v(39.76, 109.1) * mm});
            skLineSegment(sketch, "E1309", {"start": v(39.76, 109.1) * mm, "end": v(38.94, 109.44) * mm});
            skLineSegment(sketch, "E1310", {"start": v(38.94, 109.44) * mm, "end": v(38.13, 109.69) * mm});
            skLineSegment(sketch, "E1311", {"start": v(38.13, 109.69) * mm, "end": v(37.34, 109.84) * mm});
            skLineSegment(sketch, "E1312", {"start": v(37.34, 109.84) * mm, "end": v(36.58, 109.89) * mm});
            skLineSegment(sketch, "E1313", {"start": v(36.58, 109.89) * mm, "end": v(35.86, 109.84) * mm});
            skLineSegment(sketch, "E1314", {"start": v(35.86, 109.84) * mm, "end": v(35.17, 109.7) * mm});
            skLineSegment(sketch, "E1315", {"start": v(35.17, 109.7) * mm, "end": v(34.54, 109.45) * mm});
            skLineSegment(sketch, "E1316", {"start": v(34.54, 109.45) * mm, "end": v(33.95, 109.11) * mm});
            skLineSegment(sketch, "E1317", {"start": v(33.95, 109.11) * mm, "end": v(33.42, 108.68) * mm});
            skLineSegment(sketch, "E1318", {"start": v(33.42, 108.68) * mm, "end": v(32.95, 108.16) * mm});
            skLineSegment(sketch, "E1319", {"start": v(32.95, 108.16) * mm, "end": v(32.55, 107.56) * mm});
            skLineSegment(sketch, "E1320", {"start": v(32.55, 107.56) * mm, "end": v(32.21, 106.87) * mm});
            skLineSegment(sketch, "E1321", {"start": v(32.21, 106.87) * mm, "end": v(31.95, 106.12) * mm});
            skLineSegment(sketch, "E1322", {"start": v(31.95, 106.12) * mm, "end": v(31.76, 105.3) * mm});
            skLineSegment(sketch, "E1323", {"start": v(31.76, 105.3) * mm, "end": v(31.64, 104.41) * mm});
            skLineSegment(sketch, "E1324", {"start": v(31.64, 104.41) * mm, "end": v(31.6, 103.48) * mm});
            skLineSegment(sketch, "E1325", {"start": v(82.8, 84.3) * mm, "end": v(40.59, 108.66) * mm});
            skArc(sketch, "E1326", {"start": v(88.77, 78.22) * mm, "mid": v(86.15, 81.62) * mm, "end": v(82.8, 84.3) * mm});
            skLineSegment(sketch, "E1327", {"start": v(104.09, 53.6) * mm, "end": v(88.77, 78.22) * mm});
            skLineSegment(sketch, "E1328", {"start": v(104.09, 22.64) * mm, "end": v(104.96, 23.1) * mm});
            skLineSegment(sketch, "E1329", {"start": v(104.96, 23.1) * mm, "end": v(105.78, 23.66) * mm});
            skLineSegment(sketch, "E1330", {"start": v(105.78, 23.66) * mm, "end": v(106.54, 24.32) * mm});
            skLineSegment(sketch, "E1331", {"start": v(106.54, 24.32) * mm, "end": v(107.23, 25.07) * mm});
            skLineSegment(sketch, "E1332", {"start": v(107.23, 25.07) * mm, "end": v(107.85, 25.9) * mm});
            skLineSegment(sketch, "E1333", {"start": v(107.85, 25.9) * mm, "end": v(108.4, 26.83) * mm});
            skLineSegment(sketch, "E1334", {"start": v(108.4, 26.83) * mm, "end": v(108.87, 27.84) * mm});
            skLineSegment(sketch, "E1335", {"start": v(108.87, 27.84) * mm, "end": v(109.27, 28.93) * mm});
            skLineSegment(sketch, "E1336", {"start": v(109.27, 28.93) * mm, "end": v(109.6, 30.1) * mm});
            skLineSegment(sketch, "E1337", {"start": v(109.6, 30.1) * mm, "end": v(109.84, 31.32) * mm});
            skLineSegment(sketch, "E1338", {"start": v(109.84, 31.32) * mm, "end": v(110, 32.61) * mm});
            skLineSegment(sketch, "E1339", {"start": v(110, 32.61) * mm, "end": v(110.08, 33.96) * mm});
            skLineSegment(sketch, "E1340", {"start": v(110.08, 33.96) * mm, "end": v(110.08, 35.36) * mm});
            skLineSegment(sketch, "E1341", {"start": v(110.08, 35.36) * mm, "end": v(110, 36.8) * mm});
            skLineSegment(sketch, "E1342", {"start": v(110, 36.8) * mm, "end": v(109.84, 38.28) * mm});
            skLineSegment(sketch, "E1343", {"start": v(109.84, 38.28) * mm, "end": v(109.6, 39.79) * mm});
            skLineSegment(sketch, "E1344", {"start": v(109.6, 39.79) * mm, "end": v(109.27, 41.32) * mm});
            skLineSegment(sketch, "E1345", {"start": v(109.27, 41.32) * mm, "end": v(108.87, 42.87) * mm});
            skLineSegment(sketch, "E1346", {"start": v(108.87, 42.87) * mm, "end": v(108.4, 44.43) * mm});
            skLineSegment(sketch, "E1347", {"start": v(108.4, 44.43) * mm, "end": v(107.85, 46) * mm});
            skLineSegment(sketch, "E1348", {"start": v(107.85, 46) * mm, "end": v(107.23, 47.55) * mm});
            skLineSegment(sketch, "E1349", {"start": v(107.23, 47.55) * mm, "end": v(106.54, 49.1) * mm});
            skLineSegment(sketch, "E1350", {"start": v(106.54, 49.1) * mm, "end": v(105.78, 50.63) * mm});
            skLineSegment(sketch, "E1351", {"start": v(105.78, 50.63) * mm, "end": v(104.96, 52.13) * mm});
            skLineSegment(sketch, "E1352", {"start": v(104.96, 52.13) * mm, "end": v(104.09, 53.6) * mm});
            skLineSegment(sketch, "E1353", {"start": v(42.71, 103.31) * mm, "end": v(42.67, 103.78) * mm});
            skLineSegment(sketch, "E1354", {"start": v(42.67, 103.78) * mm, "end": v(42.55, 104.28) * mm});
            skLineSegment(sketch, "E1355", {"start": v(42.55, 104.28) * mm, "end": v(42.36, 104.78) * mm});
            skLineSegment(sketch, "E1356", {"start": v(42.36, 104.78) * mm, "end": v(42.1, 105.26) * mm});
            skLineSegment(sketch, "E1357", {"start": v(42.1, 105.26) * mm, "end": v(41.78, 105.7) * mm});
            skLineSegment(sketch, "E1358", {"start": v(41.78, 105.7) * mm, "end": v(41.43, 106.1) * mm});
            skLineSegment(sketch, "E1359", {"start": v(41.43, 106.1) * mm, "end": v(41.05, 106.4) * mm});
            skLineSegment(sketch, "E1360", {"start": v(41.05, 106.4) * mm, "end": v(40.66, 106.63) * mm});
            skLineSegment(sketch, "E1361", {"start": v(40.66, 106.63) * mm, "end": v(40.28, 106.76) * mm});
            skLineSegment(sketch, "E1362", {"start": v(40.28, 106.76) * mm, "end": v(39.93, 106.78) * mm});
            skLineSegment(sketch, "E1363", {"start": v(39.93, 106.78) * mm, "end": v(39.61, 106.7) * mm});
            skLineSegment(sketch, "E1364", {"start": v(39.61, 106.7) * mm, "end": v(39.35, 106.51) * mm});
            skLineSegment(sketch, "E1365", {"start": v(39.35, 106.51) * mm, "end": v(39.16, 106.24) * mm});
            skLineSegment(sketch, "E1366", {"start": v(39.16, 106.24) * mm, "end": v(39.04, 105.88) * mm});
            skLineSegment(sketch, "E1367", {"start": v(39.04, 105.88) * mm, "end": v(39, 105.46) * mm});
            skLineSegment(sketch, "E1368", {"start": v(39, 105.46) * mm, "end": v(39.04, 104.99) * mm});
            skLineSegment(sketch, "E1369", {"start": v(39.04, 104.99) * mm, "end": v(39.16, 104.5) * mm});
            skLineSegment(sketch, "E1370", {"start": v(39.16, 104.5) * mm, "end": v(39.35, 104) * mm});
            skLineSegment(sketch, "E1371", {"start": v(39.35, 104) * mm, "end": v(39.61, 103.51) * mm});
            skLineSegment(sketch, "E1372", {"start": v(39.61, 103.51) * mm, "end": v(39.93, 103.07) * mm});
            skLineSegment(sketch, "E1373", {"start": v(39.93, 103.07) * mm, "end": v(40.28, 102.68) * mm});
            skLineSegment(sketch, "E1374", {"start": v(40.28, 102.68) * mm, "end": v(40.66, 102.37) * mm});
            skLineSegment(sketch, "E1375", {"start": v(40.66, 102.37) * mm, "end": v(41.05, 102.14) * mm});
            skLineSegment(sketch, "E1376", {"start": v(41.05, 102.14) * mm, "end": v(41.43, 102.02) * mm});
            skLineSegment(sketch, "E1377", {"start": v(41.43, 102.02) * mm, "end": v(41.78, 102) * mm});
            skLineSegment(sketch, "E1378", {"start": v(41.78, 102) * mm, "end": v(42.1, 102.08) * mm});
            skLineSegment(sketch, "E1379", {"start": v(42.1, 102.08) * mm, "end": v(42.36, 102.26) * mm});
            skLineSegment(sketch, "E1380", {"start": v(42.36, 102.26) * mm, "end": v(42.55, 102.54) * mm});
            skLineSegment(sketch, "E1381", {"start": v(42.55, 102.54) * mm, "end": v(42.67, 102.9) * mm});
            skLineSegment(sketch, "E1382", {"start": v(42.67, 102.9) * mm, "end": v(42.71, 103.31) * mm});
            skLineSegment(sketch, "E1383", {"start": v(97.5, 21.81) * mm, "end": v(97.45, 22.28) * mm});
            skLineSegment(sketch, "E1384", {"start": v(97.45, 22.28) * mm, "end": v(97.33, 22.78) * mm});
            skLineSegment(sketch, "E1385", {"start": v(97.33, 22.78) * mm, "end": v(97.14, 23.28) * mm});
            skLineSegment(sketch, "E1386", {"start": v(97.14, 23.28) * mm, "end": v(96.88, 23.76) * mm});
            skLineSegment(sketch, "E1387", {"start": v(96.88, 23.76) * mm, "end": v(96.56, 24.2) * mm});
            skLineSegment(sketch, "E1388", {"start": v(96.56, 24.2) * mm, "end": v(96.2, 24.59) * mm});
            skLineSegment(sketch, "E1389", {"start": v(96.2, 24.59) * mm, "end": v(95.83, 24.9) * mm});
            skLineSegment(sketch, "E1390", {"start": v(95.83, 24.9) * mm, "end": v(95.44, 25.13) * mm});
            skLineSegment(sketch, "E1391", {"start": v(95.44, 25.13) * mm, "end": v(95.06, 25.25) * mm});
            skLineSegment(sketch, "E1392", {"start": v(95.06, 25.25) * mm, "end": v(94.7, 25.27) * mm});
            skLineSegment(sketch, "E1393", {"start": v(94.7, 25.27) * mm, "end": v(94.4, 25.2) * mm});
            skLineSegment(sketch, "E1394", {"start": v(94.4, 25.2) * mm, "end": v(94.13, 25) * mm});
            skLineSegment(sketch, "E1395", {"start": v(94.13, 25) * mm, "end": v(93.94, 24.73) * mm});
            skLineSegment(sketch, "E1396", {"start": v(93.94, 24.73) * mm, "end": v(93.82, 24.38) * mm});
            skLineSegment(sketch, "E1397", {"start": v(93.82, 24.38) * mm, "end": v(93.78, 23.95) * mm});
            skLineSegment(sketch, "E1398", {"start": v(93.78, 23.95) * mm, "end": v(93.82, 23.48) * mm});
            skLineSegment(sketch, "E1399", {"start": v(93.82, 23.48) * mm, "end": v(93.94, 22.99) * mm});
            skLineSegment(sketch, "E1400", {"start": v(93.94, 22.99) * mm, "end": v(94.13, 22.49) * mm});
            skLineSegment(sketch, "E1401", {"start": v(94.13, 22.49) * mm, "end": v(94.4, 22) * mm});
            skLineSegment(sketch, "E1402", {"start": v(94.4, 22) * mm, "end": v(94.7, 21.56) * mm});
            skLineSegment(sketch, "E1403", {"start": v(94.7, 21.56) * mm, "end": v(95.06, 21.17) * mm});
            skLineSegment(sketch, "E1404", {"start": v(95.06, 21.17) * mm, "end": v(95.44, 20.86) * mm});
            skLineSegment(sketch, "E1405", {"start": v(95.44, 20.86) * mm, "end": v(95.83, 20.64) * mm});
            skLineSegment(sketch, "E1406", {"start": v(95.83, 20.64) * mm, "end": v(96.2, 20.51) * mm});
            skLineSegment(sketch, "E1407", {"start": v(96.2, 20.51) * mm, "end": v(96.56, 20.5) * mm});
            skLineSegment(sketch, "E1408", {"start": v(96.56, 20.5) * mm, "end": v(96.88, 20.57) * mm});
            skLineSegment(sketch, "E1409", {"start": v(96.88, 20.57) * mm, "end": v(97.14, 20.76) * mm});
            skLineSegment(sketch, "E1410", {"start": v(97.14, 20.76) * mm, "end": v(97.33, 21.03) * mm});
            skLineSegment(sketch, "E1411", {"start": v(97.33, 21.03) * mm, "end": v(97.45, 21.39) * mm});
            skLineSegment(sketch, "E1412", {"start": v(97.45, 21.39) * mm, "end": v(97.5, 21.81) * mm});
            skLineSegment(sketch, "E1413", {"start": v(104.99, 54.12) * mm, "end": v(89.67, 78.73) * mm});
            skLineSegment(sketch, "E1414", {"start": v(105.73, 23.54) * mm, "end": v(105.86, 23.62) * mm});
            skLineSegment(sketch, "E1415", {"start": v(105.86, 23.62) * mm, "end": v(106.68, 24.18) * mm});
            skLineSegment(sketch, "E1416", {"start": v(106.68, 24.18) * mm, "end": v(107.43, 24.84) * mm});
            skLineSegment(sketch, "E1417", {"start": v(107.43, 24.84) * mm, "end": v(108.12, 25.59) * mm});
            skLineSegment(sketch, "E1418", {"start": v(108.12, 25.59) * mm, "end": v(108.75, 26.43) * mm});
            skLineSegment(sketch, "E1419", {"start": v(108.75, 26.43) * mm, "end": v(109.3, 27.35) * mm});
            skLineSegment(sketch, "E1420", {"start": v(109.3, 27.35) * mm, "end": v(109.77, 28.36) * mm});
            skLineSegment(sketch, "E1421", {"start": v(109.77, 28.36) * mm, "end": v(110.17, 29.45) * mm});
            skLineSegment(sketch, "E1422", {"start": v(110.17, 29.45) * mm, "end": v(110.5, 30.61) * mm});
            skLineSegment(sketch, "E1423", {"start": v(110.5, 30.61) * mm, "end": v(110.74, 31.84) * mm});
            skLineSegment(sketch, "E1424", {"start": v(110.74, 31.84) * mm, "end": v(110.9, 33.13) * mm});
            skLineSegment(sketch, "E1425", {"start": v(110.9, 33.13) * mm, "end": v(110.98, 34.48) * mm});
            skLineSegment(sketch, "E1426", {"start": v(110.98, 34.48) * mm, "end": v(110.98, 35.88) * mm});
            skLineSegment(sketch, "E1427", {"start": v(110.98, 35.88) * mm, "end": v(110.9, 37.32) * mm});
            skLineSegment(sketch, "E1428", {"start": v(110.9, 37.32) * mm, "end": v(110.74, 38.8) * mm});
            skLineSegment(sketch, "E1429", {"start": v(110.74, 38.8) * mm, "end": v(110.5, 40.3) * mm});
            skLineSegment(sketch, "E1430", {"start": v(110.5, 40.3) * mm, "end": v(110.17, 41.84) * mm});
            skLineSegment(sketch, "E1431", {"start": v(110.17, 41.84) * mm, "end": v(109.77, 43.39) * mm});
            skLineSegment(sketch, "E1432", {"start": v(109.77, 43.39) * mm, "end": v(109.3, 44.95) * mm});
            skLineSegment(sketch, "E1433", {"start": v(109.3, 44.95) * mm, "end": v(108.75, 46.51) * mm});
            skLineSegment(sketch, "E1434", {"start": v(108.75, 46.51) * mm, "end": v(108.12, 48.07) * mm});
            skLineSegment(sketch, "E1435", {"start": v(108.12, 48.07) * mm, "end": v(107.43, 49.62) * mm});
            skLineSegment(sketch, "E1436", {"start": v(107.43, 49.62) * mm, "end": v(106.68, 51.14) * mm});
            skLineSegment(sketch, "E1437", {"start": v(106.68, 51.14) * mm, "end": v(105.86, 52.65) * mm});
            skLineSegment(sketch, "E1438", {"start": v(105.86, 52.65) * mm, "end": v(104.99, 54.12) * mm});
            skArc(sketch, "E1439", {"start": v(89.67, 78.73) * mm, "mid": v(87.05, 82.14) * mm, "end": v(83.7, 84.82) * mm});
            skArc(sketch, "E1440", {"start": v(94.85, 65.51) * mm, "mid": v(95.15, 62.84) * mm, "end": v(97.32, 61.24) * mm});
            skLineSegment(sketch, "E1441", {"start": v(83.7, 84.82) * mm, "end": v(41.48, 109.18) * mm});
            skArc(sketch, "E1442", {"start": v(94.85, 25.28) * mm, "mid": v(95.15, 22.6) * mm, "end": v(97.32, 21) * mm});
            skArc(sketch, "E1443", {"start": v(40.07, 106.78) * mm, "mid": v(40.37, 104.1) * mm, "end": v(42.54, 102.5) * mm});
            skArc(sketch, "E1444", {"start": v(41.48, 109.18) * mm, "mid": v(38.4, 110.36) * mm, "end": v(35.14, 109.81) * mm});
            skArc(sketch, "E1445", {"start": v(40.07, 47.26) * mm, "mid": v(40.37, 44.58) * mm, "end": v(42.54, 42.98) * mm});
            skArc(sketch, "E1446", {"start": v(66.67, 98.6) * mm, "mid": v(67.07, 98.5) * mm, "end": v(67.4, 98.75) * mm});
            skLineSegment(sketch, "E1447", {"start": v(87.98, 86) * mm, "end": v(87.98, 86.87) * mm});
            skLineSegment(sketch, "E1448", {"start": v(98.04, 66.2) * mm, "end": v(97.16, 66.75) * mm});
            skLineSegment(sketch, "E1449", {"start": v(97.16, 66.75) * mm, "end": v(97.1, 66.8) * mm});
            skLineSegment(sketch, "E1450", {"start": v(99.66, 65.27) * mm, "end": v(98.04, 66.2) * mm});
            skLineSegment(sketch, "E1451", {"start": v(100.19, 61.83) * mm, "end": v(101.78, 62.75) * mm});
            skLineSegment(sketch, "E1452", {"start": v(78.38, 131.06) * mm, "end": v(78.38, 110.05) * mm});
            skArc(sketch, "E1453", {"start": v(81.19, 132.69) * mm, "mid": v(79.23, 132.83) * mm, "end": v(78.38, 131.06) * mm});
            skLineSegment(sketch, "E1454", {"start": v(85.34, 130.28) * mm, "end": v(81.19, 132.69) * mm});
            skArc(sketch, "E1455", {"start": v(87.25, 127.95) * mm, "mid": v(86.49, 129.27) * mm, "end": v(85.34, 130.28) * mm});
            skLineSegment(sketch, "E1456", {"start": v(94.06, 111.32) * mm, "end": v(87.25, 127.95) * mm});
            skLineSegment(sketch, "E1457", {"start": v(93.34, 110.25) * mm, "end": v(93.56, 110.15) * mm});
            skLineSegment(sketch, "E1458", {"start": v(93.56, 110.15) * mm, "end": v(93.77, 110.13) * mm});
            skLineSegment(sketch, "E1459", {"start": v(93.77, 110.13) * mm, "end": v(93.94, 110.2) * mm});
            skLineSegment(sketch, "E1460", {"start": v(93.94, 110.2) * mm, "end": v(94.08, 110.32) * mm});
            skLineSegment(sketch, "E1461", {"start": v(94.08, 110.32) * mm, "end": v(94.16, 110.51) * mm});
            skLineSegment(sketch, "E1462", {"start": v(94.16, 110.51) * mm, "end": v(94.18, 110.75) * mm});
            skLineSegment(sketch, "E1463", {"start": v(94.18, 110.75) * mm, "end": v(94.15, 111.03) * mm});
            skLineSegment(sketch, "E1464", {"start": v(94.15, 111.03) * mm, "end": v(94.06, 111.32) * mm});
            skLineSegment(sketch, "E1465", {"start": v(88.34, 113.13) * mm, "end": v(93.34, 110.25) * mm});
            skArc(sketch, "E1466", {"start": v(88.34, 113.13) * mm, "mid": v(86.96, 113.25) * mm, "end": v(86.37, 112) * mm});
            skLineSegment(sketch, "E1467", {"start": v(86.37, 106.17) * mm, "end": v(86.37, 112) * mm});
            skArc(sketch, "E1468", {"start": v(86.37, 106.17) * mm, "mid": v(86.4, 105.77) * mm, "end": v(86.48, 105.37) * mm});
            skLineSegment(sketch, "E1469", {"start": v(96.02, 61.87) * mm, "end": v(97.42, 62.68) * mm});
            skLineSegment(sketch, "E1470", {"start": v(99.07, 63.63) * mm, "end": v(99.66, 63.97) * mm});
            skLineSegment(sketch, "E1471", {"start": v(96.18, 112.54) * mm, "end": v(89.38, 129.18) * mm});
            skArc(sketch, "E1472", {"start": v(94.2, 73.13) * mm, "mid": v(96.87, 69.96) * mm, "end": v(100.16, 67.43) * mm});
            skLineSegment(sketch, "E1473", {"start": v(90.1, 84.77) * mm, "end": v(90.1, 84.85) * mm});
            skArc(sketch, "E1474", {"start": v(91.22, 92.49) * mm, "mid": v(88.91, 90.08) * mm, "end": v(87.98, 86.87) * mm});
            skLineSegment(sketch, "E1475", {"start": v(67.51, 99.31) * mm, "end": v(67.4, 98.75) * mm});
            skArc(sketch, "E1476", {"start": v(70.72, 104.33) * mm, "mid": v(68.57, 102.17) * mm, "end": v(67.51, 99.31) * mm});
            skArc(sketch, "E1477", {"start": v(91.22, 90.04) * mm, "mid": v(90.43, 89.2) * mm, "end": v(90.1, 88.1) * mm});
            skArc(sketch, "E1478", {"start": v(99.66, 63.97) * mm, "mid": v(100.1, 64.62) * mm, "end": v(99.66, 65.27) * mm});
            skLineSegment(sketch, "E1479", {"start": v(101.78, 62.75) * mm, "end": v(102.25, 63.06) * mm});
            skLineSegment(sketch, "E1480", {"start": v(102.25, 63.06) * mm, "end": v(102.62, 63.42) * mm});
            skLineSegment(sketch, "E1481", {"start": v(102.62, 63.42) * mm, "end": v(102.9, 63.8) * mm});
            skLineSegment(sketch, "E1482", {"start": v(102.9, 63.8) * mm, "end": v(103.07, 64.2) * mm});
            skLineSegment(sketch, "E1483", {"start": v(103.07, 64.2) * mm, "end": v(103.12, 64.62) * mm});
            skLineSegment(sketch, "E1484", {"start": v(103.12, 64.62) * mm, "end": v(103.07, 65.03) * mm});
            skLineSegment(sketch, "E1485", {"start": v(103.07, 65.03) * mm, "end": v(102.9, 65.44) * mm});
            skLineSegment(sketch, "E1486", {"start": v(102.9, 65.44) * mm, "end": v(102.62, 65.82) * mm});
            skLineSegment(sketch, "E1487", {"start": v(102.62, 65.82) * mm, "end": v(102.25, 66.17) * mm});
            skLineSegment(sketch, "E1488", {"start": v(102.25, 66.17) * mm, "end": v(101.78, 66.5) * mm});
            skArc(sketch, "E1489", {"start": v(89.38, 129.18) * mm, "mid": v(88.6, 130.5) * mm, "end": v(87.47, 131.5) * mm});
            skLineSegment(sketch, "E1490", {"start": v(87.47, 131.5) * mm, "end": v(83.3, 133.91) * mm});
            skLineSegment(sketch, "E1491", {"start": v(91.22, 92.49) * mm, "end": v(94.25, 94.24) * mm});
            skLineSegment(sketch, "E1492", {"start": v(77.26, 108.1) * mm, "end": v(70.72, 104.33) * mm});
            skArc(sketch, "E1493", {"start": v(94.25, 94.24) * mm, "mid": v(95.69, 95.36) * mm, "end": v(96.53, 96.98) * mm});
            skLineSegment(sketch, "E1494", {"start": v(90.1, 84.85) * mm, "end": v(90.1, 88.1) * mm});
            skLineSegment(sketch, "E1495", {"start": v(91.22, 90.04) * mm, "end": v(94.25, 91.79) * mm});
            skLineSegment(sketch, "E1496", {"start": v(101.78, 66.5) * mm, "end": v(100.16, 67.43) * mm});
            skLineSegment(sketch, "E1497", {"start": v(96.06, 111.41) * mm, "end": v(96.07, 111.42) * mm});
            skLineSegment(sketch, "E1498", {"start": v(96.07, 111.42) * mm, "end": v(96.2, 111.54) * mm});
            skLineSegment(sketch, "E1499", {"start": v(96.2, 111.54) * mm, "end": v(96.28, 111.74) * mm});
            skLineSegment(sketch, "E1500", {"start": v(96.28, 111.74) * mm, "end": v(96.3, 111.98) * mm});
            skLineSegment(sketch, "E1501", {"start": v(96.3, 111.98) * mm, "end": v(96.27, 112.25) * mm});
            skLineSegment(sketch, "E1502", {"start": v(96.27, 112.25) * mm, "end": v(96.18, 112.54) * mm});
            skLineSegment(sketch, "E1503", {"start": v(96.53, 94.53) * mm, "end": v(96.53, 96.98) * mm});
            skArc(sketch, "E1504", {"start": v(94.25, 91.79) * mm, "mid": v(95.69, 92.91) * mm, "end": v(96.53, 94.53) * mm});
            skArc(sketch, "E1505", {"start": v(83.3, 133.91) * mm, "mid": v(82.34, 134.28) * mm, "end": v(81.32, 134.1) * mm});
            skArc(sketch, "E1506", {"start": v(77.26, 108.1) * mm, "mid": v(78.06, 108.94) * mm, "end": v(78.38, 110.05) * mm});
            skArc(sketch, "E1507", {"start": v(86.48, 105.37) * mm, "mid": v(87.16, 104.28) * mm, "end": v(88.14, 103.44) * mm});
            skLineSegment(sketch, "E1508", {"start": v(93.07, 100.6) * mm, "end": v(88.14, 103.44) * mm});
            skArc(sketch, "E1509", {"start": v(96.53, 96.98) * mm, "mid": v(95.08, 99.05) * mm, "end": v(93.07, 100.6) * mm});
            skLineSegment(sketch, "E1510", {"start": v(94.81, 100.2) * mm, "end": v(93.07, 100.6) * mm});
            skArc(sketch, "E1511", {"start": v(96.53, 94.53) * mm, "mid": v(96.7, 97.67) * mm, "end": v(94.81, 100.2) * mm});
            skLineSegment(sketch, "E1512", {"start": v(89.88, 103.05) * mm, "end": v(88.14, 103.44) * mm});
            skLineSegment(sketch, "E1513", {"start": v(94.81, 100.2) * mm, "end": v(89.88, 103.05) * mm});
            skLineSegment(sketch, "E1514", {"start": v(88.5, 107.4) * mm, "end": v(88.5, 113.04) * mm});
            skLineSegment(sketch, "E1515", {"start": v(88.6, 106.6) * mm, "end": v(86.48, 105.37) * mm});
            skArc(sketch, "E1516", {"start": v(88.6, 106.6) * mm, "mid": v(88.94, 104.71) * mm, "end": v(89.88, 103.05) * mm});
            skArc(sketch, "E1517", {"start": v(88.5, 107.4) * mm, "mid": v(88.52, 107) * mm, "end": v(88.6, 106.6) * mm});
            skLineSegment(sketch, "E1518", {"start": v(66.67, 98.6) * mm, "end": v(67.46, 99.05) * mm});
            skArc(sketch, "E1519", {"start": v(66.65, 98.6) * mm, "mid": v(66.19, 98.78) * mm, "end": v(65.7, 98.86) * mm});
            skLineSegment(sketch, "E1520", {"start": v(66.67, 98.6) * mm, "end": v(66.65, 98.6) * mm});
            skArc(sketch, "E1521", {"start": v(67.72, 100.28) * mm, "mid": v(65.5, 100.6) * mm, "end": v(63.29, 100.25) * mm});
            skArc(sketch, "E1522", {"start": v(89.3, 47.25) * mm, "mid": v(88.67, 46.7) * mm, "end": v(88.22, 46) * mm});
            skArc(sketch, "E1523", {"start": v(95.6, 33.2) * mm, "mid": v(96.44, 33.24) * mm, "end": v(97.23, 33.5) * mm});
            skLineSegment(sketch, "E1524", {"start": v(105.16, 56.16) * mm, "end": v(104.1, 55.54) * mm});
            skLineSegment(sketch, "E1525", {"start": v(109.32, 53.76) * mm, "end": v(105.16, 56.16) * mm});
            skLineSegment(sketch, "E1526", {"start": v(106.79, 52.3) * mm, "end": v(109.32, 53.76) * mm});
            skArc(sketch, "E1527", {"start": v(106.95, 52.14) * mm, "mid": v(106.87, 52.22) * mm, "end": v(106.79, 52.3) * mm});
            skArc(sketch, "E1528", {"start": v(107.94, 51.1) * mm, "mid": v(107.46, 51.64) * mm, "end": v(106.95, 52.14) * mm});
            skArc(sketch, "E1529", {"start": v(106.41, 51.63) * mm, "mid": v(107.17, 51.36) * mm, "end": v(107.94, 51.1) * mm});
            skLineSegment(sketch, "E1530", {"start": v(106.57, 51.35) * mm, "end": v(106.8, 51.12) * mm});
            skLineSegment(sketch, "E1531", {"start": v(106.8, 51.12) * mm, "end": v(107.2, 50.68) * mm});
            skLineSegment(sketch, "E1532", {"start": v(107.2, 50.68) * mm, "end": v(106.84, 50.8) * mm});
            skArc(sketch, "E1533", {"start": v(110.1, 42.08) * mm, "mid": v(109.35, 46.62) * mm, "end": v(107.2, 50.68) * mm});
            skLineSegment(sketch, "E1534", {"start": v(110.44, 40.44) * mm, "end": v(110.72, 41.28) * mm});
            skLineSegment(sketch, "E1535", {"start": v(110.72, 41.28) * mm, "end": v(110.88, 42.77) * mm});
            skLineSegment(sketch, "E1536", {"start": v(110.88, 42.77) * mm, "end": v(110.77, 44.4) * mm});
            skLineSegment(sketch, "E1537", {"start": v(110.77, 44.4) * mm, "end": v(110.4, 46.1) * mm});
            skLineSegment(sketch, "E1538", {"start": v(110.4, 46.1) * mm, "end": v(109.82, 47.76) * mm});
            skLineSegment(sketch, "E1539", {"start": v(109.82, 47.76) * mm, "end": v(109.02, 49.42) * mm});
            skLineSegment(sketch, "E1540", {"start": v(109.02, 49.42) * mm, "end": v(108.5, 50.28) * mm});
            skLineSegment(sketch, "E1541", {"start": v(108.5, 50.28) * mm, "end": v(107.94, 51.1) * mm});
            skLineSegment(sketch, "E1542", {"start": v(111.5, 41.09) * mm, "end": v(111.63, 41.17) * mm});
            skLineSegment(sketch, "E1543", {"start": v(111.63, 41.17) * mm, "end": v(112.07, 41.53) * mm});
            skLineSegment(sketch, "E1544", {"start": v(112.07, 41.53) * mm, "end": v(112.46, 41.98) * mm});
            skLineSegment(sketch, "E1545", {"start": v(112.46, 41.98) * mm, "end": v(112.77, 42.52) * mm});
            skLineSegment(sketch, "E1546", {"start": v(112.77, 42.52) * mm, "end": v(113, 43.14) * mm});
            skLineSegment(sketch, "E1547", {"start": v(113, 43.14) * mm, "end": v(113.16, 43.83) * mm});
            skLineSegment(sketch, "E1548", {"start": v(113.16, 43.83) * mm, "end": v(113.24, 44.58) * mm});
            skLineSegment(sketch, "E1549", {"start": v(113.24, 44.58) * mm, "end": v(113.24, 45.39) * mm});
            skLineSegment(sketch, "E1550", {"start": v(113.24, 45.39) * mm, "end": v(113.16, 46.23) * mm});
            skLineSegment(sketch, "E1551", {"start": v(113.16, 46.23) * mm, "end": v(113, 47.1) * mm});
            skLineSegment(sketch, "E1552", {"start": v(113, 47.1) * mm, "end": v(112.77, 48) * mm});
            skLineSegment(sketch, "E1553", {"start": v(112.77, 48) * mm, "end": v(112.46, 48.9) * mm});
            skLineSegment(sketch, "E1554", {"start": v(112.46, 48.9) * mm, "end": v(112.07, 49.8) * mm});
            skLineSegment(sketch, "E1555", {"start": v(112.07, 49.8) * mm, "end": v(111.63, 50.67) * mm});
            skLineSegment(sketch, "E1556", {"start": v(111.63, 50.67) * mm, "end": v(111.12, 51.51) * mm});
            skLineSegment(sketch, "E1557", {"start": v(111.12, 51.51) * mm, "end": v(110.56, 52.32) * mm});
            skLineSegment(sketch, "E1558", {"start": v(110.56, 52.32) * mm, "end": v(109.96, 53.07) * mm});
            skLineSegment(sketch, "E1559", {"start": v(109.96, 53.07) * mm, "end": v(109.32, 53.76) * mm});
            skArc(sketch, "E1560", {"start": v(105.16, 56.16) * mm, "mid": v(104.45, 56.2) * mm, "end": v(103.75, 56.11) * mm});
            skArc(sketch, "E1561", {"start": v(112.61, 48.47) * mm, "mid": v(111.65, 50.83) * mm, "end": v(110.13, 52.87) * mm});
            skArc(sketch, "E1562", {"start": v(110.71, 40.64) * mm, "mid": v(111.93, 41.17) * mm, "end": v(112.65, 42.3) * mm});
            skLineSegment(sketch, "E1563", {"start": v(109.26, 54.53) * mm, "end": v(108.62, 54.17) * mm});
            skArc(sketch, "E1564", {"start": v(113.56, 47.38) * mm, "mid": v(112.25, 51.46) * mm, "end": v(109.26, 54.53) * mm});
            skLineSegment(sketch, "E1565", {"start": v(113.56, 47.38) * mm, "end": v(113.01, 47.07) * mm});
            skLineSegment(sketch, "E1566", {"start": v(113.56, 43.85) * mm, "end": v(113.12, 43.6) * mm});
            skLineSegment(sketch, "E1567", {"start": v(113.56, 43.85) * mm, "end": v(113.56, 47.38) * mm});
            skArc(sketch, "E1568", {"start": v(112.3, 41.32) * mm, "mid": v(113.26, 42.42) * mm, "end": v(113.56, 43.85) * mm});
            skLineSegment(sketch, "E1569", {"start": v(113.56, 49.29) * mm, "end": v(113.18, 50.2) * mm});
            skLineSegment(sketch, "E1570", {"start": v(113.18, 50.2) * mm, "end": v(112.73, 51.11) * mm});
            skLineSegment(sketch, "E1571", {"start": v(112.73, 51.11) * mm, "end": v(112.22, 51.99) * mm});
            skLineSegment(sketch, "E1572", {"start": v(112.22, 51.99) * mm, "end": v(111.65, 52.82) * mm});
            skLineSegment(sketch, "E1573", {"start": v(111.65, 52.82) * mm, "end": v(111.04, 53.6) * mm});
            skLineSegment(sketch, "E1574", {"start": v(111.04, 53.6) * mm, "end": v(110.4, 54.34) * mm});
            skLineSegment(sketch, "E1575", {"start": v(110.4, 54.34) * mm, "end": v(109.72, 55) * mm});
            skLineSegment(sketch, "E1576", {"start": v(109.72, 55) * mm, "end": v(109.02, 55.59) * mm});
            skLineSegment(sketch, "E1577", {"start": v(109.02, 55.59) * mm, "end": v(108.3, 56.09) * mm});
            skLineSegment(sketch, "E1578", {"start": v(108.3, 56.09) * mm, "end": v(107.6, 56.5) * mm});
            skLineSegment(sketch, "E1579", {"start": v(107.6, 56.5) * mm, "end": v(106.88, 56.82) * mm});
            skLineSegment(sketch, "E1580", {"start": v(106.88, 56.82) * mm, "end": v(106.18, 57.04) * mm});
            skLineSegment(sketch, "E1581", {"start": v(106.18, 57.04) * mm, "end": v(105.5, 57.16) * mm});
            skLineSegment(sketch, "E1582", {"start": v(105.5, 57.16) * mm, "end": v(104.86, 57.18) * mm});
            skLineSegment(sketch, "E1583", {"start": v(104.86, 57.18) * mm, "end": v(104.25, 57.1) * mm});
            skLineSegment(sketch, "E1584", {"start": v(104.25, 57.1) * mm, "end": v(103.69, 56.9) * mm});
            skLineSegment(sketch, "E1585", {"start": v(103.69, 56.9) * mm, "end": v(103.36, 56.74) * mm});
            skLineSegment(sketch, "E1586", {"start": v(113.56, 36.43) * mm, "end": v(113.56, 49.29) * mm});
            skArc(sketch, "E1587", {"start": v(111, 35.02) * mm, "mid": v(112.45, 35.41) * mm, "end": v(113.56, 36.43) * mm});
            skLineSegment(sketch, "E1588", {"start": v(114.98, 50.1) * mm, "end": v(114.6, 51.03) * mm});
            skLineSegment(sketch, "E1589", {"start": v(114.6, 51.03) * mm, "end": v(114.14, 51.93) * mm});
            skLineSegment(sketch, "E1590", {"start": v(114.14, 51.93) * mm, "end": v(113.63, 52.8) * mm});
            skLineSegment(sketch, "E1591", {"start": v(113.63, 52.8) * mm, "end": v(113.07, 53.64) * mm});
            skLineSegment(sketch, "E1592", {"start": v(113.07, 53.64) * mm, "end": v(112.46, 54.43) * mm});
            skLineSegment(sketch, "E1593", {"start": v(112.46, 54.43) * mm, "end": v(111.81, 55.15) * mm});
            skLineSegment(sketch, "E1594", {"start": v(111.81, 55.15) * mm, "end": v(111.13, 55.82) * mm});
            skLineSegment(sketch, "E1595", {"start": v(111.13, 55.82) * mm, "end": v(110.44, 56.4) * mm});
            skLineSegment(sketch, "E1596", {"start": v(110.44, 56.4) * mm, "end": v(109.72, 56.9) * mm});
            skLineSegment(sketch, "E1597", {"start": v(109.72, 56.9) * mm, "end": v(109, 57.32) * mm});
            skLineSegment(sketch, "E1598", {"start": v(109, 57.32) * mm, "end": v(108.3, 57.64) * mm});
            skLineSegment(sketch, "E1599", {"start": v(108.3, 57.64) * mm, "end": v(107.6, 57.86) * mm});
            skLineSegment(sketch, "E1600", {"start": v(107.6, 57.86) * mm, "end": v(106.92, 57.98) * mm});
            skLineSegment(sketch, "E1601", {"start": v(106.92, 57.98) * mm, "end": v(106.27, 58) * mm});
            skLineSegment(sketch, "E1602", {"start": v(106.27, 58) * mm, "end": v(105.67, 57.91) * mm});
            skLineSegment(sketch, "E1603", {"start": v(105.67, 57.91) * mm, "end": v(105.1, 57.73) * mm});
            skLineSegment(sketch, "E1604", {"start": v(105.1, 57.73) * mm, "end": v(104.8, 57.57) * mm});
            skLineSegment(sketch, "E1605", {"start": v(114.98, 50.1) * mm, "end": v(113.56, 49.29) * mm});
            skLineSegment(sketch, "E1606", {"start": v(114.98, 37.25) * mm, "end": v(113.56, 36.43) * mm});
            skLineSegment(sketch, "E1607", {"start": v(114.98, 37.25) * mm, "end": v(114.98, 50.1) * mm});
            skArc(sketch, "E1608", {"start": v(113.93, 36.26) * mm, "mid": v(114.5, 36.7) * mm, "end": v(114.98, 37.25) * mm});
            skArc(sketch, "E1609", {"start": v(94, 37.74) * mm, "mid": v(94.54, 39.26) * mm, "end": v(94.54, 40.86) * mm});
            skLineSegment(sketch, "E1610", {"start": v(92.23, 43.53) * mm, "end": v(92.23, 37.94) * mm});
            skArc(sketch, "E1611", {"start": v(93.94, 41.77) * mm, "mid": v(93.36, 39.74) * mm, "end": v(94, 37.74) * mm});
            skArc(sketch, "E1612", {"start": v(79.33, 71.76) * mm, "mid": v(80.9, 71.24) * mm, "end": v(82.53, 71.5) * mm});
            skArc(sketch, "E1613", {"start": v(79.33, 48.6) * mm, "mid": v(80.93, 48.22) * mm, "end": v(82.53, 48.6) * mm});
            skLineSegment(sketch, "E1614", {"start": v(80.66, 72.53) * mm, "end": v(79.33, 71.76) * mm});
            skArc(sketch, "E1615", {"start": v(80.66, 72.53) * mm, "mid": v(80.9, 72.35) * mm, "end": v(81.2, 72.27) * mm});
            skLineSegment(sketch, "E1616", {"start": v(82.53, 71.5) * mm, "end": v(81.2, 72.27) * mm});
            skArc(sketch, "E1617", {"start": v(80.7, 74.67) * mm, "mid": v(79.66, 73.38) * mm, "end": v(79.33, 71.76) * mm});
            skLineSegment(sketch, "E1618", {"start": v(80.7, 74.67) * mm, "end": v(80.7, 73.13) * mm});
            skArc(sketch, "E1619", {"start": v(80.7, 73.13) * mm, "mid": v(80.62, 72.84) * mm, "end": v(80.66, 72.53) * mm});
            skArc(sketch, "E1620", {"start": v(44.93, 95.32) * mm, "mid": v(43.7, 94.22) * mm, "end": v(43.1, 92.68) * mm});
            skLineSegment(sketch, "E1621", {"start": v(43.1, 69.53) * mm, "end": v(47.08, 67.23) * mm});
            skLineSegment(sketch, "E1622", {"start": v(75.35, 50.9) * mm, "end": v(79.33, 48.6) * mm});
            skArc(sketch, "E1623", {"start": v(75.35, 50.9) * mm, "mid": v(73.78, 51.6) * mm, "end": v(72.07, 51.81) * mm});
            skArc(sketch, "E1624", {"start": v(50.36, 64.35) * mm, "mid": v(48.85, 65.94) * mm, "end": v(47.08, 67.23) * mm});
            skLineSegment(sketch, "E1625", {"start": v(83.27, 49.04) * mm, "end": v(82.53, 48.6) * mm});
            skLineSegment(sketch, "E1626", {"start": v(83.16, 71.86) * mm, "end": v(82.53, 71.5) * mm});
            skLineSegment(sketch, "E1627", {"start": v(81.2, 72.27) * mm, "end": v(82.8, 73.2) * mm});
            skLineSegment(sketch, "E1628", {"start": v(44.93, 95.32) * mm, "end": v(47.46, 96.78) * mm});
            skLineSegment(sketch, "E1629", {"start": v(80.7, 74.67) * mm, "end": v(81.83, 75.32) * mm});
            skLineSegment(sketch, "E1630", {"start": v(80.7, 73.13) * mm, "end": v(82.43, 74.13) * mm});
            skLineSegment(sketch, "E1631", {"start": v(70.44, 51.56) * mm, "end": v(71.34, 51.76) * mm});
            skLineSegment(sketch, "E1632", {"start": v(71.34, 51.76) * mm, "end": v(72.07, 51.81) * mm});
            skLineSegment(sketch, "E1633", {"start": v(69.52, 51.24) * mm, "end": v(70.44, 51.56) * mm});
            skLineSegment(sketch, "E1634", {"start": v(51.7, 62.38) * mm, "end": v(52.16, 61.25) * mm});
            skLineSegment(sketch, "E1635", {"start": v(50.36, 64.35) * mm, "end": v(51.15, 63.32) * mm});
            skLineSegment(sketch, "E1636", {"start": v(51.15, 63.32) * mm, "end": v(51.7, 62.38) * mm});
            skLineSegment(sketch, "E1637", {"start": v(71.62, 51.78) * mm, "end": v(70.44, 51.56) * mm});
            skLineSegment(sketch, "E1638", {"start": v(68.47, 50.74) * mm, "end": v(69.52, 51.24) * mm});
            skArc(sketch, "E1639", {"start": v(62.72, 50.94) * mm, "mid": v(65.57, 50.12) * mm, "end": v(68.47, 50.74) * mm});
            skLineSegment(sketch, "E1640", {"start": v(56.29, 54.66) * mm, "end": v(62.72, 50.94) * mm});
            skArc(sketch, "E1641", {"start": v(52.51, 59.95) * mm, "mid": v(53.88, 56.93) * mm, "end": v(56.29, 54.66) * mm});
            skLineSegment(sketch, "E1642", {"start": v(52.16, 61.25) * mm, "end": v(52.51, 59.95) * mm});
            skLineSegment(sketch, "E1643", {"start": v(69.52, 51.24) * mm, "end": v(70.67, 51.13) * mm});
            skLineSegment(sketch, "E1644", {"start": v(70.67, 51.13) * mm, "end": v(71.7, 51.8) * mm});
            skLineSegment(sketch, "E1645", {"start": v(69.62, 50.63) * mm, "end": v(70.67, 51.13) * mm});
            skArc(sketch, "E1646", {"start": v(66.39, 50.03) * mm, "mid": v(68.04, 50.12) * mm, "end": v(69.62, 50.63) * mm});
            skArc(sketch, "E1647", {"start": v(42.43, 70.45) * mm, "mid": v(42.64, 69.9) * mm, "end": v(43.1, 69.53) * mm});
            skLineSegment(sketch, "E1648", {"start": v(43.1, 94.26) * mm, "end": v(42.6, 93.9) * mm});
            skLineSegment(sketch, "E1649", {"start": v(42.6, 93.9) * mm, "end": v(42.43, 93.47) * mm});
            skLineSegment(sketch, "E1650", {"start": v(42.43, 93.47) * mm, "end": v(42.6, 93.04) * mm});
            skLineSegment(sketch, "E1651", {"start": v(42.6, 93.04) * mm, "end": v(43.1, 92.68) * mm});
            skLineSegment(sketch, "E1652", {"start": v(43.1, 94.26) * mm, "end": v(43.57, 93.99) * mm});
            skLineSegment(sketch, "E1653", {"start": v(43.1, 94.26) * mm, "end": v(44.92, 95.32) * mm});
            skLineSegment(sketch, "E1654", {"start": v(93.17, 46.8) * mm, "end": v(92.5, 47.14) * mm});
            skLineSegment(sketch, "E1655", {"start": v(92.5, 47.14) * mm, "end": v(91.85, 47.38) * mm});
            skLineSegment(sketch, "E1656", {"start": v(91.85, 47.38) * mm, "end": v(91.21, 47.52) * mm});
            skLineSegment(sketch, "E1657", {"start": v(91.21, 47.52) * mm, "end": v(90.6, 47.57) * mm});
            skLineSegment(sketch, "E1658", {"start": v(90.6, 47.57) * mm, "end": v(90.03, 47.5) * mm});
            skLineSegment(sketch, "E1659", {"start": v(90.03, 47.5) * mm, "end": v(89.5, 47.34) * mm});
            skLineSegment(sketch, "E1660", {"start": v(89.5, 47.34) * mm, "end": v(89.02, 47.09) * mm});
            skLineSegment(sketch, "E1661", {"start": v(89.02, 47.09) * mm, "end": v(88.6, 46.73) * mm});
            skLineSegment(sketch, "E1662", {"start": v(88.6, 46.73) * mm, "end": v(88.25, 46.29) * mm});
            skLineSegment(sketch, "E1663", {"start": v(88.25, 46.29) * mm, "end": v(87.96, 45.76) * mm});
            skLineSegment(sketch, "E1664", {"start": v(87.96, 45.76) * mm, "end": v(87.75, 45.15) * mm});
            skLineSegment(sketch, "E1665", {"start": v(87.75, 45.15) * mm, "end": v(87.61, 44.48) * mm});
            skLineSegment(sketch, "E1666", {"start": v(87.61, 44.48) * mm, "end": v(87.6, 44.4) * mm});
            skLineSegment(sketch, "E1667", {"start": v(93.65, 33.58) * mm, "end": v(94.16, 33.37) * mm});
            skLineSegment(sketch, "E1668", {"start": v(94.16, 33.37) * mm, "end": v(94.8, 33.17) * mm});
            skLineSegment(sketch, "E1669", {"start": v(94.8, 33.17) * mm, "end": v(95.43, 33.08) * mm});
            skLineSegment(sketch, "E1670", {"start": v(95.43, 33.08) * mm, "end": v(96.02, 33.1) * mm});
            skLineSegment(sketch, "E1671", {"start": v(96.02, 33.1) * mm, "end": v(96.57, 33.2) * mm});
            skLineSegment(sketch, "E1672", {"start": v(96.57, 33.2) * mm, "end": v(97.08, 33.41) * mm});
            skLineSegment(sketch, "E1673", {"start": v(97.08, 33.41) * mm, "end": v(97.52, 33.72) * mm});
            skLineSegment(sketch, "E1674", {"start": v(97.52, 33.72) * mm, "end": v(97.91, 34.12) * mm});
            skLineSegment(sketch, "E1675", {"start": v(97.91, 34.12) * mm, "end": v(98.23, 34.6) * mm});
            skLineSegment(sketch, "E1676", {"start": v(98.23, 34.6) * mm, "end": v(98.48, 35.17) * mm});
            skLineSegment(sketch, "E1677", {"start": v(98.48, 35.17) * mm, "end": v(98.66, 35.81) * mm});
            skLineSegment(sketch, "E1678", {"start": v(98.66, 35.81) * mm, "end": v(98.76, 36.52) * mm});
            skLineSegment(sketch, "E1679", {"start": v(98.76, 36.52) * mm, "end": v(98.78, 37.27) * mm});
            skLineSegment(sketch, "E1680", {"start": v(98.78, 37.27) * mm, "end": v(98.72, 38.07) * mm});
            skLineSegment(sketch, "E1681", {"start": v(98.72, 38.07) * mm, "end": v(98.58, 38.9) * mm});
            skLineSegment(sketch, "E1682", {"start": v(98.58, 38.9) * mm, "end": v(98.37, 39.75) * mm});
            skLineSegment(sketch, "E1683", {"start": v(98.37, 39.75) * mm, "end": v(98.08, 40.61) * mm});
            skLineSegment(sketch, "E1684", {"start": v(98.08, 40.61) * mm, "end": v(97.73, 41.47) * mm});
            skLineSegment(sketch, "E1685", {"start": v(97.73, 41.47) * mm, "end": v(97.3, 42.3) * mm});
            skLineSegment(sketch, "E1686", {"start": v(97.3, 42.3) * mm, "end": v(96.83, 43.11) * mm});
            skLineSegment(sketch, "E1687", {"start": v(96.83, 43.11) * mm, "end": v(96.3, 43.89) * mm});
            skLineSegment(sketch, "E1688", {"start": v(96.3, 43.89) * mm, "end": v(95.73, 44.6) * mm});
            skLineSegment(sketch, "E1689", {"start": v(95.73, 44.6) * mm, "end": v(95.12, 45.27) * mm});
            skLineSegment(sketch, "E1690", {"start": v(95.12, 45.27) * mm, "end": v(94.48, 45.86) * mm});
            skLineSegment(sketch, "E1691", {"start": v(94.48, 45.86) * mm, "end": v(93.83, 46.37) * mm});
            skLineSegment(sketch, "E1692", {"start": v(93.83, 46.37) * mm, "end": v(93.17, 46.8) * mm});
            skArc(sketch, "E1693", {"start": v(98.06, 34.67) * mm, "mid": v(98.5, 35.86) * mm, "end": v(98.61, 37.12) * mm});
            skLineSegment(sketch, "E1694", {"start": v(90.73, 47.39) * mm, "end": v(90.75, 47.38) * mm});
            skLineSegment(sketch, "E1695", {"start": v(90.75, 47.38) * mm, "end": v(91.35, 47.32) * mm});
            skLineSegment(sketch, "E1696", {"start": v(91.35, 47.32) * mm, "end": v(91.98, 47.15) * mm});
            skLineSegment(sketch, "E1697", {"start": v(91.98, 47.15) * mm, "end": v(92.63, 46.9) * mm});
            skLineSegment(sketch, "E1698", {"start": v(92.63, 46.9) * mm, "end": v(93.28, 46.54) * mm});
            skLineSegment(sketch, "E1699", {"start": v(93.28, 46.54) * mm, "end": v(93.93, 46.1) * mm});
            skLineSegment(sketch, "E1700", {"start": v(93.93, 46.1) * mm, "end": v(94.56, 45.58) * mm});
            skLineSegment(sketch, "E1701", {"start": v(94.56, 45.58) * mm, "end": v(95.18, 44.98) * mm});
            skLineSegment(sketch, "E1702", {"start": v(95.18, 44.98) * mm, "end": v(95.77, 44.32) * mm});
            skLineSegment(sketch, "E1703", {"start": v(95.77, 44.32) * mm, "end": v(96.32, 43.6) * mm});
            skLineSegment(sketch, "E1704", {"start": v(96.32, 43.6) * mm, "end": v(96.82, 42.83) * mm});
            skLineSegment(sketch, "E1705", {"start": v(96.82, 42.83) * mm, "end": v(97.28, 42.03) * mm});
            skLineSegment(sketch, "E1706", {"start": v(97.28, 42.03) * mm, "end": v(97.67, 41.2) * mm});
            skLineSegment(sketch, "E1707", {"start": v(97.67, 41.2) * mm, "end": v(98, 40.37) * mm});
            skLineSegment(sketch, "E1708", {"start": v(98, 40.37) * mm, "end": v(98.27, 39.53) * mm});
            skLineSegment(sketch, "E1709", {"start": v(98.27, 39.53) * mm, "end": v(98.46, 38.7) * mm});
            skLineSegment(sketch, "E1710", {"start": v(98.46, 38.7) * mm, "end": v(98.57, 37.9) * mm});
            skLineSegment(sketch, "E1711", {"start": v(98.57, 37.9) * mm, "end": v(98.61, 37.12) * mm});
            skLineSegment(sketch, "E1712", {"start": v(98.25, 37.12) * mm, "end": v(98.21, 37.88) * mm});
            skLineSegment(sketch, "E1713", {"start": v(98.21, 37.88) * mm, "end": v(98.1, 38.68) * mm});
            skLineSegment(sketch, "E1714", {"start": v(98.1, 38.68) * mm, "end": v(97.9, 39.5) * mm});
            skLineSegment(sketch, "E1715", {"start": v(97.9, 39.5) * mm, "end": v(97.64, 40.32) * mm});
            skLineSegment(sketch, "E1716", {"start": v(97.64, 40.32) * mm, "end": v(97.31, 41.15) * mm});
            skLineSegment(sketch, "E1717", {"start": v(97.31, 41.15) * mm, "end": v(96.91, 41.96) * mm});
            skLineSegment(sketch, "E1718", {"start": v(96.91, 41.96) * mm, "end": v(96.46, 42.75) * mm});
            skLineSegment(sketch, "E1719", {"start": v(96.46, 42.75) * mm, "end": v(95.96, 43.5) * mm});
            skLineSegment(sketch, "E1720", {"start": v(95.96, 43.5) * mm, "end": v(95.4, 44.2) * mm});
            skLineSegment(sketch, "E1721", {"start": v(95.4, 44.2) * mm, "end": v(94.82, 44.84) * mm});
            skLineSegment(sketch, "E1722", {"start": v(94.82, 44.84) * mm, "end": v(94.2, 45.41) * mm});
            skLineSegment(sketch, "E1723", {"start": v(94.2, 45.41) * mm, "end": v(93.58, 45.91) * mm});
            skLineSegment(sketch, "E1724", {"start": v(93.58, 45.91) * mm, "end": v(92.94, 46.33) * mm});
            skLineSegment(sketch, "E1725", {"start": v(92.94, 46.33) * mm, "end": v(92.3, 46.65) * mm});
            skLineSegment(sketch, "E1726", {"start": v(92.3, 46.65) * mm, "end": v(91.66, 46.88) * mm});
            skLineSegment(sketch, "E1727", {"start": v(91.66, 46.88) * mm, "end": v(91.05, 47.02) * mm});
            skLineSegment(sketch, "E1728", {"start": v(91.05, 47.02) * mm, "end": v(90.46, 47.05) * mm});
            skLineSegment(sketch, "E1729", {"start": v(90.46, 47.05) * mm, "end": v(89.92, 46.98) * mm});
            skLineSegment(sketch, "E1730", {"start": v(89.92, 46.98) * mm, "end": v(89.4, 46.82) * mm});
            skLineSegment(sketch, "E1731", {"start": v(89.4, 46.82) * mm, "end": v(88.96, 46.55) * mm});
            skLineSegment(sketch, "E1732", {"start": v(88.96, 46.55) * mm, "end": v(88.56, 46.2) * mm});
            skLineSegment(sketch, "E1733", {"start": v(88.56, 46.2) * mm, "end": v(88.23, 45.76) * mm});
            skLineSegment(sketch, "E1734", {"start": v(88.23, 45.76) * mm, "end": v(87.96, 45.23) * mm});
            skLineSegment(sketch, "E1735", {"start": v(87.96, 45.23) * mm, "end": v(87.77, 44.64) * mm});
            skLineSegment(sketch, "E1736", {"start": v(87.77, 44.64) * mm, "end": v(87.66, 43.97) * mm});
            skLineSegment(sketch, "E1737", {"start": v(87.66, 43.97) * mm, "end": v(87.62, 43.26) * mm});
            skLineSegment(sketch, "E1738", {"start": v(87.62, 43.26) * mm, "end": v(87.66, 42.5) * mm});
            skLineSegment(sketch, "E1739", {"start": v(87.66, 42.5) * mm, "end": v(87.77, 41.7) * mm});
            skLineSegment(sketch, "E1740", {"start": v(87.77, 41.7) * mm, "end": v(87.96, 40.88) * mm});
            skLineSegment(sketch, "E1741", {"start": v(87.96, 40.88) * mm, "end": v(88.23, 40.05) * mm});
            skLineSegment(sketch, "E1742", {"start": v(88.23, 40.05) * mm, "end": v(88.56, 39.23) * mm});
            skLineSegment(sketch, "E1743", {"start": v(88.56, 39.23) * mm, "end": v(88.96, 38.41) * mm});
            skLineSegment(sketch, "E1744", {"start": v(88.96, 38.41) * mm, "end": v(89.4, 37.63) * mm});
            skLineSegment(sketch, "E1745", {"start": v(89.4, 37.63) * mm, "end": v(89.92, 36.88) * mm});
            skLineSegment(sketch, "E1746", {"start": v(89.92, 36.88) * mm, "end": v(90.46, 36.18) * mm});
            skLineSegment(sketch, "E1747", {"start": v(90.46, 36.18) * mm, "end": v(91.05, 35.53) * mm});
            skLineSegment(sketch, "E1748", {"start": v(91.05, 35.53) * mm, "end": v(91.66, 34.96) * mm});
            skLineSegment(sketch, "E1749", {"start": v(91.66, 34.96) * mm, "end": v(92.3, 34.46) * mm});
            skLineSegment(sketch, "E1750", {"start": v(92.3, 34.46) * mm, "end": v(92.94, 34.05) * mm});
            skLineSegment(sketch, "E1751", {"start": v(92.94, 34.05) * mm, "end": v(93.58, 33.72) * mm});
            skLineSegment(sketch, "E1752", {"start": v(93.58, 33.72) * mm, "end": v(94.2, 33.5) * mm});
            skLineSegment(sketch, "E1753", {"start": v(94.2, 33.5) * mm, "end": v(94.82, 33.36) * mm});
            skLineSegment(sketch, "E1754", {"start": v(94.82, 33.36) * mm, "end": v(95.4, 33.32) * mm});
            skLineSegment(sketch, "E1755", {"start": v(95.4, 33.32) * mm, "end": v(95.96, 33.4) * mm});
            skLineSegment(sketch, "E1756", {"start": v(95.96, 33.4) * mm, "end": v(96.46, 33.56) * mm});
            skLineSegment(sketch, "E1757", {"start": v(96.46, 33.56) * mm, "end": v(96.91, 33.82) * mm});
            skLineSegment(sketch, "E1758", {"start": v(96.91, 33.82) * mm, "end": v(97.31, 34.17) * mm});
            skLineSegment(sketch, "E1759", {"start": v(97.31, 34.17) * mm, "end": v(97.64, 34.62) * mm});
            skLineSegment(sketch, "E1760", {"start": v(97.64, 34.62) * mm, "end": v(97.9, 35.14) * mm});
            skLineSegment(sketch, "E1761", {"start": v(97.9, 35.14) * mm, "end": v(98.1, 35.74) * mm});
            skLineSegment(sketch, "E1762", {"start": v(98.1, 35.74) * mm, "end": v(98.21, 36.4) * mm});
            skLineSegment(sketch, "E1763", {"start": v(98.21, 36.4) * mm, "end": v(98.25, 37.12) * mm});
            skArc(sketch, "E1764", {"start": v(36.8, 57.57) * mm, "mid": v(38.88, 50.47) * mm, "end": v(44, 45.13) * mm});
            skLineSegment(sketch, "E1765", {"start": v(44, 45.13) * mm, "end": v(77.58, 25.74) * mm});
            skLineSegment(sketch, "E1766", {"start": v(77.58, 25.74) * mm, "end": v(78.33, 25.35) * mm});
            skLineSegment(sketch, "E1767", {"start": v(78.33, 25.35) * mm, "end": v(79.07, 25.06) * mm});
            skLineSegment(sketch, "E1768", {"start": v(79.07, 25.06) * mm, "end": v(79.8, 24.86) * mm});
            skLineSegment(sketch, "E1769", {"start": v(79.8, 24.86) * mm, "end": v(80.5, 24.77) * mm});
            skLineSegment(sketch, "E1770", {"start": v(80.5, 24.77) * mm, "end": v(81.17, 24.78) * mm});
            skLineSegment(sketch, "E1771", {"start": v(81.17, 24.78) * mm, "end": v(81.8, 24.88) * mm});
            skLineSegment(sketch, "E1772", {"start": v(81.8, 24.88) * mm, "end": v(82.38, 25.1) * mm});
            skLineSegment(sketch, "E1773", {"start": v(82.38, 25.1) * mm, "end": v(82.92, 25.4) * mm});
            skLineSegment(sketch, "E1774", {"start": v(82.92, 25.4) * mm, "end": v(83.39, 25.8) * mm});
            skLineSegment(sketch, "E1775", {"start": v(83.39, 25.8) * mm, "end": v(83.8, 26.3) * mm});
            skLineSegment(sketch, "E1776", {"start": v(83.8, 26.3) * mm, "end": v(84.14, 26.87) * mm});
            skLineSegment(sketch, "E1777", {"start": v(84.14, 26.87) * mm, "end": v(84.4, 27.53) * mm});
            skLineSegment(sketch, "E1778", {"start": v(84.4, 27.53) * mm, "end": v(84.6, 28.25) * mm});
            skLineSegment(sketch, "E1779", {"start": v(84.6, 28.25) * mm, "end": v(84.72, 29.04) * mm});
            skLineSegment(sketch, "E1780", {"start": v(84.72, 29.04) * mm, "end": v(84.76, 29.89) * mm});
            skLineSegment(sketch, "E1781", {"start": v(84.76, 29.89) * mm, "end": v(84.76, 68.67) * mm});
            skArc(sketch, "E1782", {"start": v(84.76, 68.67) * mm, "mid": v(82.69, 75.77) * mm, "end": v(77.58, 81.11) * mm});
            skLineSegment(sketch, "E1783", {"start": v(77.58, 81.11) * mm, "end": v(44, 100.5) * mm});
            skLineSegment(sketch, "E1784", {"start": v(44, 100.5) * mm, "end": v(43.24, 100.9) * mm});
            skLineSegment(sketch, "E1785", {"start": v(43.24, 100.9) * mm, "end": v(42.5, 101.18) * mm});
            skLineSegment(sketch, "E1786", {"start": v(42.5, 101.18) * mm, "end": v(41.77, 101.38) * mm});
            skLineSegment(sketch, "E1787", {"start": v(41.77, 101.38) * mm, "end": v(41.07, 101.47) * mm});
            skLineSegment(sketch, "E1788", {"start": v(41.07, 101.47) * mm, "end": v(40.4, 101.46) * mm});
            skLineSegment(sketch, "E1789", {"start": v(40.4, 101.46) * mm, "end": v(39.77, 101.36) * mm});
            skLineSegment(sketch, "E1790", {"start": v(39.77, 101.36) * mm, "end": v(39.18, 101.15) * mm});
            skLineSegment(sketch, "E1791", {"start": v(39.18, 101.15) * mm, "end": v(38.65, 100.84) * mm});
            skLineSegment(sketch, "E1792", {"start": v(38.65, 100.84) * mm, "end": v(38.18, 100.44) * mm});
            skLineSegment(sketch, "E1793", {"start": v(38.18, 100.44) * mm, "end": v(37.77, 99.95) * mm});
            skLineSegment(sketch, "E1794", {"start": v(37.77, 99.95) * mm, "end": v(37.43, 99.37) * mm});
            skLineSegment(sketch, "E1795", {"start": v(37.43, 99.37) * mm, "end": v(37.16, 98.71) * mm});
            skLineSegment(sketch, "E1796", {"start": v(37.16, 98.71) * mm, "end": v(36.96, 97.99) * mm});
            skLineSegment(sketch, "E1797", {"start": v(36.96, 97.99) * mm, "end": v(36.85, 97.2) * mm});
            skLineSegment(sketch, "E1798", {"start": v(36.85, 97.2) * mm, "end": v(36.8, 96.35) * mm});
            skLineSegment(sketch, "E1799", {"start": v(36.8, 96.35) * mm, "end": v(36.8, 57.57) * mm});
            skLineSegment(sketch, "E1800", {"start": v(104.09, 53.6) * mm, "end": v(104.99, 54.12) * mm});
            skLineSegment(sketch, "E1801", {"start": v(88.77, 78.22) * mm, "end": v(89.67, 78.73) * mm});
            skLineSegment(sketch, "E1802", {"start": v(82.8, 84.3) * mm, "end": v(83.7, 84.82) * mm});
            skLineSegment(sketch, "E1803", {"start": v(40.59, 108.66) * mm, "end": v(41.48, 109.18) * mm});
            skArc(sketch, "E1804", {"start": v(77.58, 81.11) * mm, "mid": v(77.79, 79.81) * mm, "end": v(78.62, 78.8) * mm});
            skArc(sketch, "E1805", {"start": v(83.27, 70.73) * mm, "mid": v(83.74, 69.5) * mm, "end": v(84.76, 68.67) * mm});
            skArc(sketch, "E1806", {"start": v(83.27, 31.96) * mm, "mid": v(83.74, 30.72) * mm, "end": v(84.76, 29.89) * mm});
            skArc(sketch, "E1807", {"start": v(44, 100.5) * mm, "mid": v(44.2, 99.2) * mm, "end": v(45.04, 98.18) * mm});
            skArc(sketch, "E1808", {"start": v(92.8, 76.42) * mm, "mid": v(91.5, 80.86) * mm, "end": v(88.3, 84.2) * mm});
            skLineSegment(sketch, "E1809", {"start": v(92.8, 76.42) * mm, "end": v(91.56, 75.7) * mm});
            skLineSegment(sketch, "E1810", {"start": v(88.3, 84.2) * mm, "end": v(86.18, 82.97) * mm});
            skLineSegment(sketch, "E1811", {"start": v(92.8, 73.7) * mm, "end": v(92.8, 76.42) * mm});
            skLineSegment(sketch, "E1812", {"start": v(88.3, 84.2) * mm, "end": v(54.72, 103.59) * mm});
            skLineSegment(sketch, "E1813", {"start": v(54.72, 103.59) * mm, "end": v(52.95, 102.56) * mm});
            skArc(sketch, "E1814", {"start": v(90.69, 84.43) * mm, "mid": v(89.47, 84.64) * mm, "end": v(88.3, 84.2) * mm});
            skArc(sketch, "E1815", {"start": v(92.8, 76.42) * mm, "mid": v(93.76, 77.2) * mm, "end": v(94.2, 78.37) * mm});
            skArc(sketch, "E1816", {"start": v(57.1, 103.82) * mm, "mid": v(55.88, 104.03) * mm, "end": v(54.72, 103.59) * mm});
            skLineSegment(sketch, "E1817", {"start": v(83.27, 44.7) * mm, "end": v(71.35, 51.57) * mm});
            skArc(sketch, "E1818", {"start": v(81.17, 31.96) * mm, "mid": v(78.6, 29.29) * mm, "end": v(77.58, 25.74) * mm});
            skArc(sketch, "E1819", {"start": v(81.17, 31.96) * mm, "mid": v(82.18, 31.54) * mm, "end": v(83.27, 31.53) * mm});
            skArc(sketch, "E1820", {"start": v(44.66, 98.38) * mm, "mid": v(44.13, 97.43) * mm, "end": v(44, 96.35) * mm});
            skArc(sketch, "E1821", {"start": v(36.8, 96.35) * mm, "mid": v(40.4, 95.47) * mm, "end": v(44, 96.35) * mm});
            skArc(sketch, "E1822", {"start": v(54.72, 103.59) * mm, "mid": v(53.18, 104.17) * mm, "end": v(51.55, 103.9) * mm});
            skLineSegment(sketch, "E1823", {"start": v(83.27, 33.17) * mm, "end": v(81.17, 31.96) * mm});
            skLineSegment(sketch, "E1824", {"start": v(46.1, 97.57) * mm, "end": v(44, 96.35) * mm});
            skArc(sketch, "E1825", {"start": v(47.58, 51.35) * mm, "mid": v(45.02, 48.68) * mm, "end": v(44, 45.13) * mm});
            skLineSegment(sketch, "E1826", {"start": v(81.17, 31.96) * mm, "end": v(47.58, 51.35) * mm});
            skLineSegment(sketch, "E1827", {"start": v(44, 57.57) * mm, "end": v(44, 69.01) * mm});
            skLineSegment(sketch, "E1828", {"start": v(44, 94.78) * mm, "end": v(44, 96.35) * mm});
            skArc(sketch, "E1829", {"start": v(36.8, 57.57) * mm, "mid": v(40.4, 56.69) * mm, "end": v(44, 57.57) * mm});
            skLineSegment(sketch, "E1830", {"start": v(54.72, 55.47) * mm, "end": v(47.58, 51.35) * mm});
            skLineSegment(sketch, "E1831", {"start": v(54.72, 55.47) * mm, "end": v(83.27, 38.99) * mm});
            skLineSegment(sketch, "E1832", {"start": v(51.13, 63.35) * mm, "end": v(51.13, 61.7) * mm});
            skLineSegment(sketch, "E1833", {"start": v(51.13, 61.7) * mm, "end": v(44, 57.57) * mm});
            skLineSegment(sketch, "E1834", {"start": v(51.84, 62) * mm, "end": v(51.66, 61.94) * mm});
            skLineSegment(sketch, "E1835", {"start": v(51.66, 61.94) * mm, "end": v(51.13, 61.7) * mm});
            skLineSegment(sketch, "E1836", {"start": v(54.98, 55.63) * mm, "end": v(54.72, 55.47) * mm});
            skArc(sketch, "E1837", {"start": v(44, 57.57) * mm, "mid": v(45.02, 54.02) * mm, "end": v(47.58, 51.35) * mm});
            skArc(sketch, "E1838", {"start": v(51.13, 61.7) * mm, "mid": v(52.16, 58.14) * mm, "end": v(54.72, 55.47) * mm});
            skLineSegment(sketch, "E1839", {"start": v(66.67, 98.3) * mm, "end": v(66.67, 98.6) * mm});
            skLineSegment(sketch, "E1840", {"start": v(67.4, 98.75) * mm, "end": v(87.98, 86.87) * mm});
            skLineSegment(sketch, "E1841", {"start": v(99.66, 65.27) * mm, "end": v(99.66, 63.97) * mm});
            skLineSegment(sketch, "E1842", {"start": v(101.78, 62.75) * mm, "end": v(101.78, 59.27) * mm});
            skLineSegment(sketch, "E1843", {"start": v(86.48, 105.37) * mm, "end": v(78.38, 110.05) * mm});
            skLineSegment(sketch, "E1844", {"start": v(101.78, 62.75) * mm, "end": v(99.66, 63.97) * mm});
            skLineSegment(sketch, "E1845", {"start": v(94.06, 111.32) * mm, "end": v(96.18, 112.54) * mm});
            skLineSegment(sketch, "E1846", {"start": v(87.25, 127.95) * mm, "end": v(89.38, 129.18) * mm});
            skLineSegment(sketch, "E1847", {"start": v(98.04, 66.2) * mm, "end": v(100.16, 67.43) * mm});
            skLineSegment(sketch, "E1848", {"start": v(90.04, 84.8) * mm, "end": v(90.1, 84.85) * mm});
            skLineSegment(sketch, "E1849", {"start": v(70.72, 104.33) * mm, "end": v(91.22, 92.49) * mm});
            skLineSegment(sketch, "E1850", {"start": v(91.22, 92.49) * mm, "end": v(91.22, 90.04) * mm});
            skLineSegment(sketch, "E1851", {"start": v(87.98, 86.87) * mm, "end": v(90.1, 88.1) * mm});
            skLineSegment(sketch, "E1852", {"start": v(101.78, 66.5) * mm, "end": v(99.66, 65.27) * mm});
            skLineSegment(sketch, "E1853", {"start": v(85.34, 130.28) * mm, "end": v(87.47, 131.5) * mm});
            skLineSegment(sketch, "E1854", {"start": v(81.19, 132.69) * mm, "end": v(83.3, 133.91) * mm});
            skLineSegment(sketch, "E1855", {"start": v(96.53, 96.98) * mm, "end": v(77.26, 108.1) * mm});
            skLineSegment(sketch, "E1856", {"start": v(94.25, 94.24) * mm, "end": v(94.25, 91.79) * mm});
            skLineSegment(sketch, "E1857", {"start": v(86.37, 112) * mm, "end": v(88.34, 113.13) * mm});
            skLineSegment(sketch, "E1858", {"start": v(86.37, 106.17) * mm, "end": v(88.5, 107.4) * mm});
            skLineSegment(sketch, "E1859", {"start": v(67.47, 99.1) * mm, "end": v(66.65, 98.6) * mm});
            skLineSegment(sketch, "E1860", {"start": v(82.53, 71.5) * mm, "end": v(82.53, 48.6) * mm});
            skLineSegment(sketch, "E1861", {"start": v(79.33, 48.6) * mm, "end": v(79.33, 71.76) * mm});
            skLineSegment(sketch, "E1862", {"start": v(80.7, 74.67) * mm, "end": v(44.93, 95.32) * mm});
            skLineSegment(sketch, "E1863", {"start": v(79.33, 71.76) * mm, "end": v(43.1, 92.68) * mm});
            skLineSegment(sketch, "E1864", {"start": v(43.1, 92.68) * mm, "end": v(43.1, 69.53) * mm});
            skLineSegment(sketch, "E1865", {"start": v(50.36, 64.35) * mm, "end": v(72.07, 51.81) * mm});
            skLineSegment(sketch, "E1866", {"start": v(52.16, 61.25) * mm, "end": v(69.52, 51.24) * mm});
            skLineSegment(sketch, "E1867", {"start": v(68.47, 50.74) * mm, "end": v(69.62, 50.63) * mm});
            skLineSegment(sketch, "E1868", {"start": v(96.15, 51.34) * mm, "end": v(95.36, 51.75) * mm});
            skLineSegment(sketch, "E1869", {"start": v(95.36, 51.75) * mm, "end": v(94.58, 52.07) * mm});
            skLineSegment(sketch, "E1870", {"start": v(94.58, 52.07) * mm, "end": v(93.81, 52.3) * mm});
            skLineSegment(sketch, "E1871", {"start": v(93.81, 52.3) * mm, "end": v(93.07, 52.41) * mm});
            skLineSegment(sketch, "E1872", {"start": v(93.07, 52.41) * mm, "end": v(92.35, 52.44) * mm});
            skLineSegment(sketch, "E1873", {"start": v(92.35, 52.44) * mm, "end": v(91.68, 52.36) * mm});
            skLineSegment(sketch, "E1874", {"start": v(91.68, 52.36) * mm, "end": v(91.04, 52.18) * mm});
            skLineSegment(sketch, "E1875", {"start": v(91.04, 52.18) * mm, "end": v(90.45, 51.9) * mm});
            skLineSegment(sketch, "E1876", {"start": v(90.45, 51.9) * mm, "end": v(89.92, 51.54) * mm});
            skLineSegment(sketch, "E1877", {"start": v(89.92, 51.54) * mm, "end": v(89.79, 51.42) * mm});
            skLineSegment(sketch, "E1878", {"start": v(101.09, 31.84) * mm, "end": v(101.26, 31.9) * mm});
            skLineSegment(sketch, "E1879", {"start": v(101.26, 31.9) * mm, "end": v(101.84, 32.18) * mm});
            skLineSegment(sketch, "E1880", {"start": v(101.84, 32.18) * mm, "end": v(102.38, 32.55) * mm});
            skLineSegment(sketch, "E1881", {"start": v(102.38, 32.55) * mm, "end": v(102.85, 33) * mm});
            skLineSegment(sketch, "E1882", {"start": v(102.85, 33) * mm, "end": v(103.25, 33.56) * mm});
            skLineSegment(sketch, "E1883", {"start": v(103.25, 33.56) * mm, "end": v(103.6, 34.19) * mm});
            skLineSegment(sketch, "E1884", {"start": v(103.6, 34.19) * mm, "end": v(103.86, 34.9) * mm});
            skLineSegment(sketch, "E1885", {"start": v(103.86, 34.9) * mm, "end": v(104.05, 35.67) * mm});
            skLineSegment(sketch, "E1886", {"start": v(104.05, 35.67) * mm, "end": v(104.16, 36.5) * mm});
            skLineSegment(sketch, "E1887", {"start": v(104.16, 36.5) * mm, "end": v(104.2, 37.4) * mm});
            skLineSegment(sketch, "E1888", {"start": v(104.2, 37.4) * mm, "end": v(104.16, 38.33) * mm});
            skLineSegment(sketch, "E1889", {"start": v(104.16, 38.33) * mm, "end": v(104.05, 39.3) * mm});
            skLineSegment(sketch, "E1890", {"start": v(104.05, 39.3) * mm, "end": v(103.86, 40.3) * mm});
            skLineSegment(sketch, "E1891", {"start": v(103.86, 40.3) * mm, "end": v(103.6, 41.3) * mm});
            skLineSegment(sketch, "E1892", {"start": v(103.6, 41.3) * mm, "end": v(103.25, 42.33) * mm});
            skLineSegment(sketch, "E1893", {"start": v(103.25, 42.33) * mm, "end": v(102.85, 43.34) * mm});
            skLineSegment(sketch, "E1894", {"start": v(102.85, 43.34) * mm, "end": v(102.38, 44.35) * mm});
            skLineSegment(sketch, "E1895", {"start": v(102.38, 44.35) * mm, "end": v(101.84, 45.33) * mm});
            skLineSegment(sketch, "E1896", {"start": v(101.84, 45.33) * mm, "end": v(101.26, 46.28) * mm});
            skLineSegment(sketch, "E1897", {"start": v(101.26, 46.28) * mm, "end": v(100.62, 47.2) * mm});
            skLineSegment(sketch, "E1898", {"start": v(100.62, 47.2) * mm, "end": v(99.95, 48.05) * mm});
            skLineSegment(sketch, "E1899", {"start": v(99.95, 48.05) * mm, "end": v(99.23, 48.86) * mm});
            skLineSegment(sketch, "E1900", {"start": v(99.23, 48.86) * mm, "end": v(98.49, 49.6) * mm});
            skLineSegment(sketch, "E1901", {"start": v(98.49, 49.6) * mm, "end": v(97.72, 50.26) * mm});
            skLineSegment(sketch, "E1902", {"start": v(97.72, 50.26) * mm, "end": v(96.94, 50.84) * mm});
            skLineSegment(sketch, "E1903", {"start": v(96.94, 50.84) * mm, "end": v(96.15, 51.34) * mm});
            const initialGuessF0  = {"E851": [-0.10028556, 0.01195262, 0.618178, 0.192113, 0.00647342, 0.00069326, 2.641558, 3.473452]};
            skSetInitialGuess(sketch, initialGuessF0);
            skSolve(sketch);
        }
        {
            var Q0;
            Q0=makeQuery(id+"F0.imprint","IMPRINT",FACE,{"disambiguationData":[TD([[makeQuery(id+"F0.imprint","IMPRINT",EDGE,{"derivedFrom":sQuery(id+"F0.wireOp",EDGE,"E4")}),1.0]])]});
            var Q1;
            Q1=makeQuery(id+"F0.imprint","IMPRINT",FACE,{"disambiguationData":[TD([[makeQuery(id+"F0.imprint","IMPRINT",EDGE,{"derivedFrom":sQuery(id+"F0.wireOp",EDGE,"E38")}),-1.0]])]});
            var Q2;
            {var subQ3=sQuery(id+"F0.wireOp",EDGE,"E38");Q2=makeQuery(id+"F0.imprint","IMPRINT",FACE,{"disambiguationData":[TD([[makeQuery(id+"F0.imprint","IMPRINT",EDGE,{"derivedFrom":subQ3}),1.0]])]});}
            var Q3;
            Q3=makeQuery(id+"F0.imprint","IMPRINT",FACE,{"disambiguationData":[TD([[makeQuery(id+"F0.imprint","IMPRINT",EDGE,{"derivedFrom":sQuery(id+"F0.wireOp",EDGE,"E37")}),1.0]])]});
            var Q4;
            {var subQ7=sQuery(id+"F0.wireOp",EDGE,"E8");Q4=makeQuery(id+"F0.imprint","IMPRINT",FACE,{"disambiguationData":[TD([[makeQuery(id+"F0.imprint","IMPRINT",EDGE,{"derivedFrom":subQ7}),-1.0]])]});}
            var Q5;
            Q5=makeQuery(id+"F0.imprint","IMPRINT",FACE,{"disambiguationData":[TD([[makeQuery(id+"F0.imprint","IMPRINT",EDGE,{"derivedFrom":sQuery(id+"F0.wireOp",EDGE,"E37")}),-1.0]])]});
            var Q6;
            Q6=makeQuery(id+"F0.imprint","IMPRINT",FACE,{"disambiguationData":[TD([[makeQuery(id+"F0.imprint","IMPRINT",EDGE,{"derivedFrom":sQuery(id+"F0.wireOp",EDGE,"E22")}),-1.0]])]});
            var Q7;
            Q7=makeQuery(id+"F0.imprint","IMPRINT",FACE,{"disambiguationData":[TD([[makeQuery(id+"F0.imprint","IMPRINT",EDGE,{"derivedFrom":sQuery(id+"F0.wireOp",EDGE,"E22")}),1.0]])]});
            var Q8;
            {var subQ7=sQuery(id+"F0.wireOp",EDGE,"E5");Q8=makeQuery(id+"F0.imprint","IMPRINT",FACE,{"disambiguationData":[TD([[makeQuery(id+"F0.imprint","IMPRINT",EDGE,{"derivedFrom":subQ7}),-1.0]])]});}
            var Q9;
            Q9=makeQuery(id+"F0.imprint","IMPRINT",FACE,{"disambiguationData":[TD([[makeQuery(id+"F0.imprint","IMPRINT",EDGE,{"derivedFrom":sQuery(id+"F0.wireOp",EDGE,"E19")}),1.0]])]});
            var Q10;
            Q10=makeQuery(id+"F0.imprint","IMPRINT",FACE,{"disambiguationData":[TD([[makeQuery(id+"F0.imprint","IMPRINT",EDGE,{"derivedFrom":sQuery(id+"F0.wireOp",EDGE,"E186")}),-1.0]])]});
            var Q11;
            Q11=makeQuery(id+"F0.imprint","IMPRINT",FACE,{"disambiguationData":[TD([[makeQuery(id+"F0.imprint","IMPRINT",EDGE,{"derivedFrom":sQuery(id+"F0.wireOp",EDGE,"E18")}),-1.0]])]});
            var Q12;
            {var subQ6=sQuery(id+"F0.wireOp",EDGE,"E99");Q12=makeQuery(id+"F0.imprint","IMPRINT",FACE,{"disambiguationData":[TD([[makeQuery(id+"F0.imprint","IMPRINT",EDGE,{"derivedFrom":subQ6}),-1.0]])]});}
            var Q13;
            {var subQ3=sQuery(id+"F0.wireOp",EDGE,"E18");Q13=makeQuery(id+"F0.imprint","IMPRINT",FACE,{"disambiguationData":[TD([[makeQuery(id+"F0.imprint","IMPRINT",EDGE,{"derivedFrom":subQ3}),1.0]])]});}
            var Q14;
            {var subQ2=sQuery(id+"F0.wireOp",EDGE,"E97");Q14=makeQuery(id+"F0.imprint","IMPRINT",FACE,{"disambiguationData":[TD([[makeQuery(id+"F0.imprint","IMPRINT",EDGE,{"derivedFrom":subQ2}),-1.0]])]});}
            var Q15;
            Q15=makeQuery(id+"F0.imprint","IMPRINT",FACE,{"disambiguationData":[TD([[makeQuery(id+"F0.imprint","IMPRINT",EDGE,{"derivedFrom":sQuery(id+"F0.wireOp",EDGE,"E17")}),1.0]])]});
            var Q16;
            Q16=makeQuery(id+"F0.imprint","IMPRINT",FACE,{"disambiguationData":[TD([[makeQuery(id+"F0.imprint","IMPRINT",EDGE,{"derivedFrom":sQuery(id+"F0.wireOp",EDGE,"E63")}),1.0]])]});
            var Q17;
            {var subQ0=sQuery(id+"F0.wireOp",EDGE,"E184");Q17=makeQuery(id+"F0.imprint","IMPRINT",FACE,{"disambiguationData":[TD([[makeQuery(id+"F0.imprint","IMPRINT",EDGE,{"derivedFrom":subQ0}),-1.0]])]});}
            var Q18;
            {var subQ6=sQuery(id+"F0.wireOp",EDGE,"E1");Q18=makeQuery(id+"F0.imprint","IMPRINT",FACE,{"disambiguationData":[TD([[makeQuery(id+"F0.imprint","IMPRINT",EDGE,{"derivedFrom":subQ6}),-1.0]])]});}
            var Q19;
            Q19=makeQuery(id+"F0.imprint","IMPRINT",FACE,{"disambiguationData":[TD([[makeQuery(id+"F0.imprint","IMPRINT",EDGE,{"derivedFrom":sQuery(id+"F0.wireOp",EDGE,"E17")}),-1.0]])]});
            var Q20;
            {var subQ1=sQuery(id+"F0.wireOp",EDGE,"E113");Q20=makeQuery(id+"F0.imprint","IMPRINT",FACE,{"disambiguationData":[TD([[makeQuery(id+"F0.imprint","IMPRINT",EDGE,{"derivedFrom":subQ1}),-1.0]])]});}
            var Q21;
            {var subQ5=sQuery(id+"F0.wireOp",EDGE,"E91");Q21=makeQuery(id+"F0.imprint","IMPRINT",FACE,{"disambiguationData":[TD([[makeQuery(id+"F0.imprint","IMPRINT",EDGE,{"derivedFrom":subQ5}),-1.0]])]});}
            var Q22;
            {var subQ6=sQuery(id+"F0.wireOp",EDGE,"E0");Q22=makeQuery(id+"F0.imprint","IMPRINT",FACE,{"disambiguationData":[TD([[makeQuery(id+"F0.imprint","IMPRINT",EDGE,{"derivedFrom":subQ6}),-1.0]])]});}
            var Q23;
            Q23=makeQuery(id+"F0.imprint","IMPRINT",FACE,{"disambiguationData":[TD([[makeQuery(id+"F0.imprint","IMPRINT",EDGE,{"derivedFrom":sQuery(id+"F0.wireOp",EDGE,"E64")}),-1.0]])]});
            var Q24;
            {var subQ1=sQuery(id+"F0.wireOp",EDGE,"E120");Q24=makeQuery(id+"F0.imprint","IMPRINT",FACE,{"disambiguationData":[TD([[makeQuery(id+"F0.imprint","IMPRINT",EDGE,{"derivedFrom":subQ1}),1.0]])]});}
            var Q25;
            Q25=makeQuery(id+"F0.imprint","IMPRINT",FACE,{"disambiguationData":[TD([[makeQuery(id+"F0.imprint","IMPRINT",EDGE,{"derivedFrom":sQuery(id+"F0.wireOp",EDGE,"E35")}),-1.0]])]});
            var Q26;
            Q26=makeQuery(id+"F0.imprint","IMPRINT",FACE,{"disambiguationData":[TD([[makeQuery(id+"F0.imprint","IMPRINT",EDGE,{"derivedFrom":sQuery(id+"F0.wireOp",EDGE,"E24")}),-1.0]])]});
            var Q27;
            Q27=makeQuery(id+"F0.imprint","IMPRINT",FACE,{"disambiguationData":[TD([[makeQuery(id+"F0.imprint","IMPRINT",EDGE,{"derivedFrom":sQuery(id+"F0.wireOp",EDGE,"E63")}),-1.0]])]});
            var Q28;
            Q28=makeQuery(id+"F0.imprint","IMPRINT",FACE,{"disambiguationData":[TD([[makeQuery(id+"F0.imprint","IMPRINT",EDGE,{"derivedFrom":sQuery(id+"F0.wireOp",EDGE,"E4")}),-1.0]])]});
            var Q29;
            {var subQ2=sQuery(id+"F0.wireOp",EDGE,"E1");Q29=makeQuery(id+"F0.imprint","IMPRINT",FACE,{"disambiguationData":[TD([[makeQuery(id+"F0.imprint","IMPRINT",EDGE,{"derivedFrom":subQ2}),1.0]])]});}
            var Q30;
            {var subQ2=sQuery(id+"F0.wireOp",EDGE,"E0");Q30=makeQuery(id+"F0.imprint","IMPRINT",FACE,{"disambiguationData":[TD([[makeQuery(id+"F0.imprint","IMPRINT",EDGE,{"derivedFrom":subQ2}),1.0]])]});}
            var Q31;
            {var subQ2=sQuery(id+"F0.wireOp",EDGE,"E3");Q31=makeQuery(id+"F0.imprint","IMPRINT",FACE,{"disambiguationData":[TD([[makeQuery(id+"F0.imprint","IMPRINT",EDGE,{"derivedFrom":subQ2}),-1.0]])]});}
            var Q32;
            {var subQ7=sQuery(id+"F0.wireOp",EDGE,"E2");Q32=makeQuery(id+"F0.imprint","IMPRINT",FACE,{"disambiguationData":[TD([[makeQuery(id+"F0.imprint","IMPRINT",EDGE,{"derivedFrom":subQ7}),-1.0]])]});}
            var Q33;
            Q33=makeQuery(id+"F0.imprint","IMPRINT",FACE,{"disambiguationData":[TD([[makeQuery(id+"F0.imprint","IMPRINT",EDGE,{"derivedFrom":sQuery(id+"F0.wireOp",EDGE,"E75")}),1.0]])]});
            var Q34;
            Q34=makeQuery(id+"F0.imprint","IMPRINT",FACE,{"disambiguationData":[TD([[makeQuery(id+"F0.imprint","IMPRINT",EDGE,{"derivedFrom":sQuery(id+"F0.wireOp",EDGE,"E111")}),1.0]])]});
            var Q35;
            {var subQ2=sQuery(id+"F0.wireOp",EDGE,"E47");Q35=makeQuery(id+"F0.imprint","IMPRINT",FACE,{"disambiguationData":[TD([[makeQuery(id+"F0.imprint","IMPRINT",EDGE,{"derivedFrom":subQ2}),-1.0]])]});}
            var Q36;
            Q36=makeQuery(id+"F0.imprint","IMPRINT",FACE,{"disambiguationData":[TD([[makeQuery(id+"F0.imprint","IMPRINT",EDGE,{"derivedFrom":sQuery(id+"F0.wireOp",EDGE,"E66")}),-1.0]])]});
            var Q37;
            {var subQ2=sQuery(id+"F0.wireOp",EDGE,"E49");Q37=makeQuery(id+"F0.imprint","IMPRINT",FACE,{"disambiguationData":[TD([[makeQuery(id+"F0.imprint","IMPRINT",EDGE,{"derivedFrom":subQ2}),-1.0]])]});}
            var Q38;
            {var subQ2=sQuery(id+"F0.wireOp",EDGE,"E51");Q38=makeQuery(id+"F0.imprint","IMPRINT",FACE,{"disambiguationData":[TD([[makeQuery(id+"F0.imprint","IMPRINT",EDGE,{"derivedFrom":subQ2}),-1.0]])]});}
            var Q39;
            Q39=makeQuery(id+"F0.imprint","IMPRINT",FACE,{"disambiguationData":[TD([[makeQuery(id+"F0.imprint","IMPRINT",EDGE,{"derivedFrom":sQuery(id+"F0.wireOp",EDGE,"E67")}),-1.0]])]});
            var Q40;
            Q40=makeQuery(id+"F0.imprint","IMPRINT",FACE,{"disambiguationData":[TD([[makeQuery(id+"F0.imprint","IMPRINT",EDGE,{"derivedFrom":sQuery(id+"F0.wireOp",EDGE,"E36")}),-1.0]])]});
            var Q41;
            Q41=makeQuery(id+"F0.imprint","IMPRINT",FACE,{"disambiguationData":[TD([[makeQuery(id+"F0.imprint","IMPRINT",EDGE,{"derivedFrom":sQuery(id+"F0.wireOp",EDGE,"E23")}),-1.0]])]});
            var Q42;
            {var subQ1=sQuery(id+"F0.wireOp",EDGE,"E53");Q42=makeQuery(id+"F0.imprint","IMPRINT",FACE,{"disambiguationData":[TD([[makeQuery(id+"F0.imprint","IMPRINT",EDGE,{"derivedFrom":subQ1}),-1.0]])]});}
            var Q43;
            {var subQ2=sQuery(id+"F0.wireOp",EDGE,"E7");Q43=makeQuery(id+"F0.imprint","IMPRINT",FACE,{"disambiguationData":[TD([[makeQuery(id+"F0.imprint","IMPRINT",EDGE,{"derivedFrom":subQ2}),-1.0]])]});}
            var Q44;
            {var subQ1=sQuery(id+"F0.wireOp",EDGE,"E45");Q44=makeQuery(id+"F0.imprint","IMPRINT",FACE,{"disambiguationData":[TD([[makeQuery(id+"F0.imprint","IMPRINT",EDGE,{"derivedFrom":subQ1}),-1.0]])]});}
            var Q45;
            {var subQ2=sQuery(id+"F0.wireOp",EDGE,"E5");Q45=makeQuery(id+"F0.imprint","IMPRINT",FACE,{"disambiguationData":[TD([[makeQuery(id+"F0.imprint","IMPRINT",EDGE,{"derivedFrom":subQ2}),1.0]])]});}
            var Q46;
            {var subQ2=sQuery(id+"F0.wireOp",EDGE,"E59");Q46=makeQuery(id+"F0.imprint","IMPRINT",FACE,{"disambiguationData":[TD([[makeQuery(id+"F0.imprint","IMPRINT",EDGE,{"derivedFrom":subQ2}),-1.0]])]});}
            var Q47;
            {var subQ6=sQuery(id+"F0.wireOp",EDGE,"E11");Q47=makeQuery(id+"F0.imprint","IMPRINT",FACE,{"disambiguationData":[TD([[makeQuery(id+"F0.imprint","IMPRINT",EDGE,{"derivedFrom":subQ6}),1.0]])]});}
            var Q48;
            {var subQ1=sQuery(id+"F0.wireOp",EDGE,"E57");Q48=makeQuery(id+"F0.imprint","IMPRINT",FACE,{"disambiguationData":[TD([[makeQuery(id+"F0.imprint","IMPRINT",EDGE,{"derivedFrom":subQ1}),-1.0]])]});}
            var Q49;
            {var subQ5=sQuery(id+"F0.wireOp",EDGE,"E7");Q49=makeQuery(id+"F0.imprint","IMPRINT",FACE,{"disambiguationData":[TD([[makeQuery(id+"F0.imprint","IMPRINT",EDGE,{"derivedFrom":subQ5}),1.0]])]});}
            var Q50;
            {var subQ1=sQuery(id+"F0.wireOp",EDGE,"E55");Q50=makeQuery(id+"F0.imprint","IMPRINT",FACE,{"disambiguationData":[TD([[makeQuery(id+"F0.imprint","IMPRINT",EDGE,{"derivedFrom":subQ1}),-1.0]])]});}
            var Q51;
            {var subQ1=sQuery(id+"F0.wireOp",EDGE,"E57");Q51=makeQuery(id+"F0.imprint","IMPRINT",FACE,{"disambiguationData":[TD([[makeQuery(id+"F0.imprint","IMPRINT",EDGE,{"derivedFrom":subQ1}),1.0]])]});}
            var Q52;
            {var subQ1=sQuery(id+"F0.wireOp",EDGE,"E55");Q52=makeQuery(id+"F0.imprint","IMPRINT",FACE,{"disambiguationData":[TD([[makeQuery(id+"F0.imprint","IMPRINT",EDGE,{"derivedFrom":subQ1}),1.0]])]});}
            var Q53;
            {var subQ1=sQuery(id+"F0.wireOp",EDGE,"E52");Q53=makeQuery(id+"F0.imprint","IMPRINT",FACE,{"disambiguationData":[TD([[makeQuery(id+"F0.imprint","IMPRINT",EDGE,{"derivedFrom":subQ1}),1.0]])]});}
            var Q54;
            {var subQ1=sQuery(id+"F0.wireOp",EDGE,"E47");Q54=makeQuery(id+"F0.imprint","IMPRINT",FACE,{"disambiguationData":[TD([[makeQuery(id+"F0.imprint","IMPRINT",EDGE,{"derivedFrom":subQ1}),1.0]])]});}
            var Q55;
            {var subQ1=sQuery(id+"F0.wireOp",EDGE,"E45");Q55=makeQuery(id+"F0.imprint","IMPRINT",FACE,{"disambiguationData":[TD([[makeQuery(id+"F0.imprint","IMPRINT",EDGE,{"derivedFrom":subQ1}),1.0]])]});}
            var Q56;
            {var subQ1=sQuery(id+"F0.wireOp",EDGE,"E46");Q56=makeQuery(id+"F0.imprint","IMPRINT",FACE,{"disambiguationData":[TD([[makeQuery(id+"F0.imprint","IMPRINT",EDGE,{"derivedFrom":subQ1}),1.0]])]});}
            var Q57;
            {var subQ1=sQuery(id+"F0.wireOp",EDGE,"E50");Q57=makeQuery(id+"F0.imprint","IMPRINT",FACE,{"disambiguationData":[TD([[makeQuery(id+"F0.imprint","IMPRINT",EDGE,{"derivedFrom":subQ1}),1.0]])]});}
            var Q58;
            Q58=makeQuery(id+"F0.imprint","IMPRINT",FACE,{"disambiguationData":[TD([[makeQuery(id+"F0.imprint","IMPRINT",EDGE,{"derivedFrom":sQuery(id+"F0.wireOp",EDGE,"E74")}),1.0]])]});
            var Q59;
            Q59=makeQuery(id+"F0.imprint","IMPRINT",FACE,{"disambiguationData":[TD([[makeQuery(id+"F0.imprint","IMPRINT",EDGE,{"derivedFrom":sQuery(id+"F0.wireOp",EDGE,"E72")}),1.0]])]});
            var Q60;
            Q60=makeQuery(id+"F0.imprint","IMPRINT",FACE,{"disambiguationData":[TD([[makeQuery(id+"F0.imprint","IMPRINT",EDGE,{"derivedFrom":sQuery(id+"F0.wireOp",EDGE,"E68")}),-1.0]])]});
            var Q61;
            {var subQ1=sQuery(id+"F0.wireOp",EDGE,"E61");Q61=makeQuery(id+"F0.imprint","IMPRINT",FACE,{"disambiguationData":[TD([[makeQuery(id+"F0.imprint","IMPRINT",EDGE,{"derivedFrom":subQ1}),1.0]])]});}
            var Q62;
            Q62=makeQuery(id+"F0.imprint","IMPRINT",FACE,{"disambiguationData":[TD([[makeQuery(id+"F0.imprint","IMPRINT",EDGE,{"derivedFrom":sQuery(id+"F0.wireOp",EDGE,"E78")}),-1.0]])]});
            var Q63;
            Q63=makeQuery(id+"F0.imprint","IMPRINT",FACE,{"disambiguationData":[TD([[makeQuery(id+"F0.imprint","IMPRINT",EDGE,{"derivedFrom":sQuery(id+"F0.wireOp",EDGE,"E77")}),1.0]])]});
            var Q64;
            Q64=makeQuery(id+"F0.imprint","IMPRINT",FACE,{"disambiguationData":[TD([[makeQuery(id+"F0.imprint","IMPRINT",EDGE,{"derivedFrom":sQuery(id+"F0.wireOp",EDGE,"E65")}),-1.0]])]});
            var Q65;
            {var subQ1=sQuery(id+"F0.wireOp",EDGE,"E165");Q65=makeQuery(id+"F0.imprint","IMPRINT",FACE,{"disambiguationData":[TD([[makeQuery(id+"F0.imprint","IMPRINT",EDGE,{"derivedFrom":subQ1}),1.0]])]});}
            var Q66;
            Q66=makeQuery(id+"F0.imprint","IMPRINT",FACE,{"disambiguationData":[TD([[makeQuery(id+"F0.imprint","IMPRINT",EDGE,{"derivedFrom":sQuery(id+"F0.wireOp",EDGE,"E136")}),-1.0]])]});
            var Q67;
            {var subQ1=sQuery(id+"F0.wireOp",EDGE,"E149");Q67=makeQuery(id+"F0.imprint","IMPRINT",FACE,{"disambiguationData":[TD([[makeQuery(id+"F0.imprint","IMPRINT",EDGE,{"derivedFrom":subQ1}),-1.0]])]});}
            var Q68;
            Q68=makeQuery(id+"F0.imprint","IMPRINT",FACE,{"disambiguationData":[TD([[makeQuery(id+"F0.imprint","IMPRINT",EDGE,{"derivedFrom":sQuery(id+"F0.wireOp",EDGE,"E156")}),-1.0]])]});
            var Q69;
            {var subQ1=sQuery(id+"F0.wireOp",EDGE,"E164");Q69=makeQuery(id+"F0.imprint","IMPRINT",FACE,{"disambiguationData":[TD([[makeQuery(id+"F0.imprint","IMPRINT",EDGE,{"derivedFrom":subQ1}),1.0]])]});}
            var Q70;
            Q70=makeQuery(id+"F0.imprint","IMPRINT",FACE,{"disambiguationData":[TD([[makeQuery(id+"F0.imprint","IMPRINT",EDGE,{"derivedFrom":sQuery(id+"F0.wireOp",EDGE,"E161")}),-1.0]])]});
            var Q71;
            Q71=makeQuery(id+"F0.imprint","IMPRINT",FACE,{"disambiguationData":[TD([[makeQuery(id+"F0.imprint","IMPRINT",EDGE,{"derivedFrom":sQuery(id+"F0.wireOp",EDGE,"E141")}),-1.0]])]});
            var Q72;
            {var subQ3=sQuery(id+"F0.wireOp",EDGE,"E167");Q72=makeQuery(id+"F0.imprint","IMPRINT",FACE,{"disambiguationData":[TD([[makeQuery(id+"F0.imprint","IMPRINT",EDGE,{"derivedFrom":subQ3}),1.0]])]});}
            var Q73;
            {var subQ3=sQuery(id+"F0.wireOp",EDGE,"E170");Q73=makeQuery(id+"F0.imprint","IMPRINT",FACE,{"disambiguationData":[TD([[makeQuery(id+"F0.imprint","IMPRINT",EDGE,{"derivedFrom":subQ3}),1.0]])]});}
            var Q74;
            Q74=makeQuery(id+"F0.imprint","IMPRINT",FACE,{"disambiguationData":[TD([[makeQuery(id+"F0.imprint","IMPRINT",EDGE,{"derivedFrom":sQuery(id+"F0.wireOp",EDGE,"E171")}),1.0]])]});
            var Q75;
            {var subQ1=sQuery(id+"F0.wireOp",EDGE,"E172");Q75=makeQuery(id+"F0.imprint","IMPRINT",FACE,{"disambiguationData":[TD([[makeQuery(id+"F0.imprint","IMPRINT",EDGE,{"derivedFrom":subQ1}),1.0]])]});}
            var Q76;
            {var subQ3=sQuery(id+"F0.wireOp",EDGE,"E142");Q76=makeQuery(id+"F0.imprint","IMPRINT",FACE,{"disambiguationData":[TD([[makeQuery(id+"F0.imprint","IMPRINT",EDGE,{"derivedFrom":subQ3}),-1.0]])]});}
            var Q77;
            {var subQ1=sQuery(id+"F0.wireOp",EDGE,"E39");Q77=makeQuery(id+"F0.imprint","IMPRINT",FACE,{"disambiguationData":[TD([[makeQuery(id+"F0.imprint","IMPRINT",EDGE,{"derivedFrom":subQ1}),1.0]])]});}
            var Q78;
            Q78=sQuery(id+"F0.wireOp",EDGE,"E31");
            var Q79;
            Q79=sQuery(id+"F0.wireOp",EDGE,"E30");
            var Q80;
            Q80=sQuery(id+"F0.wireOp",EDGE,"E29");
            var Q81;
            Q81=sQuery(id+"F0.wireOp",EDGE,"E28");
            var Q82;
            Q82=sQuery(id+"F0.wireOp",EDGE,"E27");
            var Q83;
            Q83=sQuery(id+"F0.wireOp",EDGE,"E26");
            var Q84;
            Q84=sQuery(id+"F0.wireOp",EDGE,"E25");
            var Q85;
            Q85=sQuery(id+"F0.wireOp",EDGE,"E34");
            var Q86;
            Q86=sQuery(id+"F0.wireOp",EDGE,"E33");
            var Q87;
            Q87=sQuery(id+"F0.wireOp",EDGE,"E32");
            var Q88;
            Q88=sQuery(id+"F0.wireOp",EDGE,"E121");
            var Q89;
            Q89=sQuery(id+"F0.wireOp",EDGE,"E126");
            var Q90;
            Q90=sQuery(id+"F0.wireOp",EDGE,"E124");
            var Q91;
            Q91=sQuery(id+"F0.wireOp",EDGE,"E112");
            var Q92;
            Q92=sQuery(id+"F0.wireOp",EDGE,"E123");
            var Q93;
            Q93=sQuery(id+"F0.wireOp",EDGE,"E115");
            var Q94;
            Q94=sQuery(id+"F0.wireOp",EDGE,"E118");
            var Q95;
            Q95=sQuery(id+"F0.wireOp",EDGE,"E127");
            var Q96;
            Q96=sQuery(id+"F0.wireOp",EDGE,"E43");
            var Q97;
            Q97=sQuery(id+"F0.wireOp",EDGE,"E42");
            var Q98;
            Q98=sQuery(id+"F0.wireOp",EDGE,"E41");
            var Q99;
            Q99=sQuery(id+"F0.wireOp",EDGE,"E40");
            extrude(context, id + "F1", {"entities" : qUnion([Q0, Q1, Q2, Q3, Q4, Q5, Q6, Q7, Q8, Q9, Q10, Q11, Q12, Q13, Q14, Q15, Q16, Q17, Q18, Q19, Q20, Q21, Q22, Q23, Q24, Q25, Q26, Q27, Q28, Q29, Q30, Q31, Q32, Q33, Q34, Q35, Q36, Q37, Q38, Q39, Q40, Q41, Q42, Q43, Q44, Q45, Q46, Q47, Q48, Q49, Q50, Q51, Q52, Q53, Q54, Q55, Q56, Q57, Q58, Q59, Q60, Q61, Q62, Q63, Q64, Q65, Q66, Q67, Q68, Q69, Q70, Q71, Q72, Q73, Q74, Q75, Q76, Q77]), "bodyType" : ToolBodyType.SURFACE, "surfaceEntities" : qUnion([Q78, Q79, Q80, Q81, Q82, Q83, Q84, Q85, Q86, Q87, Q88, Q89, Q90, Q91, Q92, Q93, Q94, Q95, Q96, Q97, Q98, Q99]), "depth" : 2.54 * mm});
        }
    });
